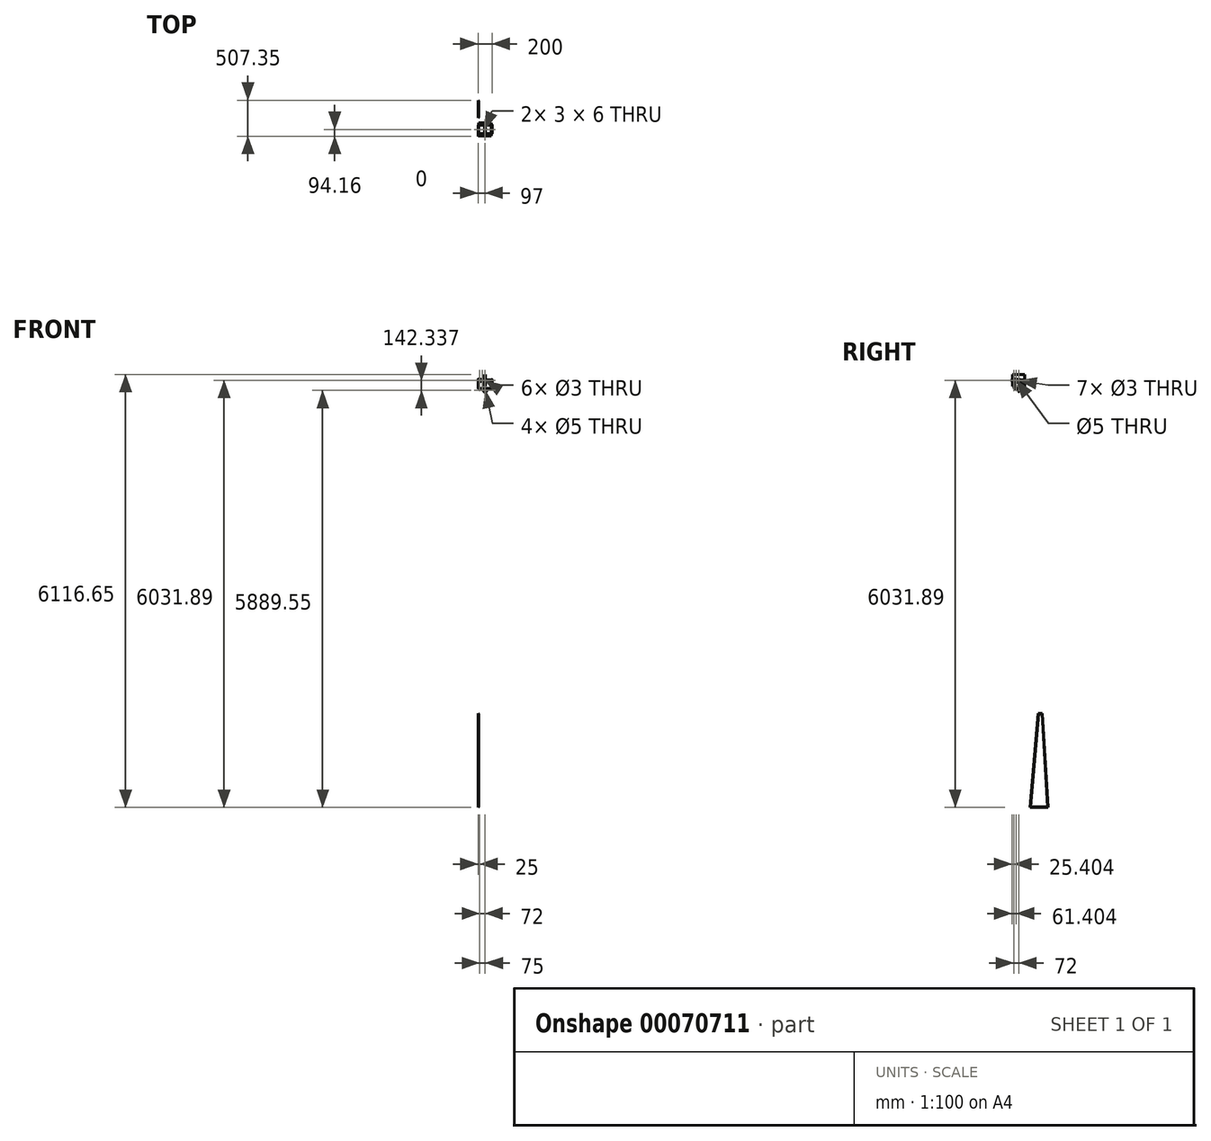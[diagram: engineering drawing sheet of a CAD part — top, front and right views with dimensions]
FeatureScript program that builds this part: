
annotation { "Feature Type Name" : "Feature", "Feature Type Description" : "" }
export const myFeature = defineFeature(function(context is Context, id is Id, definition is map)
    precondition{}
    {
        {
            var Q0;
            Q0=qCreatedBy(makeId("Top.planeOp"),FACE);
            var sketch = newSketch(context, id + "F0", { "sketchPlane" : qUnion([Q0])});
            skLineSegment(sketch, "E0.rect.bottom", {"start": v(100, 60) * mm, "end": v(-95, 60) * mm});
            skLineSegment(sketch, "E0.rect.top", {"start": v(95, -60) * mm, "end": v(-100, -60) * mm});
            skLineSegment(sketch, "E0.rect.left", {"start": v(100, 60) * mm, "end": v(100, 55) * mm});
            skLineSegment(sketch, "E0.rect.right", {"start": v(-100, 55) * mm, "end": v(-100, 50) * mm});
            skPoint(sketch, "E0.rect.middle", {"position": v(0, 0) * mm});
            skLineSegment(sketch, "E1.bottom", {"start": v(100, 55) * mm, "end": v(95, 55) * mm});
            skLineSegment(sketch, "E1.top", {"start": v(100, 50) * mm, "end": v(95, 50) * mm});
            skLineSegment(sketch, "E1.right", {"start": v(95, 55) * mm, "end": v(95, 50) * mm});
            skLineSegment(sketch, "E2.0.1.0", {"start": v(100, 45) * mm, "end": v(95, 45) * mm});
            skLineSegment(sketch, "E2.0.1.1", {"start": v(95, 45) * mm, "end": v(95, 40) * mm});
            skLineSegment(sketch, "E2.0.1.2", {"start": v(100, 40) * mm, "end": v(95, 40) * mm});
            skLineSegment(sketch, "E2.0.2.0", {"start": v(100, 35) * mm, "end": v(95, 35) * mm});
            skLineSegment(sketch, "E2.0.2.1", {"start": v(95, 35) * mm, "end": v(95, 30) * mm});
            skLineSegment(sketch, "E2.0.2.2", {"start": v(100, 30) * mm, "end": v(95, 30) * mm});
            skLineSegment(sketch, "E2.0.3.0", {"start": v(100, 25) * mm, "end": v(95, 25) * mm});
            skLineSegment(sketch, "E2.0.3.1", {"start": v(95, 25) * mm, "end": v(95, 20) * mm});
            skLineSegment(sketch, "E2.0.3.2", {"start": v(100, 20) * mm, "end": v(95, 20) * mm});
            skLineSegment(sketch, "E2.0.4.0", {"start": v(100, 15) * mm, "end": v(95, 15) * mm});
            skLineSegment(sketch, "E2.0.4.1", {"start": v(95, 15) * mm, "end": v(95, 10) * mm});
            skLineSegment(sketch, "E2.0.4.2", {"start": v(100, 10) * mm, "end": v(95, 10) * mm});
            skLineSegment(sketch, "E2.0.5.0", {"start": v(100, 5) * mm, "end": v(95, 5) * mm});
            skLineSegment(sketch, "E2.0.5.1", {"start": v(95, 5) * mm, "end": v(95, 0) * mm});
            skLineSegment(sketch, "E2.0.5.2", {"start": v(100, 0) * mm, "end": v(95, 0) * mm});
            skLineSegment(sketch, "E2.0.6.0", {"start": v(100, -5) * mm, "end": v(95, -5) * mm});
            skLineSegment(sketch, "E2.0.6.1", {"start": v(95, -5) * mm, "end": v(95, -10) * mm});
            skLineSegment(sketch, "E2.0.6.2", {"start": v(100, -10) * mm, "end": v(95, -10) * mm});
            skLineSegment(sketch, "E2.0.7.0", {"start": v(100, -15) * mm, "end": v(95, -15) * mm});
            skLineSegment(sketch, "E2.0.7.1", {"start": v(95, -15) * mm, "end": v(95, -20) * mm});
            skLineSegment(sketch, "E2.0.7.2", {"start": v(100, -20) * mm, "end": v(95, -20) * mm});
            skLineSegment(sketch, "E2.0.8.0", {"start": v(100, -25) * mm, "end": v(95, -25) * mm});
            skLineSegment(sketch, "E2.0.8.1", {"start": v(95, -25) * mm, "end": v(95, -30) * mm});
            skLineSegment(sketch, "E2.0.8.2", {"start": v(100, -30) * mm, "end": v(95, -30) * mm});
            skLineSegment(sketch, "E2.0.9.0", {"start": v(100, -35) * mm, "end": v(95, -35) * mm});
            skLineSegment(sketch, "E2.0.9.1", {"start": v(95, -35) * mm, "end": v(95, -40) * mm});
            skLineSegment(sketch, "E2.0.9.2", {"start": v(100, -40) * mm, "end": v(95, -40) * mm});
            skLineSegment(sketch, "E2.0.10.0", {"start": v(100, -45) * mm, "end": v(95, -45) * mm});
            skLineSegment(sketch, "E2.0.10.1", {"start": v(95, -45) * mm, "end": v(95, -50) * mm});
            skLineSegment(sketch, "E2.0.10.2", {"start": v(100, -50) * mm, "end": v(95, -50) * mm});
            skLineSegment(sketch, "E2.0.11.0", {"start": v(100, -55) * mm, "end": v(95, -55) * mm});
            skLineSegment(sketch, "E2.0.11.1", {"start": v(95, -55) * mm, "end": v(95, -60) * mm});
            skLineSegment(sketch, "E2.direction1", {"start": v(95, 55) * mm, "end": v(119, 55) * mm, "construction": true});
            skLineSegment(sketch, "E2.direction2", {"start": v(95, 55) * mm, "end": v(95, 45) * mm, "construction": true});
            skLineSegment(sketch, "E3", {"start": v(0, -60) * mm, "end": v(0, 60) * mm, "construction": true});
            skLineSegment(sketch, "E4.1.0", {"start": v(-100, -30) * mm, "end": v(-95, -30) * mm});
            skLineSegment(sketch, "E4.1.1", {"start": v(-100, 15) * mm, "end": v(-95, 15) * mm});
            skLineSegment(sketch, "E4.1.2", {"start": v(-95, -35) * mm, "end": v(-95, -30) * mm});
            skLineSegment(sketch, "E4.1.3", {"start": v(-100, 30) * mm, "end": v(-95, 30) * mm});
            skLineSegment(sketch, "E4.1.4", {"start": v(-100, 0) * mm, "end": v(-95, 0) * mm});
            skLineSegment(sketch, "E4.1.5", {"start": v(-100, 55) * mm, "end": v(-95, 55) * mm});
            skLineSegment(sketch, "E4.1.6", {"start": v(-95, 55) * mm, "end": v(-95, 60) * mm});
            skLineSegment(sketch, "E4.1.7", {"start": v(-100, -25) * mm, "end": v(-95, -25) * mm});
            skLineSegment(sketch, "E4.1.8", {"start": v(-100, 5) * mm, "end": v(-95, 5) * mm});
            skLineSegment(sketch, "E4.1.9", {"start": v(-95, -25) * mm, "end": v(-95, -20) * mm});
            skLineSegment(sketch, "E4.1.10", {"start": v(-100, 35) * mm, "end": v(-95, 35) * mm});
            skLineSegment(sketch, "E4.1.11", {"start": v(-100, -20) * mm, "end": v(-95, -20) * mm});
            skLineSegment(sketch, "E4.1.12", {"start": v(-100, -35) * mm, "end": v(-95, -35) * mm});
            skLineSegment(sketch, "E4.1.13", {"start": v(-100, -40) * mm, "end": v(-95, -40) * mm});
            skLineSegment(sketch, "E4.1.14", {"start": v(-95, -45) * mm, "end": v(-95, -40) * mm});
            skLineSegment(sketch, "E4.1.15", {"start": v(-95, -55) * mm, "end": v(-95, -50) * mm});
            skLineSegment(sketch, "E4.1.16", {"start": v(-95, 25) * mm, "end": v(-95, 30) * mm});
            skLineSegment(sketch, "E4.1.17", {"start": v(-100, 50) * mm, "end": v(-95, 50) * mm});
            skLineSegment(sketch, "E4.1.18", {"start": v(-95, -5) * mm, "end": v(-95, 0) * mm});
            skLineSegment(sketch, "E4.1.19", {"start": v(-100, 20) * mm, "end": v(-95, 20) * mm});
            skLineSegment(sketch, "E4.1.20", {"start": v(-95, 45) * mm, "end": v(-95, 50) * mm});
            skLineSegment(sketch, "E4.1.21", {"start": v(-100, 25) * mm, "end": v(-95, 25) * mm});
            skLineSegment(sketch, "E4.1.22", {"start": v(-100, 40) * mm, "end": v(-95, 40) * mm});
            skLineSegment(sketch, "E4.1.23", {"start": v(-100, -5) * mm, "end": v(-95, -5) * mm});
            skLineSegment(sketch, "E4.1.24", {"start": v(-95, 15) * mm, "end": v(-95, 20) * mm});
            skLineSegment(sketch, "E4.1.25", {"start": v(-95, -15) * mm, "end": v(-95, -10) * mm});
            skLineSegment(sketch, "E4.1.26", {"start": v(-100, 10) * mm, "end": v(-95, 10) * mm});
            skLineSegment(sketch, "E4.1.27", {"start": v(-95, 35) * mm, "end": v(-95, 40) * mm});
            skLineSegment(sketch, "E4.1.28", {"start": v(-100, 45) * mm, "end": v(-95, 45) * mm});
            skLineSegment(sketch, "E4.1.29", {"start": v(-100, -10) * mm, "end": v(-95, -10) * mm});
            skLineSegment(sketch, "E4.1.30", {"start": v(-100, -15) * mm, "end": v(-95, -15) * mm});
            skLineSegment(sketch, "E4.1.31", {"start": v(-95, 5) * mm, "end": v(-95, 10) * mm});
            skLineSegment(sketch, "E4.1.32", {"start": v(-100, -45) * mm, "end": v(-95, -45) * mm});
            skLineSegment(sketch, "E4.1.33", {"start": v(-100, -50) * mm, "end": v(-95, -50) * mm});
            skLineSegment(sketch, "E4.1.35", {"start": v(-100, -55) * mm, "end": v(-95, -55) * mm});
            skLineSegment(sketch, "E4.anchor1", {"start": v(0, 0) * mm, "end": v(95, 30) * mm, "construction": true});
            skLineSegment(sketch, "E4.anchor2", {"start": v(0, 0) * mm, "end": v(-95, -30) * mm, "construction": true});
            skLineSegment(sketch, "E5.trimOffspring", {"start": v(100, 50) * mm, "end": v(100, 45) * mm});
            skLineSegment(sketch, "E6.trimOffspring", {"start": v(100, 40) * mm, "end": v(100, 35) * mm});
            skLineSegment(sketch, "E7.trimOffspring", {"start": v(100, 30) * mm, "end": v(100, 25) * mm});
            skLineSegment(sketch, "E8.trimOffspring", {"start": v(100, 20) * mm, "end": v(100, 15) * mm});
            skLineSegment(sketch, "E9.trimOffspring", {"start": v(100, 10) * mm, "end": v(100, 5) * mm});
            skLineSegment(sketch, "E10.trimOffspring", {"start": v(100, 0) * mm, "end": v(100, -5) * mm});
            skLineSegment(sketch, "E11.trimOffspring", {"start": v(100, -10) * mm, "end": v(100, -15) * mm});
            skLineSegment(sketch, "E12.trimOffspring", {"start": v(100, -20) * mm, "end": v(100, -25) * mm});
            skLineSegment(sketch, "E13.trimOffspring", {"start": v(100, -30) * mm, "end": v(100, -35) * mm});
            skLineSegment(sketch, "E14.trimOffspring", {"start": v(100, -40) * mm, "end": v(100, -45) * mm});
            skLineSegment(sketch, "E15.trimOffspring", {"start": v(100, -50) * mm, "end": v(100, -55) * mm});
            skPoint(sketch, "E16.orphan", {"position": v(100, -60) * mm});
            skPoint(sketch, "E17.orphan", {"position": v(-100, 60) * mm});
            skLineSegment(sketch, "E18.trimOffspring", {"start": v(-100, 45) * mm, "end": v(-100, 40) * mm});
            skLineSegment(sketch, "E19.trimOffspring", {"start": v(-100, 35) * mm, "end": v(-100, 30) * mm});
            skLineSegment(sketch, "E20.trimOffspring", {"start": v(-100, 25) * mm, "end": v(-100, 20) * mm});
            skLineSegment(sketch, "E21.trimOffspring", {"start": v(-100, 15) * mm, "end": v(-100, 10) * mm});
            skLineSegment(sketch, "E22.trimOffspring", {"start": v(-100, 5) * mm, "end": v(-100, 0) * mm});
            skLineSegment(sketch, "E23.trimOffspring", {"start": v(-100, -5) * mm, "end": v(-100, -10) * mm});
            skLineSegment(sketch, "E24.trimOffspring", {"start": v(-100, -15) * mm, "end": v(-100, -20) * mm});
            skLineSegment(sketch, "E25.trimOffspring", {"start": v(-100, -55) * mm, "end": v(-100, -60) * mm});
            skLineSegment(sketch, "E26.trimOffspring", {"start": v(-100, -45) * mm, "end": v(-100, -50) * mm});
            skLineSegment(sketch, "E27.trimOffspring", {"start": v(-100, -35) * mm, "end": v(-100, -40) * mm});
            skLineSegment(sketch, "E28.trimOffspring", {"start": v(-100, -25) * mm, "end": v(-100, -30) * mm});
            skSolve(sketch);
        }
        {
            var Q0;
            Q0=makeQuery(id+"F0.imprint","IMPRINT",FACE,{"disambiguationData":[TD([[makeQuery(id+"F0.imprint","IMPRINT",EDGE,{"derivedFrom":sQuery(id+"F0.wireOp",EDGE,"E0.rect.bottom")}),1.0]])]});
            extrude(context, id + "F1", {"entities" : qUnion([Q0]), "depth" : 5 * mm});
        }
        {
            var Q0;
            Q0=makeQuery(id+"F1.opExtrude","SWEPT_FACE",FACE,{"disambiguationData":[OSD([sQuery(id+"F0.wireOp",EDGE,"E5.trimOffspring")])]});
            var sketch = newSketch(context, id + "F2", { "sketchPlane" : qUnion([Q0])});
            skLineSegment(sketch, "E29.bottom", {"start": v(55, 0) * mm, "end": v(50, 0) * mm});
            skLineSegment(sketch, "E29.top", {"start": v(60, 130) * mm, "end": v(-60, 130) * mm, "construction": true});
            skLineSegment(sketch, "E29.left", {"start": v(60, 5) * mm, "end": v(60, 130) * mm, "construction": true});
            skLineSegment(sketch, "E29.right", {"start": v(-60, 0) * mm, "end": v(-60, 130) * mm, "construction": true});
            skLineSegment(sketch, "E30", {"start": v(-57.9, 54.8) * mm, "end": v(-31.55, 115.02) * mm});
            skLineSegment(sketch, "E31", {"start": v(-8.65, 130) * mm, "end": v(8.65, 130) * mm});
            skLineSegment(sketch, "E32", {"start": v(31.55, 115.02) * mm, "end": v(57.9, 54.8) * mm});
            skLineSegment(sketch, "E33", {"start": v(60, 44.77) * mm, "end": v(60, 5) * mm});
            skLineSegment(sketch, "E34", {"start": v(-60, 44.77) * mm, "end": v(-60, 0) * mm});
            skPoint(sketch, "E35", {"position": v(0, 130) * mm});
            skPoint(sketch, "E36.visualSharp", {"position": v(-25, 130) * mm});
            skArc(sketch, "E36.filletArc", {"start": v(-8.65, 130) * mm, "mid": v(-22.33, 125.92) * mm, "end": v(-31.55, 115.02) * mm});
            skPoint(sketch, "E37.visualSharp", {"position": v(-60, 50) * mm});
            skArc(sketch, "E37.filletArc", {"start": v(-57.9, 54.8) * mm, "mid": v(-59.47, 49.89) * mm, "end": v(-60, 44.77) * mm});
            skPoint(sketch, "E38.visualSharp", {"position": v(25, 130) * mm});
            skArc(sketch, "E38.filletArc", {"start": v(31.55, 115.02) * mm, "mid": v(22.33, 125.92) * mm, "end": v(8.65, 130) * mm});
            skPoint(sketch, "E39.visualSharp", {"position": v(60, 50) * mm});
            skArc(sketch, "E39.filletArc", {"start": v(60, 44.77) * mm, "mid": v(59.47, 49.89) * mm, "end": v(57.9, 54.8) * mm});
            skLineSegment(sketch, "E40", {"start": v(0, 130) * mm, "end": v(0, 120) * mm, "construction": true});
            skCircle(sketch, "E41", {"center": v(0, 120) * mm, "radius": 1.5 * mm});
            skLineSegment(sketch, "E42.top", {"start": v(60, 5) * mm, "end": v(55, 5) * mm});
            skLineSegment(sketch, "E42.right", {"start": v(55, 0) * mm, "end": v(55, 5) * mm});
            skLineSegment(sketch, "E43.1.0.0", {"start": v(45, 0) * mm, "end": v(45, 5) * mm});
            skLineSegment(sketch, "E43.1.0.1", {"start": v(50, 5) * mm, "end": v(45, 5) * mm});
            skLineSegment(sketch, "E43.1.0.2", {"start": v(50, 0) * mm, "end": v(50, 5) * mm});
            skLineSegment(sketch, "E43.2.0.0", {"start": v(35, 0) * mm, "end": v(35, 5) * mm});
            skLineSegment(sketch, "E43.2.0.1", {"start": v(40, 5) * mm, "end": v(35, 5) * mm});
            skLineSegment(sketch, "E43.2.0.2", {"start": v(40, 0) * mm, "end": v(40, 5) * mm});
            skLineSegment(sketch, "E43.3.0.0", {"start": v(25, 0) * mm, "end": v(25, 5) * mm});
            skLineSegment(sketch, "E43.3.0.1", {"start": v(30, 5) * mm, "end": v(25, 5) * mm});
            skLineSegment(sketch, "E43.3.0.2", {"start": v(30, 0) * mm, "end": v(30, 5) * mm});
            skLineSegment(sketch, "E43.4.0.0", {"start": v(15, 0) * mm, "end": v(15, 5) * mm});
            skLineSegment(sketch, "E43.4.0.1", {"start": v(20, 5) * mm, "end": v(15, 5) * mm});
            skLineSegment(sketch, "E43.4.0.2", {"start": v(20, 0) * mm, "end": v(20, 5) * mm});
            skLineSegment(sketch, "E43.5.0.0", {"start": v(5, 0) * mm, "end": v(5, 5) * mm});
            skLineSegment(sketch, "E43.5.0.1", {"start": v(10, 5) * mm, "end": v(5, 5) * mm});
            skLineSegment(sketch, "E43.5.0.2", {"start": v(10, 0) * mm, "end": v(10, 5) * mm});
            skLineSegment(sketch, "E43.6.0.0", {"start": v(-5, 0) * mm, "end": v(-5, 5) * mm});
            skLineSegment(sketch, "E43.6.0.1", {"start": v(0, 5) * mm, "end": v(-5, 5) * mm});
            skLineSegment(sketch, "E43.6.0.2", {"start": v(0, 0) * mm, "end": v(0, 5) * mm});
            skLineSegment(sketch, "E43.7.0.0", {"start": v(-15, 0) * mm, "end": v(-15, 5) * mm});
            skLineSegment(sketch, "E43.7.0.1", {"start": v(-10, 5) * mm, "end": v(-15, 5) * mm});
            skLineSegment(sketch, "E43.7.0.2", {"start": v(-10, 0) * mm, "end": v(-10, 5) * mm});
            skLineSegment(sketch, "E43.8.0.0", {"start": v(-25, 0) * mm, "end": v(-25, 5) * mm});
            skLineSegment(sketch, "E43.8.0.1", {"start": v(-20, 5) * mm, "end": v(-25, 5) * mm});
            skLineSegment(sketch, "E43.8.0.2", {"start": v(-20, 0) * mm, "end": v(-20, 5) * mm});
            skLineSegment(sketch, "E43.9.0.0", {"start": v(-35, 0) * mm, "end": v(-35, 5) * mm});
            skLineSegment(sketch, "E43.9.0.1", {"start": v(-30, 5) * mm, "end": v(-35, 5) * mm});
            skLineSegment(sketch, "E43.9.0.2", {"start": v(-30, 0) * mm, "end": v(-30, 5) * mm});
            skLineSegment(sketch, "E43.10.0.0", {"start": v(-45, 0) * mm, "end": v(-45, 5) * mm});
            skLineSegment(sketch, "E43.10.0.1", {"start": v(-40, 5) * mm, "end": v(-45, 5) * mm});
            skLineSegment(sketch, "E43.10.0.2", {"start": v(-40, 0) * mm, "end": v(-40, 5) * mm});
            skLineSegment(sketch, "E43.11.0.0", {"start": v(-55, 0) * mm, "end": v(-55, 5) * mm});
            skLineSegment(sketch, "E43.11.0.1", {"start": v(-50, 5) * mm, "end": v(-55, 5) * mm});
            skLineSegment(sketch, "E43.11.0.2", {"start": v(-50, 0) * mm, "end": v(-50, 5) * mm});
            skLineSegment(sketch, "E43.direction1", {"start": v(55, 0) * mm, "end": v(45, 0) * mm, "construction": true});
            skLineSegment(sketch, "E44.trimOffspring", {"start": v(45, 0) * mm, "end": v(40, 0) * mm});
            skLineSegment(sketch, "E45.trimOffspring", {"start": v(35, 0) * mm, "end": v(30, 0) * mm});
            skLineSegment(sketch, "E46.trimOffspring", {"start": v(25, 0) * mm, "end": v(20, 0) * mm});
            skLineSegment(sketch, "E47.trimOffspring", {"start": v(15, 0) * mm, "end": v(10, 0) * mm});
            skLineSegment(sketch, "E48.trimOffspring", {"start": v(5, 0) * mm, "end": v(0, 0) * mm});
            skLineSegment(sketch, "E49.trimOffspring", {"start": v(-5, 0) * mm, "end": v(-10, 0) * mm});
            skLineSegment(sketch, "E50.trimOffspring", {"start": v(-15, 0) * mm, "end": v(-20, 0) * mm});
            skLineSegment(sketch, "E51.trimOffspring", {"start": v(-25, 0) * mm, "end": v(-30, 0) * mm});
            skLineSegment(sketch, "E52.trimOffspring", {"start": v(-35, 0) * mm, "end": v(-40, 0) * mm});
            skLineSegment(sketch, "E53.trimOffspring", {"start": v(-45, 0) * mm, "end": v(-50, 0) * mm});
            skLineSegment(sketch, "E54.trimOffspring", {"start": v(-55, 0) * mm, "end": v(-60, 0) * mm});
            skSolve(sketch);
        }
        {
            var Q0;
            Q0=qSketchRegion(id+"F2",true);
            extrude(context, id + "F3", {"entities" : qUnion([Q0]), "oppositeDirection" : true, "depth" : 5 * mm});
        }
        {
            var Q0;
            Q0=makeQuery(id+"F1.opExtrude","SWEPT_FACE",FACE,{"disambiguationData":[OSD([sQuery(id+"F0.wireOp",EDGE,"E0.rect.right")])]});
            var sketch = newSketch(context, id + "F4", { "sketchPlane" : qUnion([Q0])});
            skLineSegment(sketch, "E55.bottom", {"start": v(55, 0) * mm, "end": v(50, 0) * mm});
            skLineSegment(sketch, "E55.top", {"start": v(60, 130) * mm, "end": v(-60, 130) * mm, "construction": true});
            skLineSegment(sketch, "E55.left", {"start": v(60, 5) * mm, "end": v(60, 130) * mm, "construction": true});
            skLineSegment(sketch, "E55.right", {"start": v(-60, 0) * mm, "end": v(-60, 130) * mm, "construction": true});
            skLineSegment(sketch, "E56", {"start": v(-60, 0) * mm, "end": v(-60, 44.81) * mm});
            skLineSegment(sketch, "E57", {"start": v(-57.94, 54.76) * mm, "end": v(-31.84, 114.94) * mm});
            skLineSegment(sketch, "E58", {"start": v(-8.9, 130) * mm, "end": v(8.42, 130) * mm});
            skLineSegment(sketch, "E59", {"start": v(31.27, 115.13) * mm, "end": v(57.86, 55.16) * mm});
            skLineSegment(sketch, "E60", {"start": v(60, 45.03) * mm, "end": v(60, 5) * mm});
            skPoint(sketch, "E61.visualSharp", {"position": v(-60, 50) * mm});
            skArc(sketch, "E61.filletArc", {"start": v(-57.94, 54.76) * mm, "mid": v(-59.48, 49.9) * mm, "end": v(-60, 44.81) * mm});
            skPoint(sketch, "E62.visualSharp", {"position": v(-25.32, 130) * mm});
            skArc(sketch, "E62.filletArc", {"start": v(-8.9, 130) * mm, "mid": v(-22.63, 125.9) * mm, "end": v(-31.84, 114.94) * mm});
            skPoint(sketch, "E63.visualSharp", {"position": v(24.68, 130) * mm});
            skArc(sketch, "E63.filletArc", {"start": v(31.27, 115.13) * mm, "mid": v(22.05, 125.96) * mm, "end": v(8.42, 130) * mm});
            skPoint(sketch, "E64.visualSharp", {"position": v(60, 50.32) * mm});
            skArc(sketch, "E64.filletArc", {"start": v(60, 45.03) * mm, "mid": v(59.46, 50.2) * mm, "end": v(57.86, 55.16) * mm});
            skLineSegment(sketch, "E65", {"start": v(-0.24, 130) * mm, "end": v(-0.24, 120) * mm, "construction": true});
            skPoint(sketch, "E65.endSnap0", {"position": v(-0.24, 130) * mm});
            skCircle(sketch, "E66", {"center": v(-0.24, 120) * mm, "radius": 1.5 * mm});
            skLineSegment(sketch, "E67.top", {"start": v(60, 5) * mm, "end": v(55, 5) * mm});
            skLineSegment(sketch, "E67.right", {"start": v(55, 0) * mm, "end": v(55, 5) * mm});
            skLineSegment(sketch, "E68.1.0.0", {"start": v(45, 0) * mm, "end": v(45, 5) * mm});
            skLineSegment(sketch, "E68.1.0.1", {"start": v(50, 5) * mm, "end": v(45, 5) * mm});
            skLineSegment(sketch, "E68.1.0.2", {"start": v(50, 0) * mm, "end": v(50, 5) * mm});
            skLineSegment(sketch, "E68.2.0.0", {"start": v(35, 0) * mm, "end": v(35, 5) * mm});
            skLineSegment(sketch, "E68.2.0.1", {"start": v(40, 5) * mm, "end": v(35, 5) * mm});
            skLineSegment(sketch, "E68.2.0.2", {"start": v(40, 0) * mm, "end": v(40, 5) * mm});
            skLineSegment(sketch, "E68.3.0.0", {"start": v(25, 0) * mm, "end": v(25, 5) * mm});
            skLineSegment(sketch, "E68.3.0.1", {"start": v(30, 5) * mm, "end": v(25, 5) * mm});
            skLineSegment(sketch, "E68.3.0.2", {"start": v(30, 0) * mm, "end": v(30, 5) * mm});
            skLineSegment(sketch, "E68.4.0.0", {"start": v(15, 0) * mm, "end": v(15, 5) * mm});
            skLineSegment(sketch, "E68.4.0.1", {"start": v(20, 5) * mm, "end": v(15, 5) * mm});
            skLineSegment(sketch, "E68.4.0.2", {"start": v(20, 0) * mm, "end": v(20, 5) * mm});
            skLineSegment(sketch, "E68.5.0.0", {"start": v(5, 0) * mm, "end": v(5, 5) * mm});
            skLineSegment(sketch, "E68.5.0.1", {"start": v(10, 5) * mm, "end": v(5, 5) * mm});
            skLineSegment(sketch, "E68.5.0.2", {"start": v(10, 0) * mm, "end": v(10, 5) * mm});
            skLineSegment(sketch, "E68.6.0.0", {"start": v(-5, 0) * mm, "end": v(-5, 5) * mm});
            skLineSegment(sketch, "E68.6.0.1", {"start": v(0, 5) * mm, "end": v(-5, 5) * mm});
            skLineSegment(sketch, "E68.6.0.2", {"start": v(0, 0) * mm, "end": v(0, 5) * mm});
            skLineSegment(sketch, "E68.7.0.0", {"start": v(-15, 0) * mm, "end": v(-15, 5) * mm});
            skLineSegment(sketch, "E68.7.0.1", {"start": v(-10, 5) * mm, "end": v(-15, 5) * mm});
            skLineSegment(sketch, "E68.7.0.2", {"start": v(-10, 0) * mm, "end": v(-10, 5) * mm});
            skLineSegment(sketch, "E68.8.0.0", {"start": v(-25, 0) * mm, "end": v(-25, 5) * mm});
            skLineSegment(sketch, "E68.8.0.1", {"start": v(-20, 5) * mm, "end": v(-25, 5) * mm});
            skLineSegment(sketch, "E68.8.0.2", {"start": v(-20, 0) * mm, "end": v(-20, 5) * mm});
            skLineSegment(sketch, "E68.9.0.0", {"start": v(-35, 0) * mm, "end": v(-35, 5) * mm});
            skLineSegment(sketch, "E68.9.0.1", {"start": v(-30, 5) * mm, "end": v(-35, 5) * mm});
            skLineSegment(sketch, "E68.9.0.2", {"start": v(-30, 0) * mm, "end": v(-30, 5) * mm});
            skLineSegment(sketch, "E68.10.0.0", {"start": v(-45, 0) * mm, "end": v(-45, 5) * mm});
            skLineSegment(sketch, "E68.10.0.1", {"start": v(-40, 5) * mm, "end": v(-45, 5) * mm});
            skLineSegment(sketch, "E68.10.0.2", {"start": v(-40, 0) * mm, "end": v(-40, 5) * mm});
            skLineSegment(sketch, "E68.11.0.0", {"start": v(-55, 0) * mm, "end": v(-55, 5) * mm});
            skLineSegment(sketch, "E68.11.0.1", {"start": v(-50, 5) * mm, "end": v(-55, 5) * mm});
            skLineSegment(sketch, "E68.11.0.2", {"start": v(-50, 0) * mm, "end": v(-50, 5) * mm});
            skLineSegment(sketch, "E68.direction1", {"start": v(55, 0) * mm, "end": v(45, 0) * mm, "construction": true});
            skLineSegment(sketch, "E69.trimOffspring", {"start": v(45, 0) * mm, "end": v(40, 0) * mm});
            skLineSegment(sketch, "E70.trimOffspring", {"start": v(35, 0) * mm, "end": v(30, 0) * mm});
            skLineSegment(sketch, "E71.trimOffspring", {"start": v(25, 0) * mm, "end": v(20, 0) * mm});
            skLineSegment(sketch, "E72.trimOffspring", {"start": v(15, 0) * mm, "end": v(10, 0) * mm});
            skLineSegment(sketch, "E73.trimOffspring", {"start": v(5, 0) * mm, "end": v(0, 0) * mm});
            skLineSegment(sketch, "E74.trimOffspring", {"start": v(-5, 0) * mm, "end": v(-10, 0) * mm});
            skLineSegment(sketch, "E75.trimOffspring", {"start": v(-15, 0) * mm, "end": v(-20, 0) * mm});
            skLineSegment(sketch, "E76.trimOffspring", {"start": v(-25, 0) * mm, "end": v(-30, 0) * mm});
            skLineSegment(sketch, "E77.trimOffspring", {"start": v(-35, 0) * mm, "end": v(-40, 0) * mm});
            skLineSegment(sketch, "E78.trimOffspring", {"start": v(-45, 0) * mm, "end": v(-50, 0) * mm});
            skLineSegment(sketch, "E79.trimOffspring", {"start": v(-55, 0) * mm, "end": v(-60, 0) * mm});
            skSolve(sketch);
        }
        {
            var Q0;
            Q0=qSketchRegion(id+"F4",true);
            extrude(context, id + "F5", {"entities" : qUnion([Q0]), "oppositeDirection" : true, "depth" : 5 * mm});
        }
        {
            var Q0;
            Q0=makeQuery(id+"F5.opExtrude","CAP_FACE",FACE,{"disambiguationData":[OSD([sQuery(id+"F4.wireOp",EDGE,"E55.bottom"),sQuery(id+"F4.wireOp",EDGE,"E56"),sQuery(id+"F4.wireOp",EDGE,"E57"),sQuery(id+"F4.wireOp",EDGE,"E58"),sQuery(id+"F4.wireOp",EDGE,"E59"),sQuery(id+"F4.wireOp",EDGE,"E60"),sQuery(id+"F4.wireOp",EDGE,"E61.filletArc"),sQuery(id+"F4.wireOp",EDGE,"E62.filletArc"),sQuery(id+"F4.wireOp",EDGE,"E63.filletArc"),sQuery(id+"F4.wireOp",EDGE,"E64.filletArc"),sQuery(id+"F4.wireOp",EDGE,"E66"),sQuery(id+"F4.wireOp",EDGE,"E67.top"),sQuery(id+"F4.wireOp",EDGE,"E67.right"),sQuery(id+"F4.wireOp",EDGE,"E68.1.0.0"),sQuery(id+"F4.wireOp",EDGE,"E68.1.0.1"),sQuery(id+"F4.wireOp",EDGE,"E68.1.0.2"),sQuery(id+"F4.wireOp",EDGE,"E68.2.0.0"),sQuery(id+"F4.wireOp",EDGE,"E68.2.0.1"),sQuery(id+"F4.wireOp",EDGE,"E68.2.0.2"),sQuery(id+"F4.wireOp",EDGE,"E68.3.0.0"),sQuery(id+"F4.wireOp",EDGE,"E68.3.0.1"),sQuery(id+"F4.wireOp",EDGE,"E68.3.0.2"),sQuery(id+"F4.wireOp",EDGE,"E68.4.0.0"),sQuery(id+"F4.wireOp",EDGE,"E68.4.0.1"),sQuery(id+"F4.wireOp",EDGE,"E68.4.0.2"),sQuery(id+"F4.wireOp",EDGE,"E68.5.0.0"),sQuery(id+"F4.wireOp",EDGE,"E68.5.0.1"),sQuery(id+"F4.wireOp",EDGE,"E68.5.0.2"),sQuery(id+"F4.wireOp",EDGE,"E68.6.0.0"),sQuery(id+"F4.wireOp",EDGE,"E68.6.0.1"),sQuery(id+"F4.wireOp",EDGE,"E68.6.0.2"),sQuery(id+"F4.wireOp",EDGE,"E68.7.0.0"),sQuery(id+"F4.wireOp",EDGE,"E68.7.0.1"),sQuery(id+"F4.wireOp",EDGE,"E68.7.0.2"),sQuery(id+"F4.wireOp",EDGE,"E68.8.0.0"),sQuery(id+"F4.wireOp",EDGE,"E68.8.0.1"),sQuery(id+"F4.wireOp",EDGE,"E68.8.0.2"),sQuery(id+"F4.wireOp",EDGE,"E68.9.0.0"),sQuery(id+"F4.wireOp",EDGE,"E68.9.0.1"),sQuery(id+"F4.wireOp",EDGE,"E68.9.0.2"),sQuery(id+"F4.wireOp",EDGE,"E68.10.0.0"),sQuery(id+"F4.wireOp",EDGE,"E68.10.0.1"),sQuery(id+"F4.wireOp",EDGE,"E68.10.0.2"),sQuery(id+"F4.wireOp",EDGE,"E68.11.0.0"),sQuery(id+"F4.wireOp",EDGE,"E68.11.0.1"),sQuery(id+"F4.wireOp",EDGE,"E68.11.0.2"),sQuery(id+"F4.wireOp",EDGE,"E69.trimOffspring"),sQuery(id+"F4.wireOp",EDGE,"E70.trimOffspring"),sQuery(id+"F4.wireOp",EDGE,"E71.trimOffspring"),sQuery(id+"F4.wireOp",EDGE,"E72.trimOffspring"),sQuery(id+"F4.wireOp",EDGE,"E73.trimOffspring"),sQuery(id+"F4.wireOp",EDGE,"E74.trimOffspring"),sQuery(id+"F4.wireOp",EDGE,"E75.trimOffspring"),sQuery(id+"F4.wireOp",EDGE,"E76.trimOffspring"),sQuery(id+"F4.wireOp",EDGE,"E77.trimOffspring"),sQuery(id+"F4.wireOp",EDGE,"E78.trimOffspring"),sQuery(id+"F4.wireOp",EDGE,"E79.trimOffspring")])],"isStart":false});
            var sketch = newSketch(context, id + "F6", { "sketchPlane" : qUnion([Q0])});
            skCircle(sketch, "E80", {"center": v(0.24, 120) * mm, "radius": 16.4 * mm, "construction": true});
            skCircle(sketch, "E81", {"center": v(0.24, 120) * mm, "radius": 19.4 * mm, "construction": true});
            skCircle(sketch, "E82", {"center": v(0.24, 120) * mm, "radius": 1.5 * mm});
            skLineSegment(sketch, "E83", {"start": v(0.24, 120) * mm, "end": v(0.24, 139.4) * mm, "construction": true});
            skLineSegment(sketch, "E84", {"start": v(0.24, 120) * mm, "end": v(-3.12, 139.1) * mm, "construction": true});
            skLineSegment(sketch, "E85", {"start": v(0.24, 120) * mm, "end": v(-1.45, 139.33) * mm, "construction": true});
            skLineSegment(sketch, "E86", {"start": v(0.24, 120) * mm, "end": v(-0.6, 139.38) * mm, "construction": true});
            skLineSegment(sketch, "E87", {"start": v(0.24, 120) * mm, "end": v(-2.29, 139.23) * mm, "construction": true});
            skLineSegment(sketch, "E88", {"start": v(-0.18, 139.4) * mm, "end": v(0.24, 120) * mm, "construction": true});
            skLineSegment(sketch, "E89", {"start": v(-2.7, 139.17) * mm, "end": v(0.24, 120) * mm, "construction": true});
            skLineSegment(sketch, "E90", {"start": v(-1.02, 139.36) * mm, "end": v(0.24, 120) * mm, "construction": true});
            skLineSegment(sketch, "E91", {"start": v(-1.87, 139.28) * mm, "end": v(0.24, 120) * mm, "construction": true});
            skArc(sketch, "E92", {"start": v(-1.43, 139.33) * mm, "mid": v(-1.45, 139.33) * mm, "end": v(-1.47, 139.32) * mm});
            skLineSegment(sketch, "E93", {"start": v(-0.9, 138.98) * mm, "end": v(-0.22, 136.76) * mm});
            skLineSegment(sketch, "E94", {"start": v(-1.92, 138.89) * mm, "end": v(-2.2, 136.58) * mm});
            skLineSegment(sketch, "E95", {"start": v(0.24, 136.4) * mm, "end": v(0.26, 136.4) * mm});
            skLineSegment(sketch, "E96", {"start": v(-2.6, 136.15) * mm, "end": v(-2.62, 136.15) * mm});
            skPoint(sketch, "E97.visualSharp", {"position": v(-0.11, 136.4) * mm});
            skArc(sketch, "E97.filletArc", {"start": v(-0.22, 136.76) * mm, "mid": v(-0.04, 136.5) * mm, "end": v(0.26, 136.4) * mm});
            skPoint(sketch, "E98.visualSharp", {"position": v(-2.25, 136.2) * mm});
            skArc(sketch, "E98.filletArc", {"start": v(-2.62, 136.15) * mm, "mid": v(-2.34, 136.3) * mm, "end": v(-2.2, 136.58) * mm});
            skPoint(sketch, "E99.visualSharp", {"position": v(-1.02, 139.36) * mm});
            skArc(sketch, "E99.filletArc", {"start": v(-0.9, 138.98) * mm, "mid": v(-1.1, 139.24) * mm, "end": v(-1.43, 139.33) * mm});
            skPoint(sketch, "E100.visualSharp", {"position": v(-1.87, 139.28) * mm});
            skArc(sketch, "E100.filletArc", {"start": v(-1.47, 139.32) * mm, "mid": v(-1.77, 139.19) * mm, "end": v(-1.92, 138.89) * mm});
            skLineSegment(sketch, "E101.1.0", {"start": v(-2.6, 136.15) * mm, "end": v(-2.58, 136.16) * mm});
            skArc(sketch, "E101.1.1", {"start": v(-3.13, 136.42) * mm, "mid": v(-2.9, 136.2) * mm, "end": v(-2.58, 136.16) * mm});
            skLineSegment(sketch, "E101.1.2", {"start": v(-4.19, 138.49) * mm, "end": v(-3.13, 136.42) * mm});
            skArc(sketch, "E101.1.3", {"start": v(-4.19, 138.49) * mm, "mid": v(-4.43, 138.72) * mm, "end": v(-4.76, 138.74) * mm});
            skArc(sketch, "E101.1.4", {"start": v(-4.76, 138.74) * mm, "mid": v(-4.78, 138.74) * mm, "end": v(-4.8, 138.73) * mm});
            skArc(sketch, "E101.1.5", {"start": v(-4.8, 138.73) * mm, "mid": v(-5.07, 138.55) * mm, "end": v(-5.16, 138.23) * mm});
            skLineSegment(sketch, "E101.1.6", {"start": v(-5.16, 138.23) * mm, "end": v(-5.05, 135.9) * mm});
            skArc(sketch, "E101.1.7", {"start": v(-5.39, 135.4) * mm, "mid": v(-5.13, 135.6) * mm, "end": v(-5.05, 135.9) * mm});
            skLineSegment(sketch, "E101.1.8", {"start": v(-5.37, 135.41) * mm, "end": v(-5.39, 135.4) * mm});
            skLineSegment(sketch, "E101.2.0", {"start": v(-5.37, 135.41) * mm, "end": v(-5.35, 135.42) * mm});
            skArc(sketch, "E101.2.1", {"start": v(-5.93, 135.59) * mm, "mid": v(-5.67, 135.4) * mm, "end": v(-5.35, 135.42) * mm});
            skLineSegment(sketch, "E101.2.2", {"start": v(-7.33, 137.44) * mm, "end": v(-5.93, 135.59) * mm});
            skArc(sketch, "E101.2.3", {"start": v(-7.33, 137.44) * mm, "mid": v(-7.6, 137.62) * mm, "end": v(-7.94, 137.6) * mm});
            skArc(sketch, "E101.2.4", {"start": v(-7.94, 137.6) * mm, "mid": v(-7.95, 137.58) * mm, "end": v(-7.97, 137.57) * mm});
            skArc(sketch, "E101.2.5", {"start": v(-7.97, 137.57) * mm, "mid": v(-8.2, 137.34) * mm, "end": v(-8.25, 137) * mm});
            skLineSegment(sketch, "E101.2.6", {"start": v(-8.25, 137) * mm, "end": v(-7.73, 134.75) * mm});
            skArc(sketch, "E101.2.7", {"start": v(-7.98, 134.2) * mm, "mid": v(-7.76, 134.43) * mm, "end": v(-7.73, 134.75) * mm});
            skLineSegment(sketch, "E101.2.8", {"start": v(-7.96, 134.2) * mm, "end": v(-7.98, 134.2) * mm});
            skLineSegment(sketch, "E101.3.0", {"start": v(-7.96, 134.2) * mm, "end": v(-7.94, 134.22) * mm});
            skArc(sketch, "E101.3.1", {"start": v(-8.54, 134.28) * mm, "mid": v(-8.25, 134.15) * mm, "end": v(-7.94, 134.22) * mm});
            skLineSegment(sketch, "E101.3.2", {"start": v(-10.24, 135.86) * mm, "end": v(-8.54, 134.28) * mm});
            skArc(sketch, "E101.3.3", {"start": v(-10.24, 135.86) * mm, "mid": v(-10.55, 136) * mm, "end": v(-10.87, 135.9) * mm});
            skArc(sketch, "E101.3.4", {"start": v(-10.87, 135.9) * mm, "mid": v(-10.88, 135.9) * mm, "end": v(-10.9, 135.88) * mm});
            skArc(sketch, "E101.3.5", {"start": v(-10.9, 135.88) * mm, "mid": v(-11.1, 135.6) * mm, "end": v(-11.07, 135.28) * mm});
            skLineSegment(sketch, "E101.3.6", {"start": v(-11.07, 135.28) * mm, "end": v(-10.17, 133.14) * mm});
            skArc(sketch, "E101.3.7", {"start": v(-10.32, 132.55) * mm, "mid": v(-10.14, 132.82) * mm, "end": v(-10.17, 133.14) * mm});
            skLineSegment(sketch, "E101.3.8", {"start": v(-10.3, 132.57) * mm, "end": v(-10.32, 132.55) * mm});
            skLineSegment(sketch, "E101.4.0", {"start": v(-10.3, 132.57) * mm, "end": v(-10.29, 132.58) * mm});
            skArc(sketch, "E101.4.1", {"start": v(-10.89, 132.54) * mm, "mid": v(-10.58, 132.46) * mm, "end": v(-10.29, 132.58) * mm});
            skLineSegment(sketch, "E101.4.2", {"start": v(-12.84, 133.8) * mm, "end": v(-10.89, 132.54) * mm});
            skArc(sketch, "E101.4.3", {"start": v(-12.84, 133.8) * mm, "mid": v(-13.16, 133.87) * mm, "end": v(-13.46, 133.73) * mm});
            skArc(sketch, "E101.4.4", {"start": v(-13.46, 133.73) * mm, "mid": v(-13.47, 133.72) * mm, "end": v(-13.49, 133.7) * mm});
            skArc(sketch, "E101.4.5", {"start": v(-13.49, 133.7) * mm, "mid": v(-13.63, 133.4) * mm, "end": v(-13.55, 133.08) * mm});
            skLineSegment(sketch, "E101.4.6", {"start": v(-13.55, 133.08) * mm, "end": v(-12.3, 131.13) * mm});
            skArc(sketch, "E101.4.7", {"start": v(-12.34, 130.53) * mm, "mid": v(-12.21, 130.82) * mm, "end": v(-12.3, 131.13) * mm});
            skLineSegment(sketch, "E101.4.8", {"start": v(-12.32, 130.54) * mm, "end": v(-12.34, 130.53) * mm});
            skLineSegment(sketch, "E101.5.0", {"start": v(-12.32, 130.54) * mm, "end": v(-12.3, 130.56) * mm});
            skArc(sketch, "E101.5.1", {"start": v(-12.9, 130.41) * mm, "mid": v(-12.58, 130.39) * mm, "end": v(-12.3, 130.56) * mm});
            skLineSegment(sketch, "E101.5.2", {"start": v(-15.03, 131.32) * mm, "end": v(-12.9, 130.41) * mm});
            skArc(sketch, "E101.5.3", {"start": v(-15.03, 131.32) * mm, "mid": v(-15.37, 131.34) * mm, "end": v(-15.64, 131.14) * mm});
            skArc(sketch, "E101.5.4", {"start": v(-15.64, 131.14) * mm, "mid": v(-15.65, 131.13) * mm, "end": v(-15.66, 131.11) * mm});
            skArc(sketch, "E101.5.5", {"start": v(-15.66, 131.11) * mm, "mid": v(-15.75, 130.8) * mm, "end": v(-15.61, 130.49) * mm});
            skLineSegment(sketch, "E101.5.6", {"start": v(-15.61, 130.49) * mm, "end": v(-14.03, 128.78) * mm});
            skArc(sketch, "E101.5.7", {"start": v(-13.97, 128.18) * mm, "mid": v(-13.9, 128.5) * mm, "end": v(-14.03, 128.78) * mm});
            skLineSegment(sketch, "E101.5.8", {"start": v(-13.96, 128.2) * mm, "end": v(-13.97, 128.18) * mm});
            skLineSegment(sketch, "E101.6.0", {"start": v(-13.96, 128.2) * mm, "end": v(-13.95, 128.22) * mm});
            skArc(sketch, "E101.6.1", {"start": v(-14.5, 127.97) * mm, "mid": v(-14.19, 128) * mm, "end": v(-13.95, 128.22) * mm});
            skLineSegment(sketch, "E101.6.2", {"start": v(-16.77, 128.5) * mm, "end": v(-14.5, 127.97) * mm});
            skArc(sketch, "E101.6.3", {"start": v(-16.77, 128.5) * mm, "mid": v(-17.1, 128.45) * mm, "end": v(-17.33, 128.22) * mm});
            skArc(sketch, "E101.6.4", {"start": v(-17.33, 128.22) * mm, "mid": v(-17.34, 128.2) * mm, "end": v(-17.35, 128.18) * mm});
            skArc(sketch, "E101.6.5", {"start": v(-17.35, 128.18) * mm, "mid": v(-17.38, 127.85) * mm, "end": v(-17.2, 127.57) * mm});
            skLineSegment(sketch, "E101.6.6", {"start": v(-17.2, 127.57) * mm, "end": v(-15.34, 126.17) * mm});
            skArc(sketch, "E101.6.7", {"start": v(-15.18, 125.6) * mm, "mid": v(-15.16, 125.9) * mm, "end": v(-15.34, 126.17) * mm});
            skLineSegment(sketch, "E101.6.8", {"start": v(-15.17, 125.61) * mm, "end": v(-15.18, 125.6) * mm});
            skLineSegment(sketch, "E101.7.0", {"start": v(-15.17, 125.61) * mm, "end": v(-15.16, 125.63) * mm});
            skArc(sketch, "E101.7.1", {"start": v(-15.66, 125.3) * mm, "mid": v(-15.36, 125.38) * mm, "end": v(-15.16, 125.63) * mm});
            skLineSegment(sketch, "E101.7.2", {"start": v(-17.98, 125.4) * mm, "end": v(-15.66, 125.3) * mm});
            skArc(sketch, "E101.7.3", {"start": v(-17.98, 125.4) * mm, "mid": v(-18.3, 125.31) * mm, "end": v(-18.5, 125.04) * mm});
            skArc(sketch, "E101.7.4", {"start": v(-18.5, 125.04) * mm, "mid": v(-18.5, 125.02) * mm, "end": v(-18.5, 125) * mm});
            skArc(sketch, "E101.7.5", {"start": v(-18.5, 125) * mm, "mid": v(-18.47, 124.67) * mm, "end": v(-18.24, 124.43) * mm});
            skLineSegment(sketch, "E101.7.6", {"start": v(-18.24, 124.43) * mm, "end": v(-16.18, 123.37) * mm});
            skArc(sketch, "E101.7.7", {"start": v(-15.91, 122.83) * mm, "mid": v(-15.95, 123.14) * mm, "end": v(-16.18, 123.37) * mm});
            skLineSegment(sketch, "E101.7.8", {"start": v(-15.91, 122.85) * mm, "end": v(-15.91, 122.83) * mm});
            skLineSegment(sketch, "E101.8.0", {"start": v(-15.91, 122.85) * mm, "end": v(-15.9, 122.87) * mm});
            skArc(sketch, "E101.8.1", {"start": v(-16.34, 122.45) * mm, "mid": v(-16.05, 122.59) * mm, "end": v(-15.9, 122.87) * mm});
            skLineSegment(sketch, "E101.8.2", {"start": v(-18.64, 122.16) * mm, "end": v(-16.34, 122.45) * mm});
            skArc(sketch, "E101.8.3", {"start": v(-18.64, 122.16) * mm, "mid": v(-18.94, 122.01) * mm, "end": v(-19.08, 121.7) * mm});
            skArc(sketch, "E101.8.4", {"start": v(-19.08, 121.7) * mm, "mid": v(-19.08, 121.7) * mm, "end": v(-19.08, 121.67) * mm});
            skArc(sketch, "E101.8.5", {"start": v(-19.08, 121.67) * mm, "mid": v(-19, 121.35) * mm, "end": v(-18.73, 121.15) * mm});
            skLineSegment(sketch, "E101.8.6", {"start": v(-18.73, 121.15) * mm, "end": v(-16.51, 120.47) * mm});
            skArc(sketch, "E101.8.7", {"start": v(-16.16, 119.98) * mm, "mid": v(-16.25, 120.28) * mm, "end": v(-16.51, 120.47) * mm});
            skLineSegment(sketch, "E101.8.8", {"start": v(-16.16, 120) * mm, "end": v(-16.16, 119.98) * mm});
            skLineSegment(sketch, "E101.9.0", {"start": v(-16.16, 120) * mm, "end": v(-16.16, 120.02) * mm});
            skArc(sketch, "E101.9.1", {"start": v(-16.51, 119.53) * mm, "mid": v(-16.25, 119.72) * mm, "end": v(-16.16, 120.02) * mm});
            skLineSegment(sketch, "E101.9.2", {"start": v(-18.73, 118.85) * mm, "end": v(-16.51, 119.53) * mm});
            skArc(sketch, "E101.9.3", {"start": v(-18.73, 118.85) * mm, "mid": v(-19, 118.65) * mm, "end": v(-19.08, 118.33) * mm});
            skArc(sketch, "E101.9.4", {"start": v(-19.08, 118.33) * mm, "mid": v(-19.08, 118.3) * mm, "end": v(-19.08, 118.3) * mm});
            skArc(sketch, "E101.9.5", {"start": v(-19.08, 118.3) * mm, "mid": v(-18.94, 117.99) * mm, "end": v(-18.64, 117.84) * mm});
            skLineSegment(sketch, "E101.9.6", {"start": v(-18.64, 117.84) * mm, "end": v(-16.34, 117.55) * mm});
            skArc(sketch, "E101.9.7", {"start": v(-15.9, 117.13) * mm, "mid": v(-16.05, 117.41) * mm, "end": v(-16.34, 117.55) * mm});
            skLineSegment(sketch, "E101.9.8", {"start": v(-15.91, 117.15) * mm, "end": v(-15.9, 117.13) * mm});
            skLineSegment(sketch, "E101.10.0", {"start": v(-15.91, 117.15) * mm, "end": v(-15.91, 117.17) * mm});
            skArc(sketch, "E101.10.1", {"start": v(-16.18, 116.63) * mm, "mid": v(-15.95, 116.86) * mm, "end": v(-15.91, 117.17) * mm});
            skLineSegment(sketch, "E101.10.2", {"start": v(-18.24, 115.57) * mm, "end": v(-16.18, 116.63) * mm});
            skArc(sketch, "E101.10.3", {"start": v(-18.24, 115.57) * mm, "mid": v(-18.47, 115.33) * mm, "end": v(-18.5, 115) * mm});
            skArc(sketch, "E101.10.4", {"start": v(-18.5, 115) * mm, "mid": v(-18.5, 114.98) * mm, "end": v(-18.5, 114.96) * mm});
            skArc(sketch, "E101.10.5", {"start": v(-18.5, 114.96) * mm, "mid": v(-18.3, 114.69) * mm, "end": v(-17.98, 114.6) * mm});
            skLineSegment(sketch, "E101.10.6", {"start": v(-17.98, 114.6) * mm, "end": v(-15.66, 114.7) * mm});
            skArc(sketch, "E101.10.7", {"start": v(-15.16, 114.37) * mm, "mid": v(-15.36, 114.62) * mm, "end": v(-15.66, 114.7) * mm});
            skLineSegment(sketch, "E101.10.8", {"start": v(-15.17, 114.39) * mm, "end": v(-15.16, 114.37) * mm});
            skLineSegment(sketch, "E101.11.0", {"start": v(-15.17, 114.39) * mm, "end": v(-15.18, 114.4) * mm});
            skArc(sketch, "E101.11.1", {"start": v(-15.34, 113.83) * mm, "mid": v(-15.16, 114.1) * mm, "end": v(-15.18, 114.4) * mm});
            skLineSegment(sketch, "E101.11.2", {"start": v(-17.2, 112.43) * mm, "end": v(-15.34, 113.83) * mm});
            skArc(sketch, "E101.11.3", {"start": v(-17.2, 112.43) * mm, "mid": v(-17.38, 112.15) * mm, "end": v(-17.35, 111.82) * mm});
            skArc(sketch, "E101.11.4", {"start": v(-17.35, 111.82) * mm, "mid": v(-17.34, 111.8) * mm, "end": v(-17.33, 111.78) * mm});
            skArc(sketch, "E101.11.5", {"start": v(-17.33, 111.78) * mm, "mid": v(-17.1, 111.55) * mm, "end": v(-16.77, 111.5) * mm});
            skLineSegment(sketch, "E101.11.6", {"start": v(-16.77, 111.5) * mm, "end": v(-14.5, 112.03) * mm});
            skArc(sketch, "E101.11.7", {"start": v(-13.95, 111.78) * mm, "mid": v(-14.19, 112) * mm, "end": v(-14.5, 112.03) * mm});
            skLineSegment(sketch, "E101.11.8", {"start": v(-13.96, 111.8) * mm, "end": v(-13.95, 111.78) * mm});
            skLineSegment(sketch, "E101.12.0", {"start": v(-13.96, 111.8) * mm, "end": v(-13.97, 111.82) * mm});
            skArc(sketch, "E101.12.1", {"start": v(-14.03, 111.22) * mm, "mid": v(-13.9, 111.5) * mm, "end": v(-13.97, 111.82) * mm});
            skLineSegment(sketch, "E101.12.2", {"start": v(-15.61, 109.51) * mm, "end": v(-14.03, 111.22) * mm});
            skArc(sketch, "E101.12.3", {"start": v(-15.61, 109.51) * mm, "mid": v(-15.75, 109.2) * mm, "end": v(-15.66, 108.89) * mm});
            skArc(sketch, "E101.12.4", {"start": v(-15.66, 108.89) * mm, "mid": v(-15.65, 108.87) * mm, "end": v(-15.64, 108.86) * mm});
            skArc(sketch, "E101.12.5", {"start": v(-15.64, 108.86) * mm, "mid": v(-15.37, 108.66) * mm, "end": v(-15.03, 108.68) * mm});
            skLineSegment(sketch, "E101.12.6", {"start": v(-15.03, 108.68) * mm, "end": v(-12.9, 109.59) * mm});
            skArc(sketch, "E101.12.7", {"start": v(-12.3, 109.44) * mm, "mid": v(-12.58, 109.61) * mm, "end": v(-12.9, 109.59) * mm});
            skLineSegment(sketch, "E101.12.8", {"start": v(-12.32, 109.46) * mm, "end": v(-12.3, 109.44) * mm});
            skLineSegment(sketch, "E101.13.0", {"start": v(-12.32, 109.46) * mm, "end": v(-12.34, 109.47) * mm});
            skArc(sketch, "E101.13.1", {"start": v(-12.3, 108.87) * mm, "mid": v(-12.21, 109.18) * mm, "end": v(-12.34, 109.47) * mm});
            skLineSegment(sketch, "E101.13.2", {"start": v(-13.55, 106.92) * mm, "end": v(-12.3, 108.87) * mm});
            skArc(sketch, "E101.13.3", {"start": v(-13.55, 106.92) * mm, "mid": v(-13.63, 106.6) * mm, "end": v(-13.49, 106.3) * mm});
            skArc(sketch, "E101.13.4", {"start": v(-13.49, 106.3) * mm, "mid": v(-13.47, 106.28) * mm, "end": v(-13.46, 106.27) * mm});
            skArc(sketch, "E101.13.5", {"start": v(-13.46, 106.27) * mm, "mid": v(-13.16, 106.13) * mm, "end": v(-12.84, 106.2) * mm});
            skLineSegment(sketch, "E101.13.6", {"start": v(-12.84, 106.2) * mm, "end": v(-10.89, 107.46) * mm});
            skArc(sketch, "E101.13.7", {"start": v(-10.29, 107.42) * mm, "mid": v(-10.58, 107.54) * mm, "end": v(-10.89, 107.46) * mm});
            skLineSegment(sketch, "E101.13.8", {"start": v(-10.3, 107.43) * mm, "end": v(-10.29, 107.42) * mm});
            skLineSegment(sketch, "E101.14.0", {"start": v(-10.3, 107.43) * mm, "end": v(-10.32, 107.45) * mm});
            skArc(sketch, "E101.14.1", {"start": v(-10.17, 106.86) * mm, "mid": v(-10.14, 107.18) * mm, "end": v(-10.32, 107.45) * mm});
            skLineSegment(sketch, "E101.14.2", {"start": v(-11.07, 104.72) * mm, "end": v(-10.17, 106.86) * mm});
            skArc(sketch, "E101.14.3", {"start": v(-11.07, 104.72) * mm, "mid": v(-11.1, 104.4) * mm, "end": v(-10.9, 104.12) * mm});
            skArc(sketch, "E101.14.4", {"start": v(-10.9, 104.12) * mm, "mid": v(-10.88, 104.1) * mm, "end": v(-10.87, 104.1) * mm});
            skArc(sketch, "E101.14.5", {"start": v(-10.87, 104.1) * mm, "mid": v(-10.55, 104) * mm, "end": v(-10.24, 104.14) * mm});
            skLineSegment(sketch, "E101.14.6", {"start": v(-10.24, 104.14) * mm, "end": v(-8.54, 105.72) * mm});
            skArc(sketch, "E101.14.7", {"start": v(-7.94, 105.78) * mm, "mid": v(-8.25, 105.85) * mm, "end": v(-8.54, 105.72) * mm});
            skLineSegment(sketch, "E101.14.8", {"start": v(-7.96, 105.8) * mm, "end": v(-7.94, 105.78) * mm});
            skLineSegment(sketch, "E101.15.0", {"start": v(-7.96, 105.8) * mm, "end": v(-7.98, 105.8) * mm});
            skArc(sketch, "E101.15.1", {"start": v(-7.73, 105.25) * mm, "mid": v(-7.76, 105.57) * mm, "end": v(-7.98, 105.8) * mm});
            skLineSegment(sketch, "E101.15.2", {"start": v(-8.25, 103) * mm, "end": v(-7.73, 105.25) * mm});
            skArc(sketch, "E101.15.3", {"start": v(-8.25, 103) * mm, "mid": v(-8.2, 102.66) * mm, "end": v(-7.97, 102.43) * mm});
            skArc(sketch, "E101.15.4", {"start": v(-7.97, 102.43) * mm, "mid": v(-7.95, 102.42) * mm, "end": v(-7.94, 102.4) * mm});
            skArc(sketch, "E101.15.5", {"start": v(-7.94, 102.4) * mm, "mid": v(-7.6, 102.38) * mm, "end": v(-7.33, 102.56) * mm});
            skLineSegment(sketch, "E101.15.6", {"start": v(-7.33, 102.56) * mm, "end": v(-5.93, 104.41) * mm});
            skArc(sketch, "E101.15.7", {"start": v(-5.35, 104.58) * mm, "mid": v(-5.67, 104.6) * mm, "end": v(-5.93, 104.41) * mm});
            skLineSegment(sketch, "E101.15.8", {"start": v(-5.37, 104.59) * mm, "end": v(-5.35, 104.58) * mm});
            skLineSegment(sketch, "E101.16.0", {"start": v(-5.37, 104.59) * mm, "end": v(-5.39, 104.6) * mm});
            skArc(sketch, "E101.16.1", {"start": v(-5.05, 104.1) * mm, "mid": v(-5.13, 104.4) * mm, "end": v(-5.39, 104.6) * mm});
            skLineSegment(sketch, "E101.16.2", {"start": v(-5.16, 101.77) * mm, "end": v(-5.05, 104.1) * mm});
            skArc(sketch, "E101.16.3", {"start": v(-5.16, 101.77) * mm, "mid": v(-5.07, 101.45) * mm, "end": v(-4.8, 101.27) * mm});
            skArc(sketch, "E101.16.4", {"start": v(-4.8, 101.27) * mm, "mid": v(-4.78, 101.26) * mm, "end": v(-4.76, 101.26) * mm});
            skArc(sketch, "E101.16.5", {"start": v(-4.76, 101.26) * mm, "mid": v(-4.43, 101.28) * mm, "end": v(-4.19, 101.51) * mm});
            skLineSegment(sketch, "E101.16.6", {"start": v(-4.19, 101.51) * mm, "end": v(-3.13, 103.58) * mm});
            skArc(sketch, "E101.16.7", {"start": v(-2.58, 103.84) * mm, "mid": v(-2.9, 103.8) * mm, "end": v(-3.13, 103.58) * mm});
            skLineSegment(sketch, "E101.16.8", {"start": v(-2.6, 103.85) * mm, "end": v(-2.58, 103.84) * mm});
            skLineSegment(sketch, "E101.17.0", {"start": v(-2.6, 103.85) * mm, "end": v(-2.62, 103.85) * mm});
            skArc(sketch, "E101.17.1", {"start": v(-2.2, 103.42) * mm, "mid": v(-2.34, 103.7) * mm, "end": v(-2.62, 103.85) * mm});
            skLineSegment(sketch, "E101.17.2", {"start": v(-1.92, 101.11) * mm, "end": v(-2.2, 103.42) * mm});
            skArc(sketch, "E101.17.3", {"start": v(-1.92, 101.11) * mm, "mid": v(-1.77, 100.81) * mm, "end": v(-1.47, 100.68) * mm});
            skArc(sketch, "E101.17.4", {"start": v(-1.47, 100.68) * mm, "mid": v(-1.45, 100.67) * mm, "end": v(-1.43, 100.67) * mm});
            skArc(sketch, "E101.17.5", {"start": v(-1.43, 100.67) * mm, "mid": v(-1.1, 100.76) * mm, "end": v(-0.9, 101.02) * mm});
            skLineSegment(sketch, "E101.17.6", {"start": v(-0.9, 101.02) * mm, "end": v(-0.22, 103.24) * mm});
            skArc(sketch, "E101.17.7", {"start": v(0.26, 103.6) * mm, "mid": v(-0.04, 103.5) * mm, "end": v(-0.22, 103.24) * mm});
            skLineSegment(sketch, "E101.17.8", {"start": v(0.24, 103.6) * mm, "end": v(0.26, 103.6) * mm});
            skLineSegment(sketch, "E101.18.0", {"start": v(0.24, 103.6) * mm, "end": v(0.22, 103.6) * mm});
            skArc(sketch, "E101.18.1", {"start": v(0.71, 103.24) * mm, "mid": v(0.53, 103.5) * mm, "end": v(0.22, 103.6) * mm});
            skLineSegment(sketch, "E101.18.2", {"start": v(1.4, 101.02) * mm, "end": v(0.71, 103.24) * mm});
            skArc(sketch, "E101.18.3", {"start": v(1.4, 101.02) * mm, "mid": v(1.6, 100.76) * mm, "end": v(1.92, 100.67) * mm});
            skArc(sketch, "E101.18.4", {"start": v(1.92, 100.67) * mm, "mid": v(1.93, 100.67) * mm, "end": v(1.95, 100.68) * mm});
            skArc(sketch, "E101.18.5", {"start": v(1.95, 100.68) * mm, "mid": v(2.26, 100.81) * mm, "end": v(2.4, 101.11) * mm});
            skLineSegment(sketch, "E101.18.6", {"start": v(2.4, 101.11) * mm, "end": v(2.7, 103.42) * mm});
            skArc(sketch, "E101.18.7", {"start": v(3.11, 103.85) * mm, "mid": v(2.83, 103.7) * mm, "end": v(2.7, 103.42) * mm});
            skLineSegment(sketch, "E101.18.8", {"start": v(3.1, 103.85) * mm, "end": v(3.11, 103.85) * mm});
            skLineSegment(sketch, "E101.19.0", {"start": v(3.1, 103.85) * mm, "end": v(3.07, 103.84) * mm});
            skArc(sketch, "E101.19.1", {"start": v(3.62, 103.58) * mm, "mid": v(3.39, 103.8) * mm, "end": v(3.07, 103.84) * mm});
            skLineSegment(sketch, "E101.19.2", {"start": v(4.67, 101.51) * mm, "end": v(3.62, 103.58) * mm});
            skArc(sketch, "E101.19.3", {"start": v(4.67, 101.51) * mm, "mid": v(4.92, 101.28) * mm, "end": v(5.25, 101.26) * mm});
            skArc(sketch, "E101.19.4", {"start": v(5.25, 101.26) * mm, "mid": v(5.27, 101.26) * mm, "end": v(5.28, 101.27) * mm});
            skArc(sketch, "E101.19.5", {"start": v(5.28, 101.27) * mm, "mid": v(5.56, 101.45) * mm, "end": v(5.65, 101.77) * mm});
            skLineSegment(sketch, "E101.19.6", {"start": v(5.65, 101.77) * mm, "end": v(5.53, 104.1) * mm});
            skArc(sketch, "E101.19.7", {"start": v(5.87, 104.6) * mm, "mid": v(5.62, 104.4) * mm, "end": v(5.53, 104.1) * mm});
            skLineSegment(sketch, "E101.19.8", {"start": v(5.85, 104.59) * mm, "end": v(5.87, 104.6) * mm});
            skLineSegment(sketch, "E101.20.0", {"start": v(5.85, 104.59) * mm, "end": v(5.84, 104.58) * mm});
            skArc(sketch, "E101.20.1", {"start": v(6.42, 104.41) * mm, "mid": v(6.15, 104.6) * mm, "end": v(5.84, 104.58) * mm});
            skLineSegment(sketch, "E101.20.2", {"start": v(7.82, 102.56) * mm, "end": v(6.42, 104.41) * mm});
            skArc(sketch, "E101.20.3", {"start": v(7.82, 102.56) * mm, "mid": v(8.1, 102.38) * mm, "end": v(8.43, 102.4) * mm});
            skArc(sketch, "E101.20.4", {"start": v(8.43, 102.4) * mm, "mid": v(8.44, 102.42) * mm, "end": v(8.46, 102.43) * mm});
            skArc(sketch, "E101.20.5", {"start": v(8.46, 102.43) * mm, "mid": v(8.7, 102.66) * mm, "end": v(8.74, 103) * mm});
            skLineSegment(sketch, "E101.20.6", {"start": v(8.74, 103) * mm, "end": v(8.22, 105.25) * mm});
            skArc(sketch, "E101.20.7", {"start": v(8.46, 105.8) * mm, "mid": v(8.25, 105.57) * mm, "end": v(8.22, 105.25) * mm});
            skLineSegment(sketch, "E101.20.8", {"start": v(8.45, 105.8) * mm, "end": v(8.46, 105.8) * mm});
            skLineSegment(sketch, "E101.21.0", {"start": v(8.45, 105.8) * mm, "end": v(8.43, 105.78) * mm});
            skArc(sketch, "E101.21.1", {"start": v(9.03, 105.72) * mm, "mid": v(8.74, 105.85) * mm, "end": v(8.43, 105.78) * mm});
            skLineSegment(sketch, "E101.21.2", {"start": v(10.73, 104.14) * mm, "end": v(9.03, 105.72) * mm});
            skArc(sketch, "E101.21.3", {"start": v(10.73, 104.14) * mm, "mid": v(11.04, 104) * mm, "end": v(11.36, 104.1) * mm});
            skArc(sketch, "E101.21.4", {"start": v(11.36, 104.1) * mm, "mid": v(11.37, 104.1) * mm, "end": v(11.39, 104.12) * mm});
            skArc(sketch, "E101.21.5", {"start": v(11.39, 104.12) * mm, "mid": v(11.58, 104.4) * mm, "end": v(11.56, 104.72) * mm});
            skLineSegment(sketch, "E101.21.6", {"start": v(11.56, 104.72) * mm, "end": v(10.66, 106.86) * mm});
            skArc(sketch, "E101.21.7", {"start": v(10.8, 107.45) * mm, "mid": v(10.63, 107.18) * mm, "end": v(10.66, 106.86) * mm});
            skLineSegment(sketch, "E101.21.8", {"start": v(10.79, 107.43) * mm, "end": v(10.8, 107.45) * mm});
            skLineSegment(sketch, "E101.22.0", {"start": v(10.79, 107.43) * mm, "end": v(10.77, 107.42) * mm});
            skArc(sketch, "E101.22.1", {"start": v(11.37, 107.46) * mm, "mid": v(11.07, 107.54) * mm, "end": v(10.77, 107.42) * mm});
            skLineSegment(sketch, "E101.22.2", {"start": v(13.32, 106.2) * mm, "end": v(11.37, 107.46) * mm});
            skArc(sketch, "E101.22.3", {"start": v(13.32, 106.2) * mm, "mid": v(13.65, 106.13) * mm, "end": v(13.95, 106.27) * mm});
            skArc(sketch, "E101.22.4", {"start": v(13.95, 106.27) * mm, "mid": v(13.96, 106.28) * mm, "end": v(13.97, 106.3) * mm});
            skArc(sketch, "E101.22.5", {"start": v(13.97, 106.3) * mm, "mid": v(14.12, 106.6) * mm, "end": v(14.04, 106.92) * mm});
            skLineSegment(sketch, "E101.22.6", {"start": v(14.04, 106.92) * mm, "end": v(12.78, 108.87) * mm});
            skArc(sketch, "E101.22.7", {"start": v(12.82, 109.47) * mm, "mid": v(12.7, 109.18) * mm, "end": v(12.78, 108.87) * mm});
            skLineSegment(sketch, "E101.22.8", {"start": v(12.81, 109.46) * mm, "end": v(12.82, 109.47) * mm});
            skLineSegment(sketch, "E101.23.0", {"start": v(12.81, 109.46) * mm, "end": v(12.8, 109.44) * mm});
            skArc(sketch, "E101.23.1", {"start": v(13.38, 109.59) * mm, "mid": v(13.07, 109.61) * mm, "end": v(12.8, 109.44) * mm});
            skLineSegment(sketch, "E101.23.2", {"start": v(15.52, 108.68) * mm, "end": v(13.38, 109.59) * mm});
            skArc(sketch, "E101.23.3", {"start": v(15.52, 108.68) * mm, "mid": v(15.85, 108.66) * mm, "end": v(16.12, 108.86) * mm});
            skArc(sketch, "E101.23.4", {"start": v(16.12, 108.86) * mm, "mid": v(16.14, 108.87) * mm, "end": v(16.15, 108.89) * mm});
            skArc(sketch, "E101.23.5", {"start": v(16.15, 108.89) * mm, "mid": v(16.24, 109.2) * mm, "end": v(16.1, 109.51) * mm});
            skLineSegment(sketch, "E101.23.6", {"start": v(16.1, 109.51) * mm, "end": v(14.52, 111.22) * mm});
            skArc(sketch, "E101.23.7", {"start": v(14.46, 111.82) * mm, "mid": v(14.4, 111.5) * mm, "end": v(14.52, 111.22) * mm});
            skLineSegment(sketch, "E101.23.8", {"start": v(14.45, 111.8) * mm, "end": v(14.46, 111.82) * mm});
            skLineSegment(sketch, "E101.24.0", {"start": v(14.45, 111.8) * mm, "end": v(14.44, 111.78) * mm});
            skArc(sketch, "E101.24.1", {"start": v(15, 112.03) * mm, "mid": v(14.67, 112) * mm, "end": v(14.44, 111.78) * mm});
            skLineSegment(sketch, "E101.24.2", {"start": v(17.25, 111.5) * mm, "end": v(15, 112.03) * mm});
            skArc(sketch, "E101.24.3", {"start": v(17.25, 111.5) * mm, "mid": v(17.58, 111.55) * mm, "end": v(17.82, 111.78) * mm});
            skArc(sketch, "E101.24.4", {"start": v(17.82, 111.78) * mm, "mid": v(17.83, 111.8) * mm, "end": v(17.83, 111.82) * mm});
            skArc(sketch, "E101.24.5", {"start": v(17.83, 111.82) * mm, "mid": v(17.87, 112.15) * mm, "end": v(17.68, 112.43) * mm});
            skLineSegment(sketch, "E101.24.6", {"start": v(17.68, 112.43) * mm, "end": v(15.83, 113.83) * mm});
            skArc(sketch, "E101.24.7", {"start": v(15.67, 114.4) * mm, "mid": v(15.65, 114.1) * mm, "end": v(15.83, 113.83) * mm});
            skLineSegment(sketch, "E101.24.8", {"start": v(15.66, 114.39) * mm, "end": v(15.67, 114.4) * mm});
            skLineSegment(sketch, "E101.25.0", {"start": v(15.66, 114.39) * mm, "end": v(15.65, 114.37) * mm});
            skArc(sketch, "E101.25.1", {"start": v(16.15, 114.7) * mm, "mid": v(15.84, 114.62) * mm, "end": v(15.65, 114.37) * mm});
            skLineSegment(sketch, "E101.25.2", {"start": v(18.47, 114.6) * mm, "end": v(16.15, 114.7) * mm});
            skArc(sketch, "E101.25.3", {"start": v(18.47, 114.6) * mm, "mid": v(18.79, 114.69) * mm, "end": v(18.98, 114.96) * mm});
            skArc(sketch, "E101.25.4", {"start": v(18.98, 114.96) * mm, "mid": v(18.98, 114.98) * mm, "end": v(18.99, 115) * mm});
            skArc(sketch, "E101.25.5", {"start": v(18.99, 115) * mm, "mid": v(18.96, 115.33) * mm, "end": v(18.73, 115.57) * mm});
            skLineSegment(sketch, "E101.25.6", {"start": v(18.73, 115.57) * mm, "end": v(16.67, 116.63) * mm});
            skArc(sketch, "E101.25.7", {"start": v(16.4, 117.17) * mm, "mid": v(16.44, 116.86) * mm, "end": v(16.67, 116.63) * mm});
            skLineSegment(sketch, "E101.25.8", {"start": v(16.4, 117.15) * mm, "end": v(16.4, 117.17) * mm});
            skLineSegment(sketch, "E101.26.0", {"start": v(16.4, 117.15) * mm, "end": v(16.4, 117.13) * mm});
            skArc(sketch, "E101.26.1", {"start": v(16.83, 117.55) * mm, "mid": v(16.54, 117.41) * mm, "end": v(16.4, 117.13) * mm});
            skLineSegment(sketch, "E101.26.2", {"start": v(19.13, 117.84) * mm, "end": v(16.83, 117.55) * mm});
            skArc(sketch, "E101.26.3", {"start": v(19.13, 117.84) * mm, "mid": v(19.43, 117.99) * mm, "end": v(19.57, 118.3) * mm});
            skArc(sketch, "E101.26.4", {"start": v(19.57, 118.3) * mm, "mid": v(19.57, 118.3) * mm, "end": v(19.57, 118.33) * mm});
            skArc(sketch, "E101.26.5", {"start": v(19.57, 118.33) * mm, "mid": v(19.49, 118.65) * mm, "end": v(19.22, 118.85) * mm});
            skLineSegment(sketch, "E101.26.6", {"start": v(19.22, 118.85) * mm, "end": v(17, 119.53) * mm});
            skArc(sketch, "E101.26.7", {"start": v(16.65, 120.02) * mm, "mid": v(16.74, 119.72) * mm, "end": v(17, 119.53) * mm});
            skLineSegment(sketch, "E101.26.8", {"start": v(16.65, 120) * mm, "end": v(16.65, 120.02) * mm});
            skLineSegment(sketch, "E101.27.0", {"start": v(16.65, 120) * mm, "end": v(16.65, 119.98) * mm});
            skArc(sketch, "E101.27.1", {"start": v(17, 120.47) * mm, "mid": v(16.74, 120.28) * mm, "end": v(16.65, 119.98) * mm});
            skLineSegment(sketch, "E101.27.2", {"start": v(19.22, 121.15) * mm, "end": v(17, 120.47) * mm});
            skArc(sketch, "E101.27.3", {"start": v(19.22, 121.15) * mm, "mid": v(19.49, 121.35) * mm, "end": v(19.57, 121.67) * mm});
            skArc(sketch, "E101.27.4", {"start": v(19.57, 121.67) * mm, "mid": v(19.57, 121.7) * mm, "end": v(19.57, 121.7) * mm});
            skArc(sketch, "E101.27.5", {"start": v(19.57, 121.7) * mm, "mid": v(19.43, 122.01) * mm, "end": v(19.13, 122.16) * mm});
            skLineSegment(sketch, "E101.27.6", {"start": v(19.13, 122.16) * mm, "end": v(16.83, 122.45) * mm});
            skArc(sketch, "E101.27.7", {"start": v(16.4, 122.87) * mm, "mid": v(16.54, 122.59) * mm, "end": v(16.83, 122.45) * mm});
            skLineSegment(sketch, "E101.27.8", {"start": v(16.4, 122.85) * mm, "end": v(16.4, 122.87) * mm});
            skLineSegment(sketch, "E101.28.0", {"start": v(16.4, 122.85) * mm, "end": v(16.4, 122.83) * mm});
            skArc(sketch, "E101.28.1", {"start": v(16.67, 123.37) * mm, "mid": v(16.44, 123.14) * mm, "end": v(16.4, 122.83) * mm});
            skLineSegment(sketch, "E101.28.2", {"start": v(18.73, 124.43) * mm, "end": v(16.67, 123.37) * mm});
            skArc(sketch, "E101.28.3", {"start": v(18.73, 124.43) * mm, "mid": v(18.96, 124.67) * mm, "end": v(18.99, 125) * mm});
            skArc(sketch, "E101.28.4", {"start": v(18.99, 125) * mm, "mid": v(18.98, 125.02) * mm, "end": v(18.98, 125.04) * mm});
            skArc(sketch, "E101.28.5", {"start": v(18.98, 125.04) * mm, "mid": v(18.79, 125.31) * mm, "end": v(18.47, 125.4) * mm});
            skLineSegment(sketch, "E101.28.6", {"start": v(18.47, 125.4) * mm, "end": v(16.15, 125.3) * mm});
            skArc(sketch, "E101.28.7", {"start": v(15.65, 125.63) * mm, "mid": v(15.84, 125.38) * mm, "end": v(16.15, 125.3) * mm});
            skLineSegment(sketch, "E101.28.8", {"start": v(15.66, 125.61) * mm, "end": v(15.65, 125.63) * mm});
            skLineSegment(sketch, "E101.29.0", {"start": v(15.66, 125.61) * mm, "end": v(15.67, 125.6) * mm});
            skArc(sketch, "E101.29.1", {"start": v(15.83, 126.17) * mm, "mid": v(15.65, 125.9) * mm, "end": v(15.67, 125.6) * mm});
            skLineSegment(sketch, "E101.29.2", {"start": v(17.68, 127.57) * mm, "end": v(15.83, 126.17) * mm});
            skArc(sketch, "E101.29.3", {"start": v(17.68, 127.57) * mm, "mid": v(17.87, 127.85) * mm, "end": v(17.83, 128.18) * mm});
            skArc(sketch, "E101.29.4", {"start": v(17.83, 128.18) * mm, "mid": v(17.83, 128.2) * mm, "end": v(17.82, 128.22) * mm});
            skArc(sketch, "E101.29.5", {"start": v(17.82, 128.22) * mm, "mid": v(17.58, 128.45) * mm, "end": v(17.25, 128.5) * mm});
            skLineSegment(sketch, "E101.29.6", {"start": v(17.25, 128.5) * mm, "end": v(15, 127.97) * mm});
            skArc(sketch, "E101.29.7", {"start": v(14.44, 128.22) * mm, "mid": v(14.67, 128) * mm, "end": v(15, 127.97) * mm});
            skLineSegment(sketch, "E101.29.8", {"start": v(14.45, 128.2) * mm, "end": v(14.44, 128.22) * mm});
            skLineSegment(sketch, "E101.30.0", {"start": v(14.45, 128.2) * mm, "end": v(14.46, 128.18) * mm});
            skArc(sketch, "E101.30.1", {"start": v(14.52, 128.78) * mm, "mid": v(14.4, 128.5) * mm, "end": v(14.46, 128.18) * mm});
            skLineSegment(sketch, "E101.30.2", {"start": v(16.1, 130.49) * mm, "end": v(14.52, 128.78) * mm});
            skArc(sketch, "E101.30.3", {"start": v(16.1, 130.49) * mm, "mid": v(16.24, 130.8) * mm, "end": v(16.15, 131.11) * mm});
            skArc(sketch, "E101.30.4", {"start": v(16.15, 131.11) * mm, "mid": v(16.14, 131.13) * mm, "end": v(16.12, 131.14) * mm});
            skArc(sketch, "E101.30.5", {"start": v(16.12, 131.14) * mm, "mid": v(15.85, 131.34) * mm, "end": v(15.52, 131.32) * mm});
            skLineSegment(sketch, "E101.30.6", {"start": v(15.52, 131.32) * mm, "end": v(13.38, 130.41) * mm});
            skArc(sketch, "E101.30.7", {"start": v(12.8, 130.56) * mm, "mid": v(13.07, 130.39) * mm, "end": v(13.38, 130.41) * mm});
            skLineSegment(sketch, "E101.30.8", {"start": v(12.81, 130.54) * mm, "end": v(12.8, 130.56) * mm});
            skLineSegment(sketch, "E101.31.0", {"start": v(12.81, 130.54) * mm, "end": v(12.82, 130.53) * mm});
            skArc(sketch, "E101.31.1", {"start": v(12.78, 131.13) * mm, "mid": v(12.7, 130.82) * mm, "end": v(12.82, 130.53) * mm});
            skLineSegment(sketch, "E101.31.2", {"start": v(14.04, 133.08) * mm, "end": v(12.78, 131.13) * mm});
            skArc(sketch, "E101.31.3", {"start": v(14.04, 133.08) * mm, "mid": v(14.12, 133.4) * mm, "end": v(13.97, 133.7) * mm});
            skArc(sketch, "E101.31.4", {"start": v(13.97, 133.7) * mm, "mid": v(13.96, 133.72) * mm, "end": v(13.95, 133.73) * mm});
            skArc(sketch, "E101.31.5", {"start": v(13.95, 133.73) * mm, "mid": v(13.65, 133.87) * mm, "end": v(13.32, 133.8) * mm});
            skLineSegment(sketch, "E101.31.6", {"start": v(13.32, 133.8) * mm, "end": v(11.37, 132.54) * mm});
            skArc(sketch, "E101.31.7", {"start": v(10.77, 132.58) * mm, "mid": v(11.07, 132.46) * mm, "end": v(11.37, 132.54) * mm});
            skLineSegment(sketch, "E101.31.8", {"start": v(10.79, 132.57) * mm, "end": v(10.77, 132.58) * mm});
            skLineSegment(sketch, "E101.32.0", {"start": v(10.79, 132.57) * mm, "end": v(10.8, 132.55) * mm});
            skArc(sketch, "E101.32.1", {"start": v(10.66, 133.14) * mm, "mid": v(10.63, 132.82) * mm, "end": v(10.8, 132.55) * mm});
            skLineSegment(sketch, "E101.32.2", {"start": v(11.56, 135.28) * mm, "end": v(10.66, 133.14) * mm});
            skArc(sketch, "E101.32.3", {"start": v(11.56, 135.28) * mm, "mid": v(11.58, 135.6) * mm, "end": v(11.39, 135.88) * mm});
            skArc(sketch, "E101.32.4", {"start": v(11.39, 135.88) * mm, "mid": v(11.37, 135.9) * mm, "end": v(11.36, 135.9) * mm});
            skArc(sketch, "E101.32.5", {"start": v(11.36, 135.9) * mm, "mid": v(11.04, 136) * mm, "end": v(10.73, 135.86) * mm});
            skLineSegment(sketch, "E101.32.6", {"start": v(10.73, 135.86) * mm, "end": v(9.03, 134.28) * mm});
            skArc(sketch, "E101.32.7", {"start": v(8.43, 134.22) * mm, "mid": v(8.74, 134.15) * mm, "end": v(9.03, 134.28) * mm});
            skLineSegment(sketch, "E101.32.8", {"start": v(8.45, 134.2) * mm, "end": v(8.43, 134.22) * mm});
            skLineSegment(sketch, "E101.33.0", {"start": v(8.45, 134.2) * mm, "end": v(8.46, 134.2) * mm});
            skArc(sketch, "E101.33.1", {"start": v(8.22, 134.75) * mm, "mid": v(8.25, 134.43) * mm, "end": v(8.46, 134.2) * mm});
            skLineSegment(sketch, "E101.33.2", {"start": v(8.74, 137) * mm, "end": v(8.22, 134.75) * mm});
            skArc(sketch, "E101.33.3", {"start": v(8.74, 137) * mm, "mid": v(8.7, 137.34) * mm, "end": v(8.46, 137.57) * mm});
            skArc(sketch, "E101.33.4", {"start": v(8.46, 137.57) * mm, "mid": v(8.44, 137.58) * mm, "end": v(8.43, 137.6) * mm});
            skArc(sketch, "E101.33.5", {"start": v(8.43, 137.6) * mm, "mid": v(8.1, 137.62) * mm, "end": v(7.82, 137.44) * mm});
            skLineSegment(sketch, "E101.33.6", {"start": v(7.82, 137.44) * mm, "end": v(6.42, 135.59) * mm});
            skArc(sketch, "E101.33.7", {"start": v(5.84, 135.42) * mm, "mid": v(6.15, 135.4) * mm, "end": v(6.42, 135.59) * mm});
            skLineSegment(sketch, "E101.33.8", {"start": v(5.85, 135.41) * mm, "end": v(5.84, 135.42) * mm});
            skLineSegment(sketch, "E101.34.0", {"start": v(5.85, 135.41) * mm, "end": v(5.87, 135.4) * mm});
            skArc(sketch, "E101.34.1", {"start": v(5.53, 135.9) * mm, "mid": v(5.62, 135.6) * mm, "end": v(5.87, 135.4) * mm});
            skLineSegment(sketch, "E101.34.2", {"start": v(5.65, 138.23) * mm, "end": v(5.53, 135.9) * mm});
            skArc(sketch, "E101.34.3", {"start": v(5.65, 138.23) * mm, "mid": v(5.56, 138.55) * mm, "end": v(5.28, 138.73) * mm});
            skArc(sketch, "E101.34.4", {"start": v(5.28, 138.73) * mm, "mid": v(5.27, 138.74) * mm, "end": v(5.25, 138.74) * mm});
            skArc(sketch, "E101.34.5", {"start": v(5.25, 138.74) * mm, "mid": v(4.92, 138.72) * mm, "end": v(4.67, 138.49) * mm});
            skLineSegment(sketch, "E101.34.6", {"start": v(4.67, 138.49) * mm, "end": v(3.62, 136.42) * mm});
            skArc(sketch, "E101.34.7", {"start": v(3.07, 136.16) * mm, "mid": v(3.39, 136.2) * mm, "end": v(3.62, 136.42) * mm});
            skLineSegment(sketch, "E101.34.8", {"start": v(3.1, 136.15) * mm, "end": v(3.07, 136.16) * mm});
            skLineSegment(sketch, "E101.35.0", {"start": v(3.1, 136.15) * mm, "end": v(3.11, 136.15) * mm});
            skArc(sketch, "E101.35.1", {"start": v(2.7, 136.58) * mm, "mid": v(2.83, 136.3) * mm, "end": v(3.11, 136.15) * mm});
            skLineSegment(sketch, "E101.35.2", {"start": v(2.4, 138.89) * mm, "end": v(2.7, 136.58) * mm});
            skArc(sketch, "E101.35.3", {"start": v(2.4, 138.89) * mm, "mid": v(2.26, 139.19) * mm, "end": v(1.95, 139.32) * mm});
            skArc(sketch, "E101.35.4", {"start": v(1.95, 139.32) * mm, "mid": v(1.93, 139.33) * mm, "end": v(1.92, 139.33) * mm});
            skArc(sketch, "E101.35.5", {"start": v(1.92, 139.33) * mm, "mid": v(1.6, 139.24) * mm, "end": v(1.4, 138.98) * mm});
            skLineSegment(sketch, "E101.35.6", {"start": v(1.4, 138.98) * mm, "end": v(0.71, 136.76) * mm});
            skArc(sketch, "E101.35.7", {"start": v(0.22, 136.4) * mm, "mid": v(0.53, 136.5) * mm, "end": v(0.71, 136.76) * mm});
            skLineSegment(sketch, "E101.35.8", {"start": v(0.24, 136.4) * mm, "end": v(0.22, 136.4) * mm});
            skSolve(sketch);
        }
        {
            var Q0;
            Q0=qSketchRegion(id+"F6",true);
            extrude(context, id + "F7", {"entities" : qUnion([Q0]), "depth" : 2 * mm});
        }
        {
            var Q0;
            Q0=makeQuery(id+"F7.opExtrude","CAP_FACE",FACE,{"disambiguationData":[OSD([sQuery(id+"F6.wireOp",EDGE,"E80"),sQuery(id+"F6.wireOp",EDGE,"E82")])],"isStart":false});
            var sketch = newSketch(context, id + "F8", { "sketchPlane" : qUnion([Q0])});
            skLineSegment(sketch, "E102.rect.bottom", {"start": v(88.24, 114) * mm, "end": v(-89.76, 114) * mm});
            skLineSegment(sketch, "E102.rect.top", {"start": v(90.24, 126) * mm, "end": v(-87.76, 126) * mm});
            skLineSegment(sketch, "E102.rect.left", {"start": v(90.24, 120) * mm, "end": v(90.24, 126) * mm});
            skLineSegment(sketch, "E102.rect.right", {"start": v(-89.76, 114) * mm, "end": v(-89.76, 120) * mm});
            skPoint(sketch, "E102.rect.middle", {"position": v(0.24, 120) * mm});
            skCircle(sketch, "E103", {"center": v(0.24, 120) * mm, "radius": 1.5 * mm});
            skLineSegment(sketch, "E104", {"start": v(-89.76, 120) * mm, "end": v(-87.76, 120) * mm});
            skLineSegment(sketch, "E105", {"start": v(-87.76, 120) * mm, "end": v(-87.76, 126) * mm});
            skLineSegment(sketch, "E106", {"start": v(90.24, 120) * mm, "end": v(88.24, 120) * mm});
            skPoint(sketch, "E106.endSnap0", {"position": v(90.24, 120) * mm});
            skLineSegment(sketch, "E107", {"start": v(88.24, 120) * mm, "end": v(88.24, 114) * mm});
            skPoint(sketch, "E108.orphan", {"position": v(-89.76, 126) * mm});
            skPoint(sketch, "E109.orphan", {"position": v(90.24, 114) * mm});
            skLineSegment(sketch, "E110", {"start": v(-89.76, 126) * mm, "end": v(90.24, 114) * mm, "construction": true});
            skLineSegment(sketch, "E111", {"start": v(0.24, 120) * mm, "end": v(-89.76, 120) * mm, "construction": true});
            skCircle(sketch, "E112", {"center": v(-71.76, 120) * mm, "radius": 1.5 * mm});
            skCircle(sketch, "E113", {"center": v(-35.76, 120) * mm, "radius": 1.5 * mm});
            skSolve(sketch);
        }
        {
            var Q0;
            Q0=qSketchRegion(id+"F8",true);
            extrude(context, id + "F9", {"entities" : qUnion([Q0]), "depth" : 2 * mm});
        }
        {
            var Q0;
            Q0=makeQuery(id+"F9.opExtrude","SWEPT_FACE",FACE,{"disambiguationData":[OSD([sQuery(id+"F8.wireOp",EDGE,"E102.rect.right")])]});
            var sketch = newSketch(context, id + "F10", { "sketchPlane" : qUnion([Q0])});
            skLineSegment(sketch, "E114.bottom", {"start": v(-91, 114) * mm, "end": v(87, 114) * mm});
            skLineSegment(sketch, "E114.top", {"start": v(-93, 126) * mm, "end": v(85, 126) * mm});
            skLineSegment(sketch, "E114.left", {"start": v(-93, 120) * mm, "end": v(-93, 126) * mm});
            skLineSegment(sketch, "E114.right", {"start": v(87, 114) * mm, "end": v(87, 120) * mm});
            skLineSegment(sketch, "E115.top", {"start": v(-93, 120) * mm, "end": v(-91, 120) * mm});
            skLineSegment(sketch, "E115.right", {"start": v(-91, 114) * mm, "end": v(-91, 120) * mm});
            skLineSegment(sketch, "E116.top", {"start": v(87, 120) * mm, "end": v(85, 120) * mm});
            skLineSegment(sketch, "E116.right", {"start": v(85, 126) * mm, "end": v(85, 120) * mm});
            skLineSegment(sketch, "E117", {"start": v(-93, 126) * mm, "end": v(87, 114) * mm, "construction": true});
            skCircle(sketch, "E118", {"center": v(-3, 120) * mm, "radius": 1.5 * mm});
            skLineSegment(sketch, "E119", {"start": v(-93, 120) * mm, "end": v(-3, 120) * mm, "construction": true});
            skCircle(sketch, "E120", {"center": v(-75, 120) * mm, "radius": 1.5 * mm});
            skCircle(sketch, "E121", {"center": v(-39, 120) * mm, "radius": 1.5 * mm});
            skSolve(sketch);
        }
        {
            var Q0;
            Q0=makeQuery(id+"F10.imprint","IMPRINT",FACE,{"disambiguationData":[TD([[makeQuery(id+"F10.imprint","IMPRINT",EDGE,{"derivedFrom":sQuery(id+"F10.wireOp",EDGE,"E114.bottom")}),1.0]])]});
            extrude(context, id + "F11", {"entities" : qUnion([Q0]), "oppositeDirection" : true, "depth" : 2 * mm});
        }
        {
            var Q0;
            Q0=makeQuery(id+"F11.opExtrude","SWEPT_FACE",FACE,{"disambiguationData":[OSD([sQuery(id+"F10.wireOp",EDGE,"E114.right")])]});
            var sketch = newSketch(context, id + "F12", { "sketchPlane" : qUnion([Q0])});
            skLineSegment(sketch, "E122.bottom", {"start": v(-87.76, 114) * mm, "end": v(76.24, 114) * mm});
            skLineSegment(sketch, "E122.top", {"start": v(-82, 126) * mm, "end": v(88.24, 126) * mm});
            skLineSegment(sketch, "E123.bottom", {"start": v(-89.76, 120) * mm, "end": v(-83.76, 120) * mm});
            skLineSegment(sketch, "E124.top", {"start": v(90.24, 120) * mm, "end": v(88.24, 120) * mm});
            skLineSegment(sketch, "E125", {"start": v(-82, 126) * mm, "end": v(-89.76, 126) * mm});
            skLineSegment(sketch, "E126", {"start": v(-89.76, 126) * mm, "end": v(-89.76, 120) * mm});
            skLineSegment(sketch, "E127", {"start": v(-83.76, 120) * mm, "end": v(-87.76, 114) * mm, "construction": true});
            skLineSegment(sketch, "E128", {"start": v(76.24, 114) * mm, "end": v(90.24, 114) * mm});
            skLineSegment(sketch, "E129", {"start": v(90.24, 114) * mm, "end": v(90.24, 120) * mm});
            skLineSegment(sketch, "E130", {"start": v(88.24, 120) * mm, "end": v(88.24, 126) * mm});
            skLineSegment(sketch, "E131", {"start": v(-89.76, 126) * mm, "end": v(90.24, 114) * mm, "construction": true});
            skCircle(sketch, "E132", {"center": v(0.24, 120) * mm, "radius": 1.5 * mm});
            skSolve(sketch);
        }
        {
            var Q0;
            Q0=makeQuery(id+"F12.imprint","IMPRINT",FACE,{"disambiguationData":[TD([[makeQuery(id+"F12.imprint","IMPRINT",EDGE,{"derivedFrom":sQuery(id+"F12.wireOp",EDGE,"E122.bottom")}),1.0]])]});
            extrude(context, id + "F13", {"entities" : qUnion([Q0]), "oppositeDirection" : true, "depth" : 2 * mm});
        }
        {
            var Q0;
            Q0=makeQuery(id+"F13.opExtrude","SWEPT_FACE",FACE,{"disambiguationData":[OSD([sQuery(id+"F12.wireOp",EDGE,"E129")])]});
            var sketch = newSketch(context, id + "F14", { "sketchPlane" : qUnion([Q0])});
            skLineSegment(sketch, "E133.bottom", {"start": v(-85, 114) * mm, "end": v(93, 114) * mm});
            skLineSegment(sketch, "E133.top", {"start": v(-87, 126) * mm, "end": v(91, 126) * mm});
            skLineSegment(sketch, "E133.left", {"start": v(-87, 120) * mm, "end": v(-87, 126) * mm});
            skLineSegment(sketch, "E133.right", {"start": v(93, 114) * mm, "end": v(93, 120) * mm});
            skLineSegment(sketch, "E134.bottom", {"start": v(-87, 120) * mm, "end": v(-85, 120) * mm});
            skLineSegment(sketch, "E134.right", {"start": v(-85, 120) * mm, "end": v(-85, 114) * mm});
            skLineSegment(sketch, "E135.top", {"start": v(93, 120) * mm, "end": v(91, 120) * mm});
            skLineSegment(sketch, "E135.right", {"start": v(91, 126) * mm, "end": v(91, 120) * mm});
            skLineSegment(sketch, "E136", {"start": v(-87, 126) * mm, "end": v(93, 114) * mm, "construction": true});
            skCircle(sketch, "E137", {"center": v(3, 120) * mm, "radius": 1.5 * mm});
            skSolve(sketch);
        }
        {
            var Q0;
            Q0=makeQuery(id+"F14.imprint","IMPRINT",FACE,{"disambiguationData":[TD([[makeQuery(id+"F14.imprint","IMPRINT",EDGE,{"derivedFrom":sQuery(id+"F14.wireOp",EDGE,"E133.bottom")}),1.0]])]});
            extrude(context, id + "F15", {"entities" : qUnion([Q0]), "oppositeDirection" : true, "depth" : 2 * mm});
        }
        {
            var Q0;
            Q0=makeQuery(id+"F11.opExtrude","CAP_FACE",FACE,{"disambiguationData":[OSD([sQuery(id+"F10.wireOp",EDGE,"E114.bottom"),sQuery(id+"F10.wireOp",EDGE,"E114.top"),sQuery(id+"F10.wireOp",EDGE,"E114.left"),sQuery(id+"F10.wireOp",EDGE,"E114.right"),sQuery(id+"F10.wireOp",EDGE,"E115.top"),sQuery(id+"F10.wireOp",EDGE,"E115.right"),sQuery(id+"F10.wireOp",EDGE,"E116.top"),sQuery(id+"F10.wireOp",EDGE,"E116.right"),sQuery(id+"F10.wireOp",EDGE,"E118")])],"isStart":false});
            var sketch = newSketch(context, id + "F16", { "sketchPlane" : qUnion([Q0])});
            skLineSegment(sketch, "E138.rect.bottom", {"start": v(-3, 204.76) * mm, "end": v(3, 204.76) * mm});
            skLineSegment(sketch, "E138.rect.top", {"start": v(3, 35.24) * mm, "end": v(9, 35.24) * mm});
            skLineSegment(sketch, "E138.rect.left", {"start": v(-3, 204.76) * mm, "end": v(-3, 37.24) * mm});
            skLineSegment(sketch, "E138.rect.right", {"start": v(9, 202.76) * mm, "end": v(9, 35.24) * mm});
            skPoint(sketch, "E138.rect.middle", {"position": v(3, 120) * mm});
            skPoint(sketch, "E139.oppositeSnap0", {"position": v(3, 204.76) * mm});
            skLineSegment(sketch, "E139.top", {"start": v(9, 202.76) * mm, "end": v(3, 202.76) * mm});
            skLineSegment(sketch, "E139.right", {"start": v(3, 204.76) * mm, "end": v(3, 202.76) * mm});
            skPoint(sketch, "E140.oppositeSnap0", {"position": v(3, 35.24) * mm});
            skLineSegment(sketch, "E140.top", {"start": v(-3, 37.24) * mm, "end": v(3, 37.24) * mm});
            skLineSegment(sketch, "E140.right", {"start": v(3, 35.24) * mm, "end": v(3, 37.24) * mm});
            skPoint(sketch, "E141.orphan", {"position": v(9, 204.76) * mm});
            skPoint(sketch, "E142.orphan", {"position": v(-3, 35.24) * mm});
            skCircle(sketch, "E143", {"center": v(3, 120) * mm, "radius": 1.5 * mm});
            skSolve(sketch);
        }
        {
            var Q0;
            Q0=qSketchRegion(id+"F16",true);
            extrude(context, id + "F17", {"entities" : qUnion([Q0]), "depth" : 2 * mm});
        }
        {
            var Q0;
            Q0=makeQuery(id+"F17.opExtrude","SWEPT_FACE",FACE,{"disambiguationData":[OSD([sQuery(id+"F16.wireOp",EDGE,"E138.rect.bottom")])]});
            var sketch = newSketch(context, id + "F18", { "sketchPlane" : qUnion([Q0])});
            skLineSegment(sketch, "E144.bottom", {"start": v(-3, -87.76) * mm, "end": v(-9, -87.76) * mm});
            skLineSegment(sketch, "E144.top", {"start": v(3, 81.76) * mm, "end": v(-3, 81.76) * mm});
            skLineSegment(sketch, "E144.left", {"start": v(3, -85.76) * mm, "end": v(3, 81.76) * mm});
            skLineSegment(sketch, "E144.right", {"start": v(-9, -87.76) * mm, "end": v(-9, 79.76) * mm});
            skLineSegment(sketch, "E145.top", {"start": v(3, -85.76) * mm, "end": v(-3, -85.76) * mm});
            skLineSegment(sketch, "E145.right", {"start": v(-3, -87.76) * mm, "end": v(-3, -85.76) * mm});
            skPoint(sketch, "E146.oppositeSnap0", {"position": v(-3, 81.76) * mm});
            skLineSegment(sketch, "E146.top", {"start": v(-9, 79.76) * mm, "end": v(-3, 79.76) * mm});
            skLineSegment(sketch, "E146.right", {"start": v(-3, 81.76) * mm, "end": v(-3, 79.76) * mm});
            skPoint(sketch, "E147.orphan", {"position": v(-9, 81.76) * mm});
            skLineSegment(sketch, "E148", {"start": v(-9, -87.76) * mm, "end": v(3, 81.76) * mm, "construction": true});
            skCircle(sketch, "E149", {"center": v(-3, -3) * mm, "radius": 2.5 * mm, "construction": true});
            skLineSegment(sketch, "E150.rect.bottom", {"start": v(-4.5, 0) * mm, "end": v(-1.5, 0) * mm});
            skLineSegment(sketch, "E150.rect.top", {"start": v(-4.5, -6) * mm, "end": v(-1.5, -6) * mm});
            skLineSegment(sketch, "E150.rect.left", {"start": v(-4.5, 0) * mm, "end": v(-4.5, -6) * mm});
            skLineSegment(sketch, "E150.rect.right", {"start": v(-1.5, 0) * mm, "end": v(-1.5, -6) * mm});
            skSolve(sketch);
        }
        {
            var Q0;
            Q0=makeQuery(id+"F18.imprint","IMPRINT",FACE,{"disambiguationData":[TD([[makeQuery(id+"F18.imprint","IMPRINT",EDGE,{"derivedFrom":sQuery(id+"F18.wireOp",EDGE,"E144.bottom")}),-1.0]])]});
            extrude(context, id + "F19", {"entities" : qUnion([Q0]), "oppositeDirection" : true, "depth" : 2 * mm});
        }
        {
            var Q0;
            Q0=makeQuery(id+"F19.opExtrude","SWEPT_FACE",FACE,{"disambiguationData":[OSD([sQuery(id+"F18.wireOp",EDGE,"E144.top")])]});
            var sketch = newSketch(context, id + "F20", { "sketchPlane" : qUnion([Q0])});
            skLineSegment(sketch, "E151.bottom", {"start": v(3, 204.76) * mm, "end": v(9, 204.76) * mm});
            skLineSegment(sketch, "E151.top", {"start": v(-3, 35.24) * mm, "end": v(3, 35.24) * mm});
            skLineSegment(sketch, "E151.left", {"start": v(-3, 202.76) * mm, "end": v(-3, 35.24) * mm});
            skLineSegment(sketch, "E151.right", {"start": v(9, 204.76) * mm, "end": v(9, 37.24) * mm});
            skLineSegment(sketch, "E152.top", {"start": v(-3, 202.76) * mm, "end": v(3, 202.76) * mm});
            skLineSegment(sketch, "E152.right", {"start": v(3, 204.76) * mm, "end": v(3, 202.76) * mm});
            skPoint(sketch, "E153.oppositeSnap0", {"position": v(3, 35.24) * mm});
            skLineSegment(sketch, "E153.top", {"start": v(9, 37.24) * mm, "end": v(3, 37.24) * mm});
            skLineSegment(sketch, "E153.right", {"start": v(3, 35.24) * mm, "end": v(3, 37.24) * mm});
            skPoint(sketch, "E154.orphan", {"position": v(9, 35.24) * mm});
            skLineSegment(sketch, "E155", {"start": v(9, 204.76) * mm, "end": v(-3, 35.24) * mm, "construction": true});
            skCircle(sketch, "E156", {"center": v(3, 120) * mm, "radius": 1.5 * mm});
            skSolve(sketch);
        }
        {
            var Q0;
            Q0=makeQuery(id+"F20.imprint","IMPRINT",FACE,{"disambiguationData":[TD([[makeQuery(id+"F20.imprint","IMPRINT",EDGE,{"derivedFrom":sQuery(id+"F20.wireOp",EDGE,"E151.bottom")}),-1.0]])]});
            extrude(context, id + "F21", {"entities" : qUnion([Q0]), "oppositeDirection" : true, "depth" : 2 * mm});
        }
        {
            var Q0;
            Q0=makeQuery(id+"F17.opExtrude","SWEPT_FACE",FACE,{"disambiguationData":[OSD([sQuery(id+"F16.wireOp",EDGE,"E138.rect.top")])]});
            var sketch = newSketch(context, id + "F22", { "sketchPlane" : qUnion([Q0])});
            skLineSegment(sketch, "E157.bottom", {"start": v(-3, 87.76) * mm, "end": v(3, 87.76) * mm});
            skLineSegment(sketch, "E157.top", {"start": v(-9, -81.76) * mm, "end": v(-3, -81.76) * mm});
            skLineSegment(sketch, "E157.left", {"start": v(-9, 85.76) * mm, "end": v(-9, -81.76) * mm});
            skLineSegment(sketch, "E157.right", {"start": v(3, 87.76) * mm, "end": v(3, -79.76) * mm});
            skLineSegment(sketch, "E158.top", {"start": v(-9, 85.76) * mm, "end": v(-3, 85.76) * mm});
            skLineSegment(sketch, "E158.right", {"start": v(-3, 87.76) * mm, "end": v(-3, 85.76) * mm});
            skPoint(sketch, "E159.oppositeSnap0", {"position": v(-3, -81.76) * mm});
            skLineSegment(sketch, "E159.top", {"start": v(3, -79.76) * mm, "end": v(-3, -79.76) * mm});
            skLineSegment(sketch, "E159.right", {"start": v(-3, -81.76) * mm, "end": v(-3, -79.76) * mm});
            skPoint(sketch, "E160.orphan", {"position": v(3, -81.76) * mm});
            skLineSegment(sketch, "E161", {"start": v(-9, 87.76) * mm, "end": v(3, -81.76) * mm, "construction": true});
            skLineSegment(sketch, "E162.rect.bottom", {"start": v(-4.5, 6) * mm, "end": v(-1.5, 6) * mm});
            skLineSegment(sketch, "E162.rect.top", {"start": v(-4.5, 0) * mm, "end": v(-1.5, 0) * mm});
            skLineSegment(sketch, "E162.rect.left", {"start": v(-4.5, 6) * mm, "end": v(-4.5, 0) * mm});
            skLineSegment(sketch, "E162.rect.right", {"start": v(-1.5, 6) * mm, "end": v(-1.5, 0) * mm});
            skPoint(sketch, "E162.rect.middle", {"position": v(-3, 3) * mm});
            skSolve(sketch);
        }
        {
            var Q0;
            Q0=qSketchRegion(id+"F22",true);
            extrude(context, id + "F23", {"entities" : qUnion([Q0]), "operationType" : NewBodyOperationType.ADD, "oppositeDirection" : true, "depth" : 2 * mm});
        }
        {
            var Q0;
            Q0=makeQuery(id+"F9.opExtrude","CAP_FACE",FACE,{"disambiguationData":[OSD([sQuery(id+"F8.wireOp",EDGE,"E102.rect.bottom"),sQuery(id+"F8.wireOp",EDGE,"E102.rect.top"),sQuery(id+"F8.wireOp",EDGE,"E102.rect.left"),sQuery(id+"F8.wireOp",EDGE,"E102.rect.right"),sQuery(id+"F8.wireOp",EDGE,"E103"),sQuery(id+"F8.wireOp",EDGE,"E104"),sQuery(id+"F8.wireOp",EDGE,"E105"),sQuery(id+"F8.wireOp",EDGE,"E106"),sQuery(id+"F8.wireOp",EDGE,"E107"),sQuery(id+"F8.wireOp",EDGE,"E112")])],"isStart":true});
            var sketch = newSketch(context, id + "F24", { "sketchPlane" : qUnion([Q0])});
            skCircle(sketch, "E163", {"center": v(71.76, 120) * mm, "radius": 16.4 * mm, "construction": true});
            skCircle(sketch, "E164", {"center": v(71.76, 120) * mm, "radius": 19.4 * mm, "construction": true});
            skCircle(sketch, "E165", {"center": v(71.76, 120) * mm, "radius": 2.5 * mm});
            skLineSegment(sketch, "E166", {"start": v(71.76, 120) * mm, "end": v(71.76, 139.4) * mm, "construction": true});
            skLineSegment(sketch, "E167", {"start": v(71.76, 120) * mm, "end": v(70.07, 139.33) * mm, "construction": true});
            skLineSegment(sketch, "E168", {"start": v(71.76, 120) * mm, "end": v(70.49, 139.36) * mm, "construction": true});
            skLineSegment(sketch, "E169", {"start": v(71.76, 120) * mm, "end": v(70.9, 139.38) * mm, "construction": true});
            skLineSegment(sketch, "E170", {"start": v(71.76, 120) * mm, "end": v(71.33, 139.4) * mm, "construction": true});
            skLineSegment(sketch, "E171.MirrorCS", {"start": v(71.76, 120) * mm, "end": v(72.6, 139.38) * mm, "construction": true});
            skLineSegment(sketch, "E172.MirrorCS", {"start": v(71.76, 120) * mm, "end": v(73.02, 139.36) * mm, "construction": true});
            skLineSegment(sketch, "E173.MirrorCS", {"start": v(71.76, 120) * mm, "end": v(73.45, 139.33) * mm, "construction": true});
            skLineSegment(sketch, "E174.MirrorCS", {"start": v(71.76, 120) * mm, "end": v(72.18, 139.4) * mm, "construction": true});
            skArc(sketch, "E175", {"start": v(72.18, 139.4) * mm, "mid": v(71.76, 139.4) * mm, "end": v(71.33, 139.4) * mm});
            skLineSegment(sketch, "E176", {"start": v(72.18, 139.4) * mm, "end": v(72.83, 136.36) * mm});
            skLineSegment(sketch, "E177", {"start": v(71.33, 139.4) * mm, "end": v(70.68, 136.36) * mm});
            skLineSegment(sketch, "E178", {"start": v(72.83, 136.36) * mm, "end": v(73.19, 136.34) * mm});
            skPoint(sketch, "E179", {"position": v(70.33, 136.34) * mm});
            skLineSegment(sketch, "E180", {"start": v(70.68, 136.36) * mm, "end": v(70.33, 136.34) * mm});
            skLineSegment(sketch, "E181.1.0", {"start": v(67.97, 139.03) * mm, "end": v(67.86, 135.93) * mm});
            skLineSegment(sketch, "E181.1.1", {"start": v(67.86, 135.93) * mm, "end": v(67.51, 135.84) * mm});
            skLineSegment(sketch, "E181.1.2", {"start": v(68.8, 139.17) * mm, "end": v(69.97, 136.3) * mm});
            skLineSegment(sketch, "E181.1.3", {"start": v(69.97, 136.3) * mm, "end": v(70.33, 136.34) * mm});
            skArc(sketch, "E181.1.4", {"start": v(68.8, 139.17) * mm, "mid": v(68.39, 139.1) * mm, "end": v(67.97, 139.03) * mm});
            skLineSegment(sketch, "E181.2.0", {"start": v(64.72, 138.08) * mm, "end": v(65.15, 135.01) * mm});
            skLineSegment(sketch, "E181.2.1", {"start": v(65.15, 135.01) * mm, "end": v(64.83, 134.86) * mm});
            skLineSegment(sketch, "E181.2.2", {"start": v(65.52, 138.37) * mm, "end": v(67.17, 135.74) * mm});
            skLineSegment(sketch, "E181.2.3", {"start": v(67.17, 135.74) * mm, "end": v(67.51, 135.84) * mm});
            skArc(sketch, "E181.2.4", {"start": v(65.52, 138.37) * mm, "mid": v(65.12, 138.23) * mm, "end": v(64.72, 138.08) * mm});
            skLineSegment(sketch, "E181.3.0", {"start": v(61.7, 136.59) * mm, "end": v(62.64, 133.64) * mm});
            skLineSegment(sketch, "E181.3.1", {"start": v(62.64, 133.64) * mm, "end": v(62.35, 133.43) * mm});
            skLineSegment(sketch, "E181.3.2", {"start": v(62.42, 137) * mm, "end": v(64.5, 134.7) * mm});
            skLineSegment(sketch, "E181.3.3", {"start": v(64.5, 134.7) * mm, "end": v(64.83, 134.86) * mm});
            skArc(sketch, "E181.3.4", {"start": v(62.42, 137) * mm, "mid": v(62.06, 136.8) * mm, "end": v(61.7, 136.59) * mm});
            skLineSegment(sketch, "E181.4.0", {"start": v(58.96, 134.59) * mm, "end": v(60.42, 131.85) * mm});
            skLineSegment(sketch, "E181.4.1", {"start": v(60.42, 131.85) * mm, "end": v(60.16, 131.6) * mm});
            skLineSegment(sketch, "E181.4.2", {"start": v(59.61, 135.13) * mm, "end": v(62.06, 133.23) * mm});
            skLineSegment(sketch, "E181.4.3", {"start": v(62.06, 133.23) * mm, "end": v(62.35, 133.43) * mm});
            skArc(sketch, "E181.4.4", {"start": v(59.61, 135.13) * mm, "mid": v(59.29, 134.86) * mm, "end": v(58.96, 134.59) * mm});
            skLineSegment(sketch, "E181.5.0", {"start": v(56.63, 132.14) * mm, "end": v(58.53, 129.7) * mm});
            skLineSegment(sketch, "E181.5.1", {"start": v(58.53, 129.7) * mm, "end": v(58.32, 129.4) * mm});
            skLineSegment(sketch, "E181.5.2", {"start": v(57.17, 132.8) * mm, "end": v(59.9, 131.34) * mm});
            skLineSegment(sketch, "E181.5.3", {"start": v(59.9, 131.34) * mm, "end": v(60.16, 131.6) * mm});
            skArc(sketch, "E181.5.4", {"start": v(57.17, 132.8) * mm, "mid": v(56.9, 132.47) * mm, "end": v(56.63, 132.14) * mm});
            skLineSegment(sketch, "E181.6.0", {"start": v(54.75, 129.33) * mm, "end": v(57.05, 127.25) * mm});
            skLineSegment(sketch, "E181.6.1", {"start": v(57.05, 127.25) * mm, "end": v(56.9, 126.93) * mm});
            skLineSegment(sketch, "E181.6.2", {"start": v(55.17, 130.06) * mm, "end": v(58.12, 129.11) * mm});
            skLineSegment(sketch, "E181.6.3", {"start": v(58.12, 129.11) * mm, "end": v(58.32, 129.4) * mm});
            skArc(sketch, "E181.6.4", {"start": v(55.17, 130.06) * mm, "mid": v(54.96, 129.7) * mm, "end": v(54.75, 129.33) * mm});
            skLineSegment(sketch, "E181.7.0", {"start": v(53.39, 126.24) * mm, "end": v(56.01, 124.59) * mm});
            skLineSegment(sketch, "E181.7.1", {"start": v(56.01, 124.59) * mm, "end": v(55.91, 124.24) * mm});
            skLineSegment(sketch, "E181.7.2", {"start": v(53.68, 127.03) * mm, "end": v(56.74, 126.6) * mm});
            skLineSegment(sketch, "E181.7.3", {"start": v(56.74, 126.6) * mm, "end": v(56.9, 126.93) * mm});
            skArc(sketch, "E181.7.4", {"start": v(53.68, 127.03) * mm, "mid": v(53.53, 126.64) * mm, "end": v(53.39, 126.24) * mm});
            skLineSegment(sketch, "E181.8.0", {"start": v(52.58, 122.95) * mm, "end": v(55.45, 121.79) * mm});
            skLineSegment(sketch, "E181.8.1", {"start": v(55.45, 121.79) * mm, "end": v(55.42, 121.43) * mm});
            skLineSegment(sketch, "E181.8.2", {"start": v(52.73, 123.78) * mm, "end": v(55.83, 123.9) * mm});
            skLineSegment(sketch, "E181.8.3", {"start": v(55.83, 123.9) * mm, "end": v(55.91, 124.24) * mm});
            skArc(sketch, "E181.8.4", {"start": v(52.73, 123.78) * mm, "mid": v(52.65, 123.37) * mm, "end": v(52.58, 122.95) * mm});
            skLineSegment(sketch, "E181.9.0", {"start": v(52.36, 119.58) * mm, "end": v(55.4, 118.93) * mm});
            skLineSegment(sketch, "E181.9.1", {"start": v(55.4, 118.93) * mm, "end": v(55.42, 118.57) * mm});
            skLineSegment(sketch, "E181.9.2", {"start": v(52.36, 120.42) * mm, "end": v(55.4, 121.07) * mm});
            skLineSegment(sketch, "E181.9.3", {"start": v(55.4, 121.07) * mm, "end": v(55.42, 121.43) * mm});
            skArc(sketch, "E181.9.4", {"start": v(52.36, 120.42) * mm, "mid": v(52.36, 120) * mm, "end": v(52.36, 119.58) * mm});
            skLineSegment(sketch, "E181.10.0", {"start": v(52.73, 116.22) * mm, "end": v(55.83, 116.1) * mm});
            skLineSegment(sketch, "E181.10.1", {"start": v(55.83, 116.1) * mm, "end": v(55.91, 115.76) * mm});
            skLineSegment(sketch, "E181.10.2", {"start": v(52.58, 117.05) * mm, "end": v(55.45, 118.21) * mm});
            skLineSegment(sketch, "E181.10.3", {"start": v(55.45, 118.21) * mm, "end": v(55.42, 118.57) * mm});
            skArc(sketch, "E181.10.4", {"start": v(52.58, 117.05) * mm, "mid": v(52.65, 116.63) * mm, "end": v(52.73, 116.22) * mm});
            skLineSegment(sketch, "E181.11.0", {"start": v(53.68, 112.97) * mm, "end": v(56.74, 113.4) * mm});
            skLineSegment(sketch, "E181.11.1", {"start": v(56.74, 113.4) * mm, "end": v(56.9, 113.07) * mm});
            skLineSegment(sketch, "E181.11.2", {"start": v(53.39, 113.76) * mm, "end": v(56.01, 115.41) * mm});
            skLineSegment(sketch, "E181.11.3", {"start": v(56.01, 115.41) * mm, "end": v(55.91, 115.76) * mm});
            skArc(sketch, "E181.11.4", {"start": v(53.39, 113.76) * mm, "mid": v(53.53, 113.36) * mm, "end": v(53.68, 112.97) * mm});
            skLineSegment(sketch, "E181.12.0", {"start": v(55.17, 109.94) * mm, "end": v(58.12, 110.89) * mm});
            skLineSegment(sketch, "E181.12.1", {"start": v(58.12, 110.89) * mm, "end": v(58.32, 110.6) * mm});
            skLineSegment(sketch, "E181.12.2", {"start": v(54.75, 110.67) * mm, "end": v(57.05, 112.75) * mm});
            skLineSegment(sketch, "E181.12.3", {"start": v(57.05, 112.75) * mm, "end": v(56.9, 113.07) * mm});
            skArc(sketch, "E181.12.4", {"start": v(54.75, 110.67) * mm, "mid": v(54.96, 110.3) * mm, "end": v(55.17, 109.94) * mm});
            skLineSegment(sketch, "E181.13.0", {"start": v(57.17, 107.2) * mm, "end": v(59.9, 108.66) * mm});
            skLineSegment(sketch, "E181.13.1", {"start": v(59.9, 108.66) * mm, "end": v(60.16, 108.4) * mm});
            skLineSegment(sketch, "E181.13.2", {"start": v(56.63, 107.86) * mm, "end": v(58.53, 110.3) * mm});
            skLineSegment(sketch, "E181.13.3", {"start": v(58.53, 110.3) * mm, "end": v(58.32, 110.6) * mm});
            skArc(sketch, "E181.13.4", {"start": v(56.63, 107.86) * mm, "mid": v(56.9, 107.53) * mm, "end": v(57.17, 107.2) * mm});
            skLineSegment(sketch, "E181.14.0", {"start": v(59.61, 104.87) * mm, "end": v(62.06, 106.77) * mm});
            skLineSegment(sketch, "E181.14.1", {"start": v(62.06, 106.77) * mm, "end": v(62.35, 106.57) * mm});
            skLineSegment(sketch, "E181.14.2", {"start": v(58.96, 105.41) * mm, "end": v(60.42, 108.15) * mm});
            skLineSegment(sketch, "E181.14.3", {"start": v(60.42, 108.15) * mm, "end": v(60.16, 108.4) * mm});
            skArc(sketch, "E181.14.4", {"start": v(58.96, 105.41) * mm, "mid": v(59.29, 105.14) * mm, "end": v(59.61, 104.87) * mm});
            skLineSegment(sketch, "E181.15.0", {"start": v(62.42, 103) * mm, "end": v(64.5, 105.3) * mm});
            skLineSegment(sketch, "E181.15.1", {"start": v(64.5, 105.3) * mm, "end": v(64.83, 105.14) * mm});
            skLineSegment(sketch, "E181.15.2", {"start": v(61.7, 103.41) * mm, "end": v(62.64, 106.36) * mm});
            skLineSegment(sketch, "E181.15.3", {"start": v(62.64, 106.36) * mm, "end": v(62.35, 106.57) * mm});
            skArc(sketch, "E181.15.4", {"start": v(61.7, 103.41) * mm, "mid": v(62.06, 103.2) * mm, "end": v(62.42, 103) * mm});
            skLineSegment(sketch, "E181.16.0", {"start": v(65.52, 101.63) * mm, "end": v(67.17, 104.26) * mm});
            skLineSegment(sketch, "E181.16.1", {"start": v(67.17, 104.26) * mm, "end": v(67.51, 104.16) * mm});
            skLineSegment(sketch, "E181.16.2", {"start": v(64.72, 101.92) * mm, "end": v(65.15, 104.99) * mm});
            skLineSegment(sketch, "E181.16.3", {"start": v(65.15, 104.99) * mm, "end": v(64.83, 105.14) * mm});
            skArc(sketch, "E181.16.4", {"start": v(64.72, 101.92) * mm, "mid": v(65.12, 101.77) * mm, "end": v(65.52, 101.63) * mm});
            skLineSegment(sketch, "E181.17.0", {"start": v(68.8, 100.83) * mm, "end": v(69.97, 103.7) * mm});
            skLineSegment(sketch, "E181.17.1", {"start": v(69.97, 103.7) * mm, "end": v(70.33, 103.66) * mm});
            skLineSegment(sketch, "E181.17.2", {"start": v(67.97, 100.97) * mm, "end": v(67.86, 104.07) * mm});
            skLineSegment(sketch, "E181.17.3", {"start": v(67.86, 104.07) * mm, "end": v(67.51, 104.16) * mm});
            skArc(sketch, "E181.17.4", {"start": v(67.97, 100.97) * mm, "mid": v(68.39, 100.9) * mm, "end": v(68.8, 100.83) * mm});
            skLineSegment(sketch, "E181.18.0", {"start": v(72.18, 100.6) * mm, "end": v(72.83, 103.64) * mm});
            skLineSegment(sketch, "E181.18.1", {"start": v(72.83, 103.64) * mm, "end": v(73.19, 103.66) * mm});
            skLineSegment(sketch, "E181.18.2", {"start": v(71.33, 100.6) * mm, "end": v(70.68, 103.64) * mm});
            skLineSegment(sketch, "E181.18.3", {"start": v(70.68, 103.64) * mm, "end": v(70.33, 103.66) * mm});
            skArc(sketch, "E181.18.4", {"start": v(71.33, 100.6) * mm, "mid": v(71.76, 100.6) * mm, "end": v(72.18, 100.6) * mm});
            skLineSegment(sketch, "E181.19.0", {"start": v(75.54, 100.97) * mm, "end": v(75.65, 104.07) * mm});
            skLineSegment(sketch, "E181.19.1", {"start": v(75.65, 104.07) * mm, "end": v(76, 104.16) * mm});
            skLineSegment(sketch, "E181.19.2", {"start": v(74.7, 100.83) * mm, "end": v(73.54, 103.7) * mm});
            skLineSegment(sketch, "E181.19.3", {"start": v(73.54, 103.7) * mm, "end": v(73.19, 103.66) * mm});
            skArc(sketch, "E181.19.4", {"start": v(74.7, 100.83) * mm, "mid": v(75.12, 100.9) * mm, "end": v(75.54, 100.97) * mm});
            skLineSegment(sketch, "E181.20.0", {"start": v(78.79, 101.92) * mm, "end": v(78.36, 104.99) * mm});
            skLineSegment(sketch, "E181.20.1", {"start": v(78.36, 104.99) * mm, "end": v(78.69, 105.14) * mm});
            skLineSegment(sketch, "E181.20.2", {"start": v(78, 101.63) * mm, "end": v(76.35, 104.26) * mm});
            skLineSegment(sketch, "E181.20.3", {"start": v(76.35, 104.26) * mm, "end": v(76, 104.16) * mm});
            skArc(sketch, "E181.20.4", {"start": v(78, 101.63) * mm, "mid": v(78.4, 101.77) * mm, "end": v(78.79, 101.92) * mm});
            skLineSegment(sketch, "E181.21.0", {"start": v(81.82, 103.41) * mm, "end": v(80.87, 106.36) * mm});
            skLineSegment(sketch, "E181.21.1", {"start": v(80.87, 106.36) * mm, "end": v(81.16, 106.57) * mm});
            skLineSegment(sketch, "E181.21.2", {"start": v(81.09, 103) * mm, "end": v(79, 105.3) * mm});
            skLineSegment(sketch, "E181.21.3", {"start": v(79, 105.3) * mm, "end": v(78.69, 105.14) * mm});
            skArc(sketch, "E181.21.4", {"start": v(81.09, 103) * mm, "mid": v(81.46, 103.2) * mm, "end": v(81.82, 103.41) * mm});
            skLineSegment(sketch, "E181.22.0", {"start": v(84.55, 105.41) * mm, "end": v(83.1, 108.15) * mm});
            skLineSegment(sketch, "E181.22.1", {"start": v(83.1, 108.15) * mm, "end": v(83.35, 108.4) * mm});
            skLineSegment(sketch, "E181.22.2", {"start": v(83.9, 104.87) * mm, "end": v(81.45, 106.77) * mm});
            skLineSegment(sketch, "E181.22.3", {"start": v(81.45, 106.77) * mm, "end": v(81.16, 106.57) * mm});
            skArc(sketch, "E181.22.4", {"start": v(83.9, 104.87) * mm, "mid": v(84.23, 105.14) * mm, "end": v(84.55, 105.41) * mm});
            skLineSegment(sketch, "E181.23.0", {"start": v(86.89, 107.86) * mm, "end": v(84.98, 110.3) * mm});
            skLineSegment(sketch, "E181.23.1", {"start": v(84.98, 110.3) * mm, "end": v(85.2, 110.6) * mm});
            skLineSegment(sketch, "E181.23.2", {"start": v(86.34, 107.2) * mm, "end": v(83.6, 108.66) * mm});
            skLineSegment(sketch, "E181.23.3", {"start": v(83.6, 108.66) * mm, "end": v(83.35, 108.4) * mm});
            skArc(sketch, "E181.23.4", {"start": v(86.34, 107.2) * mm, "mid": v(86.62, 107.53) * mm, "end": v(86.89, 107.86) * mm});
            skLineSegment(sketch, "E181.24.0", {"start": v(88.76, 110.67) * mm, "end": v(86.46, 112.75) * mm});
            skLineSegment(sketch, "E181.24.1", {"start": v(86.46, 112.75) * mm, "end": v(86.62, 113.07) * mm});
            skLineSegment(sketch, "E181.24.2", {"start": v(88.34, 109.94) * mm, "end": v(85.4, 110.89) * mm});
            skLineSegment(sketch, "E181.24.3", {"start": v(85.4, 110.89) * mm, "end": v(85.2, 110.6) * mm});
            skArc(sketch, "E181.24.4", {"start": v(88.34, 109.94) * mm, "mid": v(88.56, 110.3) * mm, "end": v(88.76, 110.67) * mm});
            skLineSegment(sketch, "E181.25.0", {"start": v(90.13, 113.76) * mm, "end": v(87.5, 115.41) * mm});
            skLineSegment(sketch, "E181.25.1", {"start": v(87.5, 115.41) * mm, "end": v(87.6, 115.76) * mm});
            skLineSegment(sketch, "E181.25.2", {"start": v(89.84, 112.97) * mm, "end": v(86.77, 113.4) * mm});
            skLineSegment(sketch, "E181.25.3", {"start": v(86.77, 113.4) * mm, "end": v(86.62, 113.07) * mm});
            skArc(sketch, "E181.25.4", {"start": v(89.84, 112.97) * mm, "mid": v(89.99, 113.36) * mm, "end": v(90.13, 113.76) * mm});
            skLineSegment(sketch, "E181.26.0", {"start": v(90.93, 117.05) * mm, "end": v(88.06, 118.21) * mm});
            skLineSegment(sketch, "E181.26.1", {"start": v(88.06, 118.21) * mm, "end": v(88.1, 118.57) * mm});
            skLineSegment(sketch, "E181.26.2", {"start": v(90.78, 116.22) * mm, "end": v(87.69, 116.1) * mm});
            skLineSegment(sketch, "E181.26.3", {"start": v(87.69, 116.1) * mm, "end": v(87.6, 115.76) * mm});
            skArc(sketch, "E181.26.4", {"start": v(90.78, 116.22) * mm, "mid": v(90.86, 116.63) * mm, "end": v(90.93, 117.05) * mm});
            skLineSegment(sketch, "E181.27.0", {"start": v(91.15, 120.42) * mm, "end": v(88.12, 121.07) * mm});
            skLineSegment(sketch, "E181.27.1", {"start": v(88.12, 121.07) * mm, "end": v(88.1, 121.43) * mm});
            skLineSegment(sketch, "E181.27.2", {"start": v(91.15, 119.58) * mm, "end": v(88.12, 118.93) * mm});
            skLineSegment(sketch, "E181.27.3", {"start": v(88.12, 118.93) * mm, "end": v(88.1, 118.57) * mm});
            skArc(sketch, "E181.27.4", {"start": v(91.15, 119.58) * mm, "mid": v(91.16, 120) * mm, "end": v(91.15, 120.42) * mm});
            skLineSegment(sketch, "E181.28.0", {"start": v(90.78, 123.78) * mm, "end": v(87.69, 123.9) * mm});
            skLineSegment(sketch, "E181.28.1", {"start": v(87.69, 123.9) * mm, "end": v(87.6, 124.24) * mm});
            skLineSegment(sketch, "E181.28.2", {"start": v(90.93, 122.95) * mm, "end": v(88.06, 121.79) * mm});
            skLineSegment(sketch, "E181.28.3", {"start": v(88.06, 121.79) * mm, "end": v(88.1, 121.43) * mm});
            skArc(sketch, "E181.28.4", {"start": v(90.93, 122.95) * mm, "mid": v(90.86, 123.37) * mm, "end": v(90.78, 123.78) * mm});
            skLineSegment(sketch, "E181.29.0", {"start": v(89.84, 127.03) * mm, "end": v(86.77, 126.6) * mm});
            skLineSegment(sketch, "E181.29.1", {"start": v(86.77, 126.6) * mm, "end": v(86.62, 126.93) * mm});
            skLineSegment(sketch, "E181.29.2", {"start": v(90.13, 126.24) * mm, "end": v(87.5, 124.59) * mm});
            skLineSegment(sketch, "E181.29.3", {"start": v(87.5, 124.59) * mm, "end": v(87.6, 124.24) * mm});
            skArc(sketch, "E181.29.4", {"start": v(90.13, 126.24) * mm, "mid": v(89.99, 126.64) * mm, "end": v(89.84, 127.03) * mm});
            skLineSegment(sketch, "E181.30.0", {"start": v(88.34, 130.06) * mm, "end": v(85.4, 129.11) * mm});
            skLineSegment(sketch, "E181.30.1", {"start": v(85.4, 129.11) * mm, "end": v(85.2, 129.4) * mm});
            skLineSegment(sketch, "E181.30.2", {"start": v(88.76, 129.33) * mm, "end": v(86.46, 127.25) * mm});
            skLineSegment(sketch, "E181.30.3", {"start": v(86.46, 127.25) * mm, "end": v(86.62, 126.93) * mm});
            skArc(sketch, "E181.30.4", {"start": v(88.76, 129.33) * mm, "mid": v(88.56, 129.7) * mm, "end": v(88.34, 130.06) * mm});
            skLineSegment(sketch, "E181.31.0", {"start": v(86.34, 132.8) * mm, "end": v(83.6, 131.34) * mm});
            skLineSegment(sketch, "E181.31.1", {"start": v(83.6, 131.34) * mm, "end": v(83.35, 131.6) * mm});
            skLineSegment(sketch, "E181.31.2", {"start": v(86.89, 132.14) * mm, "end": v(84.98, 129.7) * mm});
            skLineSegment(sketch, "E181.31.3", {"start": v(84.98, 129.7) * mm, "end": v(85.2, 129.4) * mm});
            skArc(sketch, "E181.31.4", {"start": v(86.89, 132.14) * mm, "mid": v(86.62, 132.47) * mm, "end": v(86.34, 132.8) * mm});
            skLineSegment(sketch, "E181.32.0", {"start": v(83.9, 135.13) * mm, "end": v(81.45, 133.23) * mm});
            skLineSegment(sketch, "E181.32.1", {"start": v(81.45, 133.23) * mm, "end": v(81.16, 133.43) * mm});
            skLineSegment(sketch, "E181.32.2", {"start": v(84.55, 134.59) * mm, "end": v(83.1, 131.85) * mm});
            skLineSegment(sketch, "E181.32.3", {"start": v(83.1, 131.85) * mm, "end": v(83.35, 131.6) * mm});
            skArc(sketch, "E181.32.4", {"start": v(84.55, 134.59) * mm, "mid": v(84.23, 134.86) * mm, "end": v(83.9, 135.13) * mm});
            skLineSegment(sketch, "E181.33.0", {"start": v(81.09, 137) * mm, "end": v(79, 134.7) * mm});
            skLineSegment(sketch, "E181.33.1", {"start": v(79, 134.7) * mm, "end": v(78.69, 134.86) * mm});
            skLineSegment(sketch, "E181.33.2", {"start": v(81.82, 136.59) * mm, "end": v(80.87, 133.64) * mm});
            skLineSegment(sketch, "E181.33.3", {"start": v(80.87, 133.64) * mm, "end": v(81.16, 133.43) * mm});
            skArc(sketch, "E181.33.4", {"start": v(81.82, 136.59) * mm, "mid": v(81.46, 136.8) * mm, "end": v(81.09, 137) * mm});
            skLineSegment(sketch, "E181.34.0", {"start": v(78, 138.37) * mm, "end": v(76.35, 135.74) * mm});
            skLineSegment(sketch, "E181.34.1", {"start": v(76.35, 135.74) * mm, "end": v(76, 135.84) * mm});
            skLineSegment(sketch, "E181.34.2", {"start": v(78.79, 138.08) * mm, "end": v(78.36, 135.01) * mm});
            skLineSegment(sketch, "E181.34.3", {"start": v(78.36, 135.01) * mm, "end": v(78.69, 134.86) * mm});
            skArc(sketch, "E181.34.4", {"start": v(78.79, 138.08) * mm, "mid": v(78.4, 138.23) * mm, "end": v(78, 138.37) * mm});
            skLineSegment(sketch, "E181.35.0", {"start": v(74.7, 139.17) * mm, "end": v(73.54, 136.3) * mm});
            skLineSegment(sketch, "E181.35.1", {"start": v(73.54, 136.3) * mm, "end": v(73.19, 136.34) * mm});
            skLineSegment(sketch, "E181.35.2", {"start": v(75.54, 139.03) * mm, "end": v(75.65, 135.93) * mm});
            skLineSegment(sketch, "E181.35.3", {"start": v(75.65, 135.93) * mm, "end": v(76, 135.84) * mm});
            skArc(sketch, "E181.35.4", {"start": v(75.54, 139.03) * mm, "mid": v(75.12, 139.1) * mm, "end": v(74.7, 139.17) * mm});
            skLineSegment(sketch, "E182", {"start": v(-327.67, -4594.38) * mm, "end": v(-280.95, -4594.38) * mm});
            skLineSegment(sketch, "E183", {"start": v(-280.95, -4594.38) * mm, "end": v(-168.42, -5905.89) * mm});
            skLineSegment(sketch, "E184", {"start": v(-168.42, -5905.89) * mm, "end": v(-403.83, -5905.89) * mm});
            skLineSegment(sketch, "E185", {"start": v(-403.83, -5905.89) * mm, "end": v(-327.67, -4594.38) * mm});
            skSolve(sketch);
        }
        {
            var Q0;
            Q0=qSketchRegion(id+"F24",true);
            extrude(context, id + "F25", {"entities" : qUnion([Q0]), "depth" : 6 * mm, "hasDraft" : true, "draftAngle" : 45 * degree});
        }
        {
            var Q0;
            Q0=makeQuery(id+"F11.opExtrude","CAP_FACE",FACE,{"disambiguationData":[OSD([sQuery(id+"F10.wireOp",EDGE,"E114.bottom"),sQuery(id+"F10.wireOp",EDGE,"E114.top"),sQuery(id+"F10.wireOp",EDGE,"E114.left"),sQuery(id+"F10.wireOp",EDGE,"E114.right"),sQuery(id+"F10.wireOp",EDGE,"E115.top"),sQuery(id+"F10.wireOp",EDGE,"E115.right"),sQuery(id+"F10.wireOp",EDGE,"E116.top"),sQuery(id+"F10.wireOp",EDGE,"E116.right"),sQuery(id+"F10.wireOp",EDGE,"E118"),sQuery(id+"F10.wireOp",EDGE,"E120"),sQuery(id+"F10.wireOp",EDGE,"E121")])],"isStart":true});
            var sketch = newSketch(context, id + "F26", { "sketchPlane" : qUnion([Q0])});
            skCircle(sketch, "E186", {"center": v(-75, 120) * mm, "radius": 18 * mm});
            skCircle(sketch, "E187", {"center": v(-75, 120) * mm, "radius": 2.5 * mm});
            skSolve(sketch);
        }
        {
            var Q0;
            Q0=qSketchRegion(id+"F26",true);
            extrude(context, id + "F27", {"entities" : qUnion([Q0]), "depth" : 6 * mm});
        }
        {
            var Q0;
            Q0=makeQuery(id+"F11.opExtrude","CAP_FACE",FACE,{"disambiguationData":[OSD([sQuery(id+"F10.wireOp",EDGE,"E114.bottom"),sQuery(id+"F10.wireOp",EDGE,"E114.top"),sQuery(id+"F10.wireOp",EDGE,"E114.left"),sQuery(id+"F10.wireOp",EDGE,"E114.right"),sQuery(id+"F10.wireOp",EDGE,"E115.top"),sQuery(id+"F10.wireOp",EDGE,"E115.right"),sQuery(id+"F10.wireOp",EDGE,"E116.top"),sQuery(id+"F10.wireOp",EDGE,"E116.right"),sQuery(id+"F10.wireOp",EDGE,"E118"),sQuery(id+"F10.wireOp",EDGE,"E120"),sQuery(id+"F10.wireOp",EDGE,"E121")])],"isStart":true});
            var sketch = newSketch(context, id + "F28", { "sketchPlane" : qUnion([Q0])});
            skCircle(sketch, "E188", {"center": v(-39, 120) * mm, "radius": 18 * mm});
            skCircle(sketch, "E189", {"center": v(-39, 120) * mm, "radius": 2.5 * mm});
            skSolve(sketch);
        }
        {
            var Q0;
            Q0=qSketchRegion(id+"F28",true);
            extrude(context, id + "F29", {"entities" : qUnion([Q0]), "depth" : 6 * mm});
        }
        {
            var Q0;
            Q0=makeQuery(id+"F11.opExtrude","CAP_FACE",FACE,{"disambiguationData":[OSD([sQuery(id+"F10.wireOp",EDGE,"E114.bottom"),sQuery(id+"F10.wireOp",EDGE,"E114.top"),sQuery(id+"F10.wireOp",EDGE,"E114.left"),sQuery(id+"F10.wireOp",EDGE,"E114.right"),sQuery(id+"F10.wireOp",EDGE,"E115.top"),sQuery(id+"F10.wireOp",EDGE,"E115.right"),sQuery(id+"F10.wireOp",EDGE,"E116.top"),sQuery(id+"F10.wireOp",EDGE,"E116.right"),sQuery(id+"F10.wireOp",EDGE,"E118"),sQuery(id+"F10.wireOp",EDGE,"E120"),sQuery(id+"F10.wireOp",EDGE,"E121")])],"isStart":true});
            var sketch = newSketch(context, id + "F30", { "sketchPlane" : qUnion([Q0])});
            skCircle(sketch, "E190", {"center": v(-3, 120) * mm, "radius": 18 * mm});
            skCircle(sketch, "E191", {"center": v(-3, 120) * mm, "radius": 2.5 * mm});
            skSolve(sketch);
        }
        {
            var Q0;
            Q0=qSketchRegion(id+"F30",true);
            extrude(context, id + "F31", {"entities" : qUnion([Q0]), "depth" : 6 * mm});
        }
        {
            var Q0;
            Q0=makeQuery(id+"F9.opExtrude","CAP_FACE",FACE,{"disambiguationData":[OSD([sQuery(id+"F8.wireOp",EDGE,"E102.rect.bottom"),sQuery(id+"F8.wireOp",EDGE,"E102.rect.top"),sQuery(id+"F8.wireOp",EDGE,"E102.rect.left"),sQuery(id+"F8.wireOp",EDGE,"E102.rect.right"),sQuery(id+"F8.wireOp",EDGE,"E103"),sQuery(id+"F8.wireOp",EDGE,"E104"),sQuery(id+"F8.wireOp",EDGE,"E105"),sQuery(id+"F8.wireOp",EDGE,"E106"),sQuery(id+"F8.wireOp",EDGE,"E107"),sQuery(id+"F8.wireOp",EDGE,"E112"),sQuery(id+"F8.wireOp",EDGE,"E113")])],"isStart":true});
            var sketch = newSketch(context, id + "F32", { "sketchPlane" : qUnion([Q0])});
            skCircle(sketch, "E192", {"center": v(35.76, 120) * mm, "radius": 18 * mm});
            skCircle(sketch, "E193", {"center": v(35.76, 120) * mm, "radius": 2.5 * mm});
            skSolve(sketch);
        }
        {
            var Q0;
            Q0=qSketchRegion(id+"F32",true);
            extrude(context, id + "F33", {"entities" : qUnion([Q0]), "depth" : 6 * mm});
        }
        {
            var Q0;
            Q0=qCreatedBy(makeId("Front.planeOp"),FACE);
            var sketch = newSketch(context, id + "F34", { "sketchPlane" : qUnion([Q0])});
            skCircle(sketch, "E194", {"center": v(0, -22.34) * mm, "radius": 16.4 * mm, "construction": true});
            skCircle(sketch, "E195", {"center": v(0, -22.34) * mm, "radius": 19.4 * mm, "construction": true});
            skLineSegment(sketch, "E196", {"start": v(0, -22.34) * mm, "end": v(0, -2.94) * mm, "construction": true});
            skLineSegment(sketch, "E197", {"start": v(0, -22.34) * mm, "end": v(-0.42, -2.94) * mm, "construction": true});
            skLineSegment(sketch, "E198", {"start": v(0, -22.34) * mm, "end": v(-0.85, -2.96) * mm, "construction": true});
            skLineSegment(sketch, "E199", {"start": v(0, -22.34) * mm, "end": v(-1.27, -2.98) * mm, "construction": true});
            skLineSegment(sketch, "E200", {"start": v(0, -22.34) * mm, "end": v(-1.7, -3.01) * mm, "construction": true});
            skLineSegment(sketch, "E201", {"start": v(0, -22.34) * mm, "end": v(-2.11, -3.05) * mm, "construction": true});
            skLineSegment(sketch, "E202", {"start": v(0, -22.34) * mm, "end": v(-2.53, -3.1) * mm, "construction": true});
            skLineSegment(sketch, "E203", {"start": v(0, -22.34) * mm, "end": v(-2.95, -3.16) * mm, "construction": true});
            skLineSegment(sketch, "E204", {"start": v(0, -22.34) * mm, "end": v(-3.37, -3.23) * mm, "construction": true});
            skArc(sketch, "E205", {"start": v(-1.27, -2.98) * mm, "mid": v(-1.7, -3.01) * mm, "end": v(-2.11, -3.05) * mm});
            skLineSegment(sketch, "E206", {"start": v(-1.27, -2.98) * mm, "end": v(-0.36, -5.94) * mm});
            skLineSegment(sketch, "E207", {"start": v(-0.36, -5.94) * mm, "end": v(0, -5.93) * mm});
            skLineSegment(sketch, "E208", {"start": v(-2.11, -3.05) * mm, "end": v(-2.5, -6.13) * mm});
            skLineSegment(sketch, "E209", {"start": v(-2.5, -6.13) * mm, "end": v(-2.85, -6.18) * mm});
            skLineSegment(sketch, "E210.1.0", {"start": v(-3.2, -6.25) * mm, "end": v(-2.85, -6.18) * mm});
            skLineSegment(sketch, "E210.1.1", {"start": v(-4.61, -3.5) * mm, "end": v(-3.2, -6.25) * mm});
            skArc(sketch, "E210.1.2", {"start": v(-4.61, -3.5) * mm, "mid": v(-5.02, -3.6) * mm, "end": v(-5.43, -3.71) * mm});
            skLineSegment(sketch, "E210.1.3", {"start": v(-5.43, -3.71) * mm, "end": v(-5.27, -6.8) * mm});
            skLineSegment(sketch, "E210.1.4", {"start": v(-5.27, -6.8) * mm, "end": v(-5.61, -6.92) * mm});
            skLineSegment(sketch, "E210.2.0", {"start": v(-5.94, -7.05) * mm, "end": v(-5.61, -6.92) * mm});
            skLineSegment(sketch, "E210.2.1", {"start": v(-7.81, -4.58) * mm, "end": v(-5.94, -7.05) * mm});
            skArc(sketch, "E210.2.2", {"start": v(-7.81, -4.58) * mm, "mid": v(-8.2, -4.75) * mm, "end": v(-8.58, -4.94) * mm});
            skLineSegment(sketch, "E210.2.3", {"start": v(-8.58, -4.94) * mm, "end": v(-7.89, -7.96) * mm});
            skLineSegment(sketch, "E210.2.4", {"start": v(-7.89, -7.96) * mm, "end": v(-8.2, -8.13) * mm});
            skLineSegment(sketch, "E210.3.0", {"start": v(-8.5, -8.32) * mm, "end": v(-8.2, -8.13) * mm});
            skLineSegment(sketch, "E210.3.1", {"start": v(-10.78, -6.2) * mm, "end": v(-8.5, -8.32) * mm});
            skArc(sketch, "E210.3.2", {"start": v(-10.78, -6.2) * mm, "mid": v(-11.13, -6.45) * mm, "end": v(-11.47, -6.7) * mm});
            skLineSegment(sketch, "E210.3.3", {"start": v(-11.47, -6.7) * mm, "end": v(-10.27, -9.55) * mm});
            skLineSegment(sketch, "E210.3.4", {"start": v(-10.27, -9.55) * mm, "end": v(-10.54, -9.77) * mm});
            skLineSegment(sketch, "E210.4.0", {"start": v(-10.81, -10) * mm, "end": v(-10.54, -9.77) * mm});
            skLineSegment(sketch, "E210.4.1", {"start": v(-13.42, -8.32) * mm, "end": v(-10.81, -10) * mm});
            skArc(sketch, "E210.4.2", {"start": v(-13.42, -8.32) * mm, "mid": v(-13.72, -8.62) * mm, "end": v(-14.01, -8.92) * mm});
            skLineSegment(sketch, "E210.4.3", {"start": v(-14.01, -8.92) * mm, "end": v(-12.33, -11.52) * mm});
            skLineSegment(sketch, "E210.4.4", {"start": v(-12.33, -11.52) * mm, "end": v(-12.57, -11.8) * mm});
            skLineSegment(sketch, "E210.5.0", {"start": v(-12.8, -12.07) * mm, "end": v(-12.57, -11.8) * mm});
            skLineSegment(sketch, "E210.5.1", {"start": v(-15.65, -10.87) * mm, "end": v(-12.8, -12.07) * mm});
            skArc(sketch, "E210.5.2", {"start": v(-15.65, -10.87) * mm, "mid": v(-15.9, -11.2) * mm, "end": v(-16.13, -11.56) * mm});
            skLineSegment(sketch, "E210.5.3", {"start": v(-16.13, -11.56) * mm, "end": v(-14.02, -13.83) * mm});
            skLineSegment(sketch, "E210.5.4", {"start": v(-14.02, -13.83) * mm, "end": v(-14.2, -14.13) * mm});
            skLineSegment(sketch, "E210.6.0", {"start": v(-14.38, -14.45) * mm, "end": v(-14.2, -14.13) * mm});
            skLineSegment(sketch, "E210.6.1", {"start": v(-17.4, -13.76) * mm, "end": v(-14.38, -14.45) * mm});
            skArc(sketch, "E210.6.2", {"start": v(-17.4, -13.76) * mm, "mid": v(-17.58, -14.14) * mm, "end": v(-17.76, -14.52) * mm});
            skLineSegment(sketch, "E210.6.3", {"start": v(-17.76, -14.52) * mm, "end": v(-15.28, -16.4) * mm});
            skLineSegment(sketch, "E210.6.4", {"start": v(-15.28, -16.4) * mm, "end": v(-15.41, -16.73) * mm});
            skLineSegment(sketch, "E210.7.0", {"start": v(-15.53, -17.07) * mm, "end": v(-15.41, -16.73) * mm});
            skLineSegment(sketch, "E210.7.1", {"start": v(-18.62, -16.9) * mm, "end": v(-15.53, -17.07) * mm});
            skArc(sketch, "E210.7.2", {"start": v(-18.62, -16.9) * mm, "mid": v(-18.74, -17.32) * mm, "end": v(-18.84, -17.73) * mm});
            skLineSegment(sketch, "E210.7.3", {"start": v(-18.84, -17.73) * mm, "end": v(-16.08, -19.14) * mm});
            skLineSegment(sketch, "E210.7.4", {"start": v(-16.08, -19.14) * mm, "end": v(-16.15, -19.49) * mm});
            skLineSegment(sketch, "E210.8.0", {"start": v(-16.2, -19.84) * mm, "end": v(-16.15, -19.49) * mm});
            skLineSegment(sketch, "E210.8.1", {"start": v(-19.28, -20.22) * mm, "end": v(-16.2, -19.84) * mm});
            skArc(sketch, "E210.8.2", {"start": v(-19.28, -20.22) * mm, "mid": v(-19.33, -20.65) * mm, "end": v(-19.36, -21.07) * mm});
            skLineSegment(sketch, "E210.8.3", {"start": v(-19.36, -21.07) * mm, "end": v(-16.4, -21.98) * mm});
            skLineSegment(sketch, "E210.8.4", {"start": v(-16.4, -21.98) * mm, "end": v(-16.4, -22.34) * mm});
            skLineSegment(sketch, "E210.9.0", {"start": v(-16.4, -22.7) * mm, "end": v(-16.4, -22.34) * mm});
            skLineSegment(sketch, "E210.9.1", {"start": v(-19.36, -23.6) * mm, "end": v(-16.4, -22.7) * mm});
            skArc(sketch, "E210.9.2", {"start": v(-19.36, -23.6) * mm, "mid": v(-19.33, -24.03) * mm, "end": v(-19.28, -24.45) * mm});
            skLineSegment(sketch, "E210.9.3", {"start": v(-19.28, -24.45) * mm, "end": v(-16.2, -24.83) * mm});
            skLineSegment(sketch, "E210.9.4", {"start": v(-16.2, -24.83) * mm, "end": v(-16.15, -25.19) * mm});
            skLineSegment(sketch, "E210.10.0", {"start": v(-16.08, -25.54) * mm, "end": v(-16.15, -25.19) * mm});
            skLineSegment(sketch, "E210.10.1", {"start": v(-18.84, -26.95) * mm, "end": v(-16.08, -25.54) * mm});
            skArc(sketch, "E210.10.2", {"start": v(-18.84, -26.95) * mm, "mid": v(-18.74, -27.36) * mm, "end": v(-18.62, -27.77) * mm});
            skLineSegment(sketch, "E210.10.3", {"start": v(-18.62, -27.77) * mm, "end": v(-15.53, -27.6) * mm});
            skLineSegment(sketch, "E210.10.4", {"start": v(-15.53, -27.6) * mm, "end": v(-15.41, -27.95) * mm});
            skLineSegment(sketch, "E210.11.0", {"start": v(-15.28, -28.28) * mm, "end": v(-15.41, -27.95) * mm});
            skLineSegment(sketch, "E210.11.1", {"start": v(-17.76, -30.15) * mm, "end": v(-15.28, -28.28) * mm});
            skArc(sketch, "E210.11.2", {"start": v(-17.76, -30.15) * mm, "mid": v(-17.58, -30.54) * mm, "end": v(-17.4, -30.92) * mm});
            skLineSegment(sketch, "E210.11.3", {"start": v(-17.4, -30.92) * mm, "end": v(-14.38, -30.23) * mm});
            skLineSegment(sketch, "E210.11.4", {"start": v(-14.38, -30.23) * mm, "end": v(-14.2, -30.54) * mm});
            skLineSegment(sketch, "E210.12.0", {"start": v(-14.02, -30.84) * mm, "end": v(-14.2, -30.54) * mm});
            skLineSegment(sketch, "E210.12.1", {"start": v(-16.13, -33.11) * mm, "end": v(-14.02, -30.84) * mm});
            skArc(sketch, "E210.12.2", {"start": v(-16.13, -33.11) * mm, "mid": v(-15.9, -33.46) * mm, "end": v(-15.65, -33.8) * mm});
            skLineSegment(sketch, "E210.12.3", {"start": v(-15.65, -33.8) * mm, "end": v(-12.8, -32.6) * mm});
            skLineSegment(sketch, "E210.12.4", {"start": v(-12.8, -32.6) * mm, "end": v(-12.57, -32.88) * mm});
            skLineSegment(sketch, "E210.13.0", {"start": v(-12.33, -33.15) * mm, "end": v(-12.57, -32.88) * mm});
            skLineSegment(sketch, "E210.13.1", {"start": v(-14.01, -35.75) * mm, "end": v(-12.33, -33.15) * mm});
            skArc(sketch, "E210.13.2", {"start": v(-14.01, -35.75) * mm, "mid": v(-13.72, -36.05) * mm, "end": v(-13.42, -36.35) * mm});
            skLineSegment(sketch, "E210.13.3", {"start": v(-13.42, -36.35) * mm, "end": v(-10.81, -34.67) * mm});
            skLineSegment(sketch, "E210.13.4", {"start": v(-10.81, -34.67) * mm, "end": v(-10.54, -34.9) * mm});
            skLineSegment(sketch, "E210.14.0", {"start": v(-10.27, -35.13) * mm, "end": v(-10.54, -34.9) * mm});
            skLineSegment(sketch, "E210.14.1", {"start": v(-11.47, -37.98) * mm, "end": v(-10.27, -35.13) * mm});
            skArc(sketch, "E210.14.2", {"start": v(-11.47, -37.98) * mm, "mid": v(-11.13, -38.23) * mm, "end": v(-10.78, -38.47) * mm});
            skLineSegment(sketch, "E210.14.3", {"start": v(-10.78, -38.47) * mm, "end": v(-8.5, -36.36) * mm});
            skLineSegment(sketch, "E210.14.4", {"start": v(-8.5, -36.36) * mm, "end": v(-8.2, -36.54) * mm});
            skLineSegment(sketch, "E210.15.0", {"start": v(-7.89, -36.72) * mm, "end": v(-8.2, -36.54) * mm});
            skLineSegment(sketch, "E210.15.1", {"start": v(-8.58, -39.74) * mm, "end": v(-7.89, -36.72) * mm});
            skArc(sketch, "E210.15.2", {"start": v(-8.58, -39.74) * mm, "mid": v(-8.2, -39.92) * mm, "end": v(-7.81, -40.1) * mm});
            skLineSegment(sketch, "E210.15.3", {"start": v(-7.81, -40.1) * mm, "end": v(-5.94, -37.62) * mm});
            skLineSegment(sketch, "E210.15.4", {"start": v(-5.94, -37.62) * mm, "end": v(-5.61, -37.75) * mm});
            skLineSegment(sketch, "E210.16.0", {"start": v(-5.27, -37.87) * mm, "end": v(-5.61, -37.75) * mm});
            skLineSegment(sketch, "E210.16.1", {"start": v(-5.43, -40.96) * mm, "end": v(-5.27, -37.87) * mm});
            skArc(sketch, "E210.16.2", {"start": v(-5.43, -40.96) * mm, "mid": v(-5.02, -41.08) * mm, "end": v(-4.61, -41.18) * mm});
            skLineSegment(sketch, "E210.16.3", {"start": v(-4.61, -41.18) * mm, "end": v(-3.2, -38.42) * mm});
            skLineSegment(sketch, "E210.16.4", {"start": v(-3.2, -38.42) * mm, "end": v(-2.85, -38.5) * mm});
            skLineSegment(sketch, "E210.17.0", {"start": v(-2.5, -38.55) * mm, "end": v(-2.85, -38.5) * mm});
            skLineSegment(sketch, "E210.17.1", {"start": v(-2.11, -41.62) * mm, "end": v(-2.5, -38.55) * mm});
            skArc(sketch, "E210.17.2", {"start": v(-2.11, -41.62) * mm, "mid": v(-1.7, -41.66) * mm, "end": v(-1.27, -41.7) * mm});
            skLineSegment(sketch, "E210.17.3", {"start": v(-1.27, -41.7) * mm, "end": v(-0.36, -38.73) * mm});
            skLineSegment(sketch, "E210.17.4", {"start": v(-0.36, -38.73) * mm, "end": v(0, -38.74) * mm});
            skLineSegment(sketch, "E210.18.0", {"start": v(0.36, -38.73) * mm, "end": v(0, -38.74) * mm});
            skLineSegment(sketch, "E210.18.1", {"start": v(1.27, -41.7) * mm, "end": v(0.36, -38.73) * mm});
            skArc(sketch, "E210.18.2", {"start": v(1.27, -41.7) * mm, "mid": v(1.7, -41.66) * mm, "end": v(2.11, -41.62) * mm});
            skLineSegment(sketch, "E210.18.3", {"start": v(2.11, -41.62) * mm, "end": v(2.5, -38.55) * mm});
            skLineSegment(sketch, "E210.18.4", {"start": v(2.5, -38.55) * mm, "end": v(2.85, -38.5) * mm});
            skLineSegment(sketch, "E210.19.0", {"start": v(3.2, -38.42) * mm, "end": v(2.85, -38.5) * mm});
            skLineSegment(sketch, "E210.19.1", {"start": v(4.61, -41.18) * mm, "end": v(3.2, -38.42) * mm});
            skArc(sketch, "E210.19.2", {"start": v(4.61, -41.18) * mm, "mid": v(5.02, -41.08) * mm, "end": v(5.43, -40.96) * mm});
            skLineSegment(sketch, "E210.19.3", {"start": v(5.43, -40.96) * mm, "end": v(5.27, -37.87) * mm});
            skLineSegment(sketch, "E210.19.4", {"start": v(5.27, -37.87) * mm, "end": v(5.61, -37.75) * mm});
            skLineSegment(sketch, "E210.20.0", {"start": v(5.94, -37.62) * mm, "end": v(5.61, -37.75) * mm});
            skLineSegment(sketch, "E210.20.1", {"start": v(7.81, -40.1) * mm, "end": v(5.94, -37.62) * mm});
            skArc(sketch, "E210.20.2", {"start": v(7.81, -40.1) * mm, "mid": v(8.2, -39.92) * mm, "end": v(8.58, -39.74) * mm});
            skLineSegment(sketch, "E210.20.3", {"start": v(8.58, -39.74) * mm, "end": v(7.89, -36.72) * mm});
            skLineSegment(sketch, "E210.20.4", {"start": v(7.89, -36.72) * mm, "end": v(8.2, -36.54) * mm});
            skLineSegment(sketch, "E210.21.0", {"start": v(8.5, -36.36) * mm, "end": v(8.2, -36.54) * mm});
            skLineSegment(sketch, "E210.21.1", {"start": v(10.78, -38.47) * mm, "end": v(8.5, -36.36) * mm});
            skArc(sketch, "E210.21.2", {"start": v(10.78, -38.47) * mm, "mid": v(11.13, -38.23) * mm, "end": v(11.47, -37.98) * mm});
            skLineSegment(sketch, "E210.21.3", {"start": v(11.47, -37.98) * mm, "end": v(10.27, -35.13) * mm});
            skLineSegment(sketch, "E210.21.4", {"start": v(10.27, -35.13) * mm, "end": v(10.54, -34.9) * mm});
            skLineSegment(sketch, "E210.22.0", {"start": v(10.81, -34.67) * mm, "end": v(10.54, -34.9) * mm});
            skLineSegment(sketch, "E210.22.1", {"start": v(13.42, -36.35) * mm, "end": v(10.81, -34.67) * mm});
            skArc(sketch, "E210.22.2", {"start": v(13.42, -36.35) * mm, "mid": v(13.72, -36.05) * mm, "end": v(14.01, -35.75) * mm});
            skLineSegment(sketch, "E210.22.3", {"start": v(14.01, -35.75) * mm, "end": v(12.33, -33.15) * mm});
            skLineSegment(sketch, "E210.22.4", {"start": v(12.33, -33.15) * mm, "end": v(12.57, -32.88) * mm});
            skLineSegment(sketch, "E210.23.0", {"start": v(12.8, -32.6) * mm, "end": v(12.57, -32.88) * mm});
            skLineSegment(sketch, "E210.23.1", {"start": v(15.65, -33.8) * mm, "end": v(12.8, -32.6) * mm});
            skArc(sketch, "E210.23.2", {"start": v(15.65, -33.8) * mm, "mid": v(15.9, -33.46) * mm, "end": v(16.13, -33.11) * mm});
            skLineSegment(sketch, "E210.23.3", {"start": v(16.13, -33.11) * mm, "end": v(14.02, -30.84) * mm});
            skLineSegment(sketch, "E210.23.4", {"start": v(14.02, -30.84) * mm, "end": v(14.2, -30.54) * mm});
            skLineSegment(sketch, "E210.24.0", {"start": v(14.38, -30.23) * mm, "end": v(14.2, -30.54) * mm});
            skLineSegment(sketch, "E210.24.1", {"start": v(17.4, -30.92) * mm, "end": v(14.38, -30.23) * mm});
            skArc(sketch, "E210.24.2", {"start": v(17.4, -30.92) * mm, "mid": v(17.58, -30.54) * mm, "end": v(17.76, -30.15) * mm});
            skLineSegment(sketch, "E210.24.3", {"start": v(17.76, -30.15) * mm, "end": v(15.28, -28.28) * mm});
            skLineSegment(sketch, "E210.24.4", {"start": v(15.28, -28.28) * mm, "end": v(15.41, -27.95) * mm});
            skLineSegment(sketch, "E210.25.0", {"start": v(15.53, -27.6) * mm, "end": v(15.41, -27.95) * mm});
            skLineSegment(sketch, "E210.25.1", {"start": v(18.62, -27.77) * mm, "end": v(15.53, -27.6) * mm});
            skArc(sketch, "E210.25.2", {"start": v(18.62, -27.77) * mm, "mid": v(18.74, -27.36) * mm, "end": v(18.84, -26.95) * mm});
            skLineSegment(sketch, "E210.25.3", {"start": v(18.84, -26.95) * mm, "end": v(16.08, -25.54) * mm});
            skLineSegment(sketch, "E210.25.4", {"start": v(16.08, -25.54) * mm, "end": v(16.15, -25.19) * mm});
            skLineSegment(sketch, "E210.26.0", {"start": v(16.2, -24.83) * mm, "end": v(16.15, -25.19) * mm});
            skLineSegment(sketch, "E210.26.1", {"start": v(19.28, -24.45) * mm, "end": v(16.2, -24.83) * mm});
            skArc(sketch, "E210.26.2", {"start": v(19.28, -24.45) * mm, "mid": v(19.33, -24.03) * mm, "end": v(19.36, -23.6) * mm});
            skLineSegment(sketch, "E210.26.3", {"start": v(19.36, -23.6) * mm, "end": v(16.4, -22.7) * mm});
            skLineSegment(sketch, "E210.26.4", {"start": v(16.4, -22.7) * mm, "end": v(16.4, -22.34) * mm});
            skLineSegment(sketch, "E210.27.0", {"start": v(16.4, -21.98) * mm, "end": v(16.4, -22.34) * mm});
            skLineSegment(sketch, "E210.27.1", {"start": v(19.36, -21.07) * mm, "end": v(16.4, -21.98) * mm});
            skArc(sketch, "E210.27.2", {"start": v(19.36, -21.07) * mm, "mid": v(19.33, -20.65) * mm, "end": v(19.28, -20.22) * mm});
            skLineSegment(sketch, "E210.27.3", {"start": v(19.28, -20.22) * mm, "end": v(16.2, -19.84) * mm});
            skLineSegment(sketch, "E210.27.4", {"start": v(16.2, -19.84) * mm, "end": v(16.15, -19.49) * mm});
            skLineSegment(sketch, "E210.28.0", {"start": v(16.08, -19.14) * mm, "end": v(16.15, -19.49) * mm});
            skLineSegment(sketch, "E210.28.1", {"start": v(18.84, -17.73) * mm, "end": v(16.08, -19.14) * mm});
            skArc(sketch, "E210.28.2", {"start": v(18.84, -17.73) * mm, "mid": v(18.74, -17.32) * mm, "end": v(18.62, -16.9) * mm});
            skLineSegment(sketch, "E210.28.3", {"start": v(18.62, -16.9) * mm, "end": v(15.53, -17.07) * mm});
            skLineSegment(sketch, "E210.28.4", {"start": v(15.53, -17.07) * mm, "end": v(15.41, -16.73) * mm});
            skLineSegment(sketch, "E210.29.0", {"start": v(15.28, -16.4) * mm, "end": v(15.41, -16.73) * mm});
            skLineSegment(sketch, "E210.29.1", {"start": v(17.76, -14.52) * mm, "end": v(15.28, -16.4) * mm});
            skArc(sketch, "E210.29.2", {"start": v(17.76, -14.52) * mm, "mid": v(17.58, -14.14) * mm, "end": v(17.4, -13.76) * mm});
            skLineSegment(sketch, "E210.29.3", {"start": v(17.4, -13.76) * mm, "end": v(14.38, -14.45) * mm});
            skLineSegment(sketch, "E210.29.4", {"start": v(14.38, -14.45) * mm, "end": v(14.2, -14.13) * mm});
            skLineSegment(sketch, "E210.30.0", {"start": v(14.02, -13.83) * mm, "end": v(14.2, -14.13) * mm});
            skLineSegment(sketch, "E210.30.1", {"start": v(16.13, -11.56) * mm, "end": v(14.02, -13.83) * mm});
            skArc(sketch, "E210.30.2", {"start": v(16.13, -11.56) * mm, "mid": v(15.9, -11.2) * mm, "end": v(15.65, -10.87) * mm});
            skLineSegment(sketch, "E210.30.3", {"start": v(15.65, -10.87) * mm, "end": v(12.8, -12.07) * mm});
            skLineSegment(sketch, "E210.30.4", {"start": v(12.8, -12.07) * mm, "end": v(12.57, -11.8) * mm});
            skLineSegment(sketch, "E210.31.0", {"start": v(12.33, -11.52) * mm, "end": v(12.57, -11.8) * mm});
            skLineSegment(sketch, "E210.31.1", {"start": v(14.01, -8.92) * mm, "end": v(12.33, -11.52) * mm});
            skArc(sketch, "E210.31.2", {"start": v(14.01, -8.92) * mm, "mid": v(13.72, -8.62) * mm, "end": v(13.42, -8.32) * mm});
            skLineSegment(sketch, "E210.31.3", {"start": v(13.42, -8.32) * mm, "end": v(10.81, -10) * mm});
            skLineSegment(sketch, "E210.31.4", {"start": v(10.81, -10) * mm, "end": v(10.54, -9.77) * mm});
            skLineSegment(sketch, "E210.32.0", {"start": v(10.27, -9.55) * mm, "end": v(10.54, -9.77) * mm});
            skLineSegment(sketch, "E210.32.1", {"start": v(11.47, -6.7) * mm, "end": v(10.27, -9.55) * mm});
            skArc(sketch, "E210.32.2", {"start": v(11.47, -6.7) * mm, "mid": v(11.13, -6.45) * mm, "end": v(10.78, -6.2) * mm});
            skLineSegment(sketch, "E210.32.3", {"start": v(10.78, -6.2) * mm, "end": v(8.5, -8.32) * mm});
            skLineSegment(sketch, "E210.32.4", {"start": v(8.5, -8.32) * mm, "end": v(8.2, -8.13) * mm});
            skLineSegment(sketch, "E210.33.0", {"start": v(7.89, -7.96) * mm, "end": v(8.2, -8.13) * mm});
            skLineSegment(sketch, "E210.33.1", {"start": v(8.58, -4.94) * mm, "end": v(7.89, -7.96) * mm});
            skArc(sketch, "E210.33.2", {"start": v(8.58, -4.94) * mm, "mid": v(8.2, -4.75) * mm, "end": v(7.81, -4.58) * mm});
            skLineSegment(sketch, "E210.33.3", {"start": v(7.81, -4.58) * mm, "end": v(5.94, -7.05) * mm});
            skLineSegment(sketch, "E210.33.4", {"start": v(5.94, -7.05) * mm, "end": v(5.61, -6.92) * mm});
            skLineSegment(sketch, "E210.34.0", {"start": v(5.27, -6.8) * mm, "end": v(5.61, -6.92) * mm});
            skLineSegment(sketch, "E210.34.1", {"start": v(5.43, -3.71) * mm, "end": v(5.27, -6.8) * mm});
            skArc(sketch, "E210.34.2", {"start": v(5.43, -3.71) * mm, "mid": v(5.02, -3.6) * mm, "end": v(4.61, -3.5) * mm});
            skLineSegment(sketch, "E210.34.3", {"start": v(4.61, -3.5) * mm, "end": v(3.2, -6.25) * mm});
            skLineSegment(sketch, "E210.34.4", {"start": v(3.2, -6.25) * mm, "end": v(2.85, -6.18) * mm});
            skLineSegment(sketch, "E210.35.0", {"start": v(2.5, -6.13) * mm, "end": v(2.85, -6.18) * mm});
            skLineSegment(sketch, "E210.35.1", {"start": v(2.11, -3.05) * mm, "end": v(2.5, -6.13) * mm});
            skArc(sketch, "E210.35.2", {"start": v(2.11, -3.05) * mm, "mid": v(1.7, -3.01) * mm, "end": v(1.27, -2.98) * mm});
            skLineSegment(sketch, "E210.35.3", {"start": v(1.27, -2.98) * mm, "end": v(0.36, -5.94) * mm});
            skLineSegment(sketch, "E210.35.4", {"start": v(0.36, -5.94) * mm, "end": v(0, -5.93) * mm});
            skLineSegment(sketch, "E211", {"start": v(25.71, -45.04) * mm, "end": v(70.51, -45.04) * mm, "construction": true});
            skLineSegment(sketch, "E212", {"start": v(70.51, -45.04) * mm, "end": v(64.51, -39.04) * mm, "construction": true});
            skLineSegment(sketch, "E213", {"start": v(64.51, -39.04) * mm, "end": v(31.71, -39.04) * mm, "construction": true});
            skLineSegment(sketch, "E214", {"start": v(31.71, -39.04) * mm, "end": v(25.71, -45.04) * mm, "construction": true});
            skLineSegment(sketch, "E215", {"start": v(70.51, -45.04) * mm, "end": v(70.51, -0.24) * mm, "construction": true});
            skLineSegment(sketch, "E216", {"start": v(70.51, -0.24) * mm, "end": v(64.51, -6.24) * mm, "construction": true});
            skLineSegment(sketch, "E217", {"start": v(64.51, -6.24) * mm, "end": v(64.51, -39.04) * mm, "construction": true});
            skSolve(sketch);
        }
        {
            var Q0;
            Q0=qCreatedBy(makeId("Front.planeOp"),FACE);
            cPlane(context, id + "F35", {"entities" : qUnion([Q0]), "cplaneType" : CPlaneType.OFFSET, "offset" : 6 * mm, "oppositeDirection" : true, "width" : 150 * mm, "height" : 150 * mm});
        }
        {
            var Q0;
            Q0=qCreatedBy(id+"F35.planeOp",FACE);
            var sketch = newSketch(context, id + "F36", { "sketchPlane" : qUnion([Q0])});
            skCircle(sketch, "E218", {"center": v(0, -22.34) * mm, "radius": 22.4 * mm, "construction": true});
            skCircle(sketch, "E219", {"center": v(0, -22.34) * mm, "radius": 25.4 * mm, "construction": true});
            skLineSegment(sketch, "E220", {"start": v(0, -22.34) * mm, "end": v(0, 3.06) * mm, "construction": true});
            skLineSegment(sketch, "E221", {"start": v(0, -22.34) * mm, "end": v(-0.55, 3.06) * mm, "construction": true});
            skLineSegment(sketch, "E222", {"start": v(0, -22.34) * mm, "end": v(-1.1, 3.04) * mm, "construction": true});
            skLineSegment(sketch, "E223", {"start": v(0, -22.34) * mm, "end": v(-1.66, 3) * mm, "construction": true});
            skLineSegment(sketch, "E224", {"start": v(0, -22.34) * mm, "end": v(-2.21, 2.97) * mm, "construction": true});
            skLineSegment(sketch, "E225", {"start": v(0, -22.34) * mm, "end": v(-2.77, 2.91) * mm, "construction": true});
            skLineSegment(sketch, "E226", {"start": v(0, -22.34) * mm, "end": v(-3.32, 2.85) * mm, "construction": true});
            skLineSegment(sketch, "E227", {"start": v(0, -22.34) * mm, "end": v(-3.86, 2.77) * mm, "construction": true});
            skLineSegment(sketch, "E228", {"start": v(0, -22.34) * mm, "end": v(-4.41, 2.68) * mm, "construction": true});
            skArc(sketch, "E229", {"start": v(-1.66, 3) * mm, "mid": v(-2.21, 2.97) * mm, "end": v(-2.77, 2.91) * mm});
            skLineSegment(sketch, "E230", {"start": v(-1.66, 3) * mm, "end": v(-0.49, 0.06) * mm});
            skLineSegment(sketch, "E231", {"start": v(-0.49, 0.06) * mm, "end": v(0, 0.07) * mm});
            skLineSegment(sketch, "E232", {"start": v(-2.77, 2.91) * mm, "end": v(-3.4, -0.2) * mm});
            skLineSegment(sketch, "E233", {"start": v(-3.4, -0.2) * mm, "end": v(-3.9, -0.27) * mm});
            skArc(sketch, "E234.1.0", {"start": v(-6.04, 2.34) * mm, "mid": v(-6.57, 2.2) * mm, "end": v(-7.1, 2.05) * mm});
            skLineSegment(sketch, "E234.1.1", {"start": v(-7.1, 2.05) * mm, "end": v(-7.2, -1.13) * mm});
            skLineSegment(sketch, "E234.1.2", {"start": v(-6.04, 2.34) * mm, "end": v(-4.37, -0.37) * mm});
            skLineSegment(sketch, "E234.1.3", {"start": v(-7.2, -1.13) * mm, "end": v(-7.66, -1.28) * mm});
            skLineSegment(sketch, "E234.1.4", {"start": v(-4.37, -0.37) * mm, "end": v(-3.9, -0.27) * mm});
            skArc(sketch, "E234.2.0", {"start": v(-10.23, 0.91) * mm, "mid": v(-10.73, 0.68) * mm, "end": v(-11.23, 0.44) * mm});
            skLineSegment(sketch, "E234.2.1", {"start": v(-11.23, 0.44) * mm, "end": v(-10.77, -2.7) * mm});
            skLineSegment(sketch, "E234.2.2", {"start": v(-10.23, 0.91) * mm, "end": v(-8.12, -1.46) * mm});
            skLineSegment(sketch, "E234.2.3", {"start": v(-10.77, -2.7) * mm, "end": v(-11.2, -2.93) * mm});
            skLineSegment(sketch, "E234.2.4", {"start": v(-8.12, -1.46) * mm, "end": v(-7.66, -1.28) * mm});
            skLineSegment(sketch, "E235.4.3.0", {"start": v(-15.02, -1.85) * mm, "end": v(-14.02, -4.87) * mm});
            skLineSegment(sketch, "E235.7.3.0", {"start": v(-14.11, -1.22) * mm, "end": v(-11.62, -3.19) * mm});
            skLineSegment(sketch, "E235.10.3.0", {"start": v(-14.02, -4.87) * mm, "end": v(-14.4, -5.17) * mm});
            skLineSegment(sketch, "E235.13.3.0", {"start": v(-11.62, -3.19) * mm, "end": v(-11.2, -2.93) * mm});
            skArc(sketch, "E235.15.3.0", {"start": v(-14.11, -1.22) * mm, "mid": v(-14.57, -1.53) * mm, "end": v(-15.02, -1.85) * mm});
            skLineSegment(sketch, "E235.4.4.0", {"start": v(-18.35, -4.77) * mm, "end": v(-16.84, -7.57) * mm});
            skLineSegment(sketch, "E235.7.4.0", {"start": v(-17.56, -3.99) * mm, "end": v(-14.77, -5.5) * mm});
            skLineSegment(sketch, "E235.10.4.0", {"start": v(-16.84, -7.57) * mm, "end": v(-17.16, -7.94) * mm});
            skLineSegment(sketch, "E235.13.4.0", {"start": v(-14.77, -5.5) * mm, "end": v(-14.4, -5.17) * mm});
            skArc(sketch, "E235.15.4.0", {"start": v(-17.56, -3.99) * mm, "mid": v(-17.96, -4.38) * mm, "end": v(-18.35, -4.77) * mm});
            skLineSegment(sketch, "E235.4.5.0", {"start": v(-21.12, -8.23) * mm, "end": v(-19.15, -10.72) * mm});
            skLineSegment(sketch, "E235.7.5.0", {"start": v(-20.48, -7.32) * mm, "end": v(-17.47, -8.32) * mm});
            skLineSegment(sketch, "E235.10.5.0", {"start": v(-19.15, -10.72) * mm, "end": v(-19.4, -11.13) * mm});
            skLineSegment(sketch, "E235.13.5.0", {"start": v(-17.47, -8.32) * mm, "end": v(-17.16, -7.94) * mm});
            skArc(sketch, "E235.15.5.0", {"start": v(-20.48, -7.32) * mm, "mid": v(-20.8, -7.77) * mm, "end": v(-21.12, -8.23) * mm});
            skLineSegment(sketch, "E235.4.6.0", {"start": v(-23.25, -12.1) * mm, "end": v(-20.88, -14.22) * mm});
            skLineSegment(sketch, "E235.7.6.0", {"start": v(-22.78, -11.1) * mm, "end": v(-19.64, -11.56) * mm});
            skLineSegment(sketch, "E235.10.6.0", {"start": v(-20.88, -14.22) * mm, "end": v(-21.05, -14.67) * mm});
            skLineSegment(sketch, "E235.13.6.0", {"start": v(-19.64, -11.56) * mm, "end": v(-19.4, -11.13) * mm});
            skArc(sketch, "E235.15.6.0", {"start": v(-22.78, -11.1) * mm, "mid": v(-23.02, -11.6) * mm, "end": v(-23.25, -12.1) * mm});
            skLineSegment(sketch, "E235.4.7.0", {"start": v(-24.67, -16.3) * mm, "end": v(-21.97, -17.97) * mm});
            skLineSegment(sketch, "E235.7.7.0", {"start": v(-24.39, -15.23) * mm, "end": v(-21.21, -15.14) * mm});
            skLineSegment(sketch, "E235.10.7.0", {"start": v(-21.97, -17.97) * mm, "end": v(-22.06, -18.45) * mm});
            skLineSegment(sketch, "E235.13.7.0", {"start": v(-21.21, -15.14) * mm, "end": v(-21.05, -14.67) * mm});
            skArc(sketch, "E235.15.7.0", {"start": v(-24.39, -15.23) * mm, "mid": v(-24.53, -15.76) * mm, "end": v(-24.67, -16.3) * mm});
            skLineSegment(sketch, "E235.4.8.0", {"start": v(-25.35, -20.68) * mm, "end": v(-22.4, -21.85) * mm});
            skLineSegment(sketch, "E235.7.8.0", {"start": v(-25.25, -19.57) * mm, "end": v(-22.14, -18.93) * mm});
            skLineSegment(sketch, "E235.10.8.0", {"start": v(-22.4, -21.85) * mm, "end": v(-22.4, -22.34) * mm});
            skLineSegment(sketch, "E235.13.8.0", {"start": v(-22.14, -18.93) * mm, "end": v(-22.06, -18.45) * mm});
            skArc(sketch, "E235.15.8.0", {"start": v(-25.25, -19.57) * mm, "mid": v(-25.3, -20.12) * mm, "end": v(-25.35, -20.68) * mm});
            skLineSegment(sketch, "E235.4.9.0", {"start": v(-25.25, -25.1) * mm, "end": v(-22.14, -25.74) * mm});
            skLineSegment(sketch, "E235.7.9.0", {"start": v(-25.35, -24) * mm, "end": v(-22.4, -22.83) * mm});
            skLineSegment(sketch, "E235.10.9.0", {"start": v(-22.14, -25.74) * mm, "end": v(-22.06, -26.23) * mm});
            skLineSegment(sketch, "E235.13.9.0", {"start": v(-22.4, -22.83) * mm, "end": v(-22.4, -22.34) * mm});
            skArc(sketch, "E235.15.9.0", {"start": v(-25.35, -24) * mm, "mid": v(-25.3, -24.55) * mm, "end": v(-25.25, -25.1) * mm});
            skLineSegment(sketch, "E235.4.10.0", {"start": v(-24.39, -29.44) * mm, "end": v(-21.21, -29.54) * mm});
            skLineSegment(sketch, "E235.7.10.0", {"start": v(-24.67, -28.37) * mm, "end": v(-21.97, -26.7) * mm});
            skLineSegment(sketch, "E235.10.10.0", {"start": v(-21.21, -29.54) * mm, "end": v(-21.05, -30) * mm});
            skLineSegment(sketch, "E235.13.10.0", {"start": v(-21.97, -26.7) * mm, "end": v(-22.06, -26.23) * mm});
            skArc(sketch, "E235.15.10.0", {"start": v(-24.67, -28.37) * mm, "mid": v(-24.53, -28.91) * mm, "end": v(-24.39, -29.44) * mm});
            skLineSegment(sketch, "E235.4.11.0", {"start": v(-22.78, -33.57) * mm, "end": v(-19.64, -33.11) * mm});
            skLineSegment(sketch, "E235.7.11.0", {"start": v(-23.25, -32.57) * mm, "end": v(-20.88, -30.46) * mm});
            skLineSegment(sketch, "E235.10.11.0", {"start": v(-19.64, -33.11) * mm, "end": v(-19.4, -33.54) * mm});
            skLineSegment(sketch, "E235.13.11.0", {"start": v(-20.88, -30.46) * mm, "end": v(-21.05, -30) * mm});
            skArc(sketch, "E235.15.11.0", {"start": v(-23.25, -32.57) * mm, "mid": v(-23.02, -33.07) * mm, "end": v(-22.78, -33.57) * mm});
            skLineSegment(sketch, "E235.4.12.0", {"start": v(-20.48, -37.36) * mm, "end": v(-17.47, -36.36) * mm});
            skLineSegment(sketch, "E235.7.12.0", {"start": v(-21.12, -36.45) * mm, "end": v(-19.15, -33.96) * mm});
            skLineSegment(sketch, "E235.10.12.0", {"start": v(-17.47, -36.36) * mm, "end": v(-17.16, -36.74) * mm});
            skLineSegment(sketch, "E235.13.12.0", {"start": v(-19.15, -33.96) * mm, "end": v(-19.4, -33.54) * mm});
            skArc(sketch, "E235.15.12.0", {"start": v(-21.12, -36.45) * mm, "mid": v(-20.8, -36.9) * mm, "end": v(-20.48, -37.36) * mm});
            skLineSegment(sketch, "E235.4.13.0", {"start": v(-17.56, -40.68) * mm, "end": v(-14.77, -39.18) * mm});
            skLineSegment(sketch, "E235.7.13.0", {"start": v(-18.35, -39.9) * mm, "end": v(-16.84, -37.1) * mm});
            skLineSegment(sketch, "E235.10.13.0", {"start": v(-14.77, -39.18) * mm, "end": v(-14.4, -39.5) * mm});
            skLineSegment(sketch, "E235.13.13.0", {"start": v(-16.84, -37.1) * mm, "end": v(-17.16, -36.74) * mm});
            skArc(sketch, "E235.15.13.0", {"start": v(-18.35, -39.9) * mm, "mid": v(-17.96, -40.3) * mm, "end": v(-17.56, -40.68) * mm});
            skLineSegment(sketch, "E235.4.14.0", {"start": v(-14.11, -43.46) * mm, "end": v(-11.62, -41.49) * mm});
            skLineSegment(sketch, "E235.7.14.0", {"start": v(-15.02, -42.82) * mm, "end": v(-14.02, -39.8) * mm});
            skLineSegment(sketch, "E235.10.14.0", {"start": v(-11.62, -41.49) * mm, "end": v(-11.2, -41.74) * mm});
            skLineSegment(sketch, "E235.13.14.0", {"start": v(-14.02, -39.8) * mm, "end": v(-14.4, -39.5) * mm});
            skArc(sketch, "E235.15.14.0", {"start": v(-15.02, -42.82) * mm, "mid": v(-14.57, -43.14) * mm, "end": v(-14.11, -43.46) * mm});
            skLineSegment(sketch, "E235.4.15.0", {"start": v(-10.23, -45.59) * mm, "end": v(-8.12, -43.21) * mm});
            skLineSegment(sketch, "E235.7.15.0", {"start": v(-11.23, -45.12) * mm, "end": v(-10.77, -41.98) * mm});
            skLineSegment(sketch, "E235.10.15.0", {"start": v(-8.12, -43.21) * mm, "end": v(-7.66, -43.4) * mm});
            skLineSegment(sketch, "E235.13.15.0", {"start": v(-10.77, -41.98) * mm, "end": v(-11.2, -41.74) * mm});
            skArc(sketch, "E235.15.15.0", {"start": v(-11.23, -45.12) * mm, "mid": v(-10.73, -45.36) * mm, "end": v(-10.23, -45.59) * mm});
            skLineSegment(sketch, "E235.4.16.0", {"start": v(-6.04, -47) * mm, "end": v(-4.37, -44.3) * mm});
            skLineSegment(sketch, "E235.7.16.0", {"start": v(-7.1, -46.72) * mm, "end": v(-7.2, -43.55) * mm});
            skLineSegment(sketch, "E235.10.16.0", {"start": v(-4.37, -44.3) * mm, "end": v(-3.9, -44.4) * mm});
            skLineSegment(sketch, "E235.13.16.0", {"start": v(-7.2, -43.55) * mm, "end": v(-7.66, -43.4) * mm});
            skArc(sketch, "E235.15.16.0", {"start": v(-7.1, -46.72) * mm, "mid": v(-6.57, -46.87) * mm, "end": v(-6.04, -47) * mm});
            skLineSegment(sketch, "E235.4.17.0", {"start": v(-1.66, -47.68) * mm, "end": v(-0.49, -44.73) * mm});
            skLineSegment(sketch, "E235.7.17.0", {"start": v(-2.77, -47.59) * mm, "end": v(-3.4, -44.48) * mm});
            skLineSegment(sketch, "E235.10.17.0", {"start": v(-0.49, -44.73) * mm, "end": v(0, -44.74) * mm});
            skLineSegment(sketch, "E235.13.17.0", {"start": v(-3.4, -44.48) * mm, "end": v(-3.9, -44.4) * mm});
            skArc(sketch, "E235.15.17.0", {"start": v(-2.77, -47.59) * mm, "mid": v(-2.21, -47.64) * mm, "end": v(-1.66, -47.68) * mm});
            skLineSegment(sketch, "E235.4.18.0", {"start": v(2.77, -47.59) * mm, "end": v(3.4, -44.48) * mm});
            skLineSegment(sketch, "E235.7.18.0", {"start": v(1.66, -47.68) * mm, "end": v(0.49, -44.73) * mm});
            skLineSegment(sketch, "E235.10.18.0", {"start": v(3.4, -44.48) * mm, "end": v(3.9, -44.4) * mm});
            skLineSegment(sketch, "E235.13.18.0", {"start": v(0.49, -44.73) * mm, "end": v(0, -44.74) * mm});
            skArc(sketch, "E235.15.18.0", {"start": v(1.66, -47.68) * mm, "mid": v(2.21, -47.64) * mm, "end": v(2.77, -47.59) * mm});
            skLineSegment(sketch, "E235.4.19.0", {"start": v(7.1, -46.72) * mm, "end": v(7.2, -43.55) * mm});
            skLineSegment(sketch, "E235.7.19.0", {"start": v(6.04, -47) * mm, "end": v(4.37, -44.3) * mm});
            skLineSegment(sketch, "E235.10.19.0", {"start": v(7.2, -43.55) * mm, "end": v(7.66, -43.4) * mm});
            skLineSegment(sketch, "E235.13.19.0", {"start": v(4.37, -44.3) * mm, "end": v(3.9, -44.4) * mm});
            skArc(sketch, "E235.15.19.0", {"start": v(6.04, -47) * mm, "mid": v(6.57, -46.87) * mm, "end": v(7.1, -46.72) * mm});
            skLineSegment(sketch, "E235.4.20.0", {"start": v(11.23, -45.12) * mm, "end": v(10.77, -41.98) * mm});
            skLineSegment(sketch, "E235.7.20.0", {"start": v(10.23, -45.59) * mm, "end": v(8.12, -43.21) * mm});
            skLineSegment(sketch, "E235.10.20.0", {"start": v(10.77, -41.98) * mm, "end": v(11.2, -41.74) * mm});
            skLineSegment(sketch, "E235.13.20.0", {"start": v(8.12, -43.21) * mm, "end": v(7.66, -43.4) * mm});
            skArc(sketch, "E235.15.20.0", {"start": v(10.23, -45.59) * mm, "mid": v(10.73, -45.36) * mm, "end": v(11.23, -45.12) * mm});
            skLineSegment(sketch, "E235.4.21.0", {"start": v(15.02, -42.82) * mm, "end": v(14.02, -39.8) * mm});
            skLineSegment(sketch, "E235.7.21.0", {"start": v(14.11, -43.46) * mm, "end": v(11.62, -41.49) * mm});
            skLineSegment(sketch, "E235.10.21.0", {"start": v(14.02, -39.8) * mm, "end": v(14.4, -39.5) * mm});
            skLineSegment(sketch, "E235.13.21.0", {"start": v(11.62, -41.49) * mm, "end": v(11.2, -41.74) * mm});
            skArc(sketch, "E235.15.21.0", {"start": v(14.11, -43.46) * mm, "mid": v(14.57, -43.14) * mm, "end": v(15.02, -42.82) * mm});
            skLineSegment(sketch, "E235.4.22.0", {"start": v(18.35, -39.9) * mm, "end": v(16.84, -37.1) * mm});
            skLineSegment(sketch, "E235.7.22.0", {"start": v(17.56, -40.68) * mm, "end": v(14.77, -39.18) * mm});
            skLineSegment(sketch, "E235.10.22.0", {"start": v(16.84, -37.1) * mm, "end": v(17.16, -36.74) * mm});
            skLineSegment(sketch, "E235.13.22.0", {"start": v(14.77, -39.18) * mm, "end": v(14.4, -39.5) * mm});
            skArc(sketch, "E235.15.22.0", {"start": v(17.56, -40.68) * mm, "mid": v(17.96, -40.3) * mm, "end": v(18.35, -39.9) * mm});
            skLineSegment(sketch, "E235.4.23.0", {"start": v(21.12, -36.45) * mm, "end": v(19.15, -33.96) * mm});
            skLineSegment(sketch, "E235.7.23.0", {"start": v(20.48, -37.36) * mm, "end": v(17.47, -36.36) * mm});
            skLineSegment(sketch, "E235.10.23.0", {"start": v(19.15, -33.96) * mm, "end": v(19.4, -33.54) * mm});
            skLineSegment(sketch, "E235.13.23.0", {"start": v(17.47, -36.36) * mm, "end": v(17.16, -36.74) * mm});
            skArc(sketch, "E235.15.23.0", {"start": v(20.48, -37.36) * mm, "mid": v(20.8, -36.9) * mm, "end": v(21.12, -36.45) * mm});
            skLineSegment(sketch, "E235.4.24.0", {"start": v(23.25, -32.57) * mm, "end": v(20.88, -30.46) * mm});
            skLineSegment(sketch, "E235.7.24.0", {"start": v(22.78, -33.57) * mm, "end": v(19.64, -33.11) * mm});
            skLineSegment(sketch, "E235.10.24.0", {"start": v(20.88, -30.46) * mm, "end": v(21.05, -30) * mm});
            skLineSegment(sketch, "E235.13.24.0", {"start": v(19.64, -33.11) * mm, "end": v(19.4, -33.54) * mm});
            skArc(sketch, "E235.15.24.0", {"start": v(22.78, -33.57) * mm, "mid": v(23.02, -33.07) * mm, "end": v(23.25, -32.57) * mm});
            skLineSegment(sketch, "E235.4.25.0", {"start": v(24.67, -28.37) * mm, "end": v(21.97, -26.7) * mm});
            skLineSegment(sketch, "E235.7.25.0", {"start": v(24.39, -29.44) * mm, "end": v(21.21, -29.54) * mm});
            skLineSegment(sketch, "E235.10.25.0", {"start": v(21.97, -26.7) * mm, "end": v(22.06, -26.23) * mm});
            skLineSegment(sketch, "E235.13.25.0", {"start": v(21.21, -29.54) * mm, "end": v(21.05, -30) * mm});
            skArc(sketch, "E235.15.25.0", {"start": v(24.39, -29.44) * mm, "mid": v(24.53, -28.91) * mm, "end": v(24.67, -28.37) * mm});
            skLineSegment(sketch, "E235.4.26.0", {"start": v(25.35, -24) * mm, "end": v(22.4, -22.83) * mm});
            skLineSegment(sketch, "E235.7.26.0", {"start": v(25.25, -25.1) * mm, "end": v(22.14, -25.74) * mm});
            skLineSegment(sketch, "E235.10.26.0", {"start": v(22.4, -22.83) * mm, "end": v(22.4, -22.34) * mm});
            skLineSegment(sketch, "E235.13.26.0", {"start": v(22.14, -25.74) * mm, "end": v(22.06, -26.23) * mm});
            skArc(sketch, "E235.15.26.0", {"start": v(25.25, -25.1) * mm, "mid": v(25.3, -24.55) * mm, "end": v(25.35, -24) * mm});
            skLineSegment(sketch, "E235.4.27.0", {"start": v(25.25, -19.57) * mm, "end": v(22.14, -18.93) * mm});
            skLineSegment(sketch, "E235.7.27.0", {"start": v(25.35, -20.68) * mm, "end": v(22.4, -21.85) * mm});
            skLineSegment(sketch, "E235.10.27.0", {"start": v(22.14, -18.93) * mm, "end": v(22.06, -18.45) * mm});
            skLineSegment(sketch, "E235.13.27.0", {"start": v(22.4, -21.85) * mm, "end": v(22.4, -22.34) * mm});
            skArc(sketch, "E235.15.27.0", {"start": v(25.35, -20.68) * mm, "mid": v(25.3, -20.12) * mm, "end": v(25.25, -19.57) * mm});
            skLineSegment(sketch, "E235.4.28.0", {"start": v(24.39, -15.23) * mm, "end": v(21.21, -15.14) * mm});
            skLineSegment(sketch, "E235.7.28.0", {"start": v(24.67, -16.3) * mm, "end": v(21.97, -17.97) * mm});
            skLineSegment(sketch, "E235.10.28.0", {"start": v(21.21, -15.14) * mm, "end": v(21.05, -14.67) * mm});
            skLineSegment(sketch, "E235.13.28.0", {"start": v(21.97, -17.97) * mm, "end": v(22.06, -18.45) * mm});
            skArc(sketch, "E235.15.28.0", {"start": v(24.67, -16.3) * mm, "mid": v(24.53, -15.76) * mm, "end": v(24.39, -15.23) * mm});
            skLineSegment(sketch, "E235.4.29.0", {"start": v(22.78, -11.1) * mm, "end": v(19.64, -11.56) * mm});
            skLineSegment(sketch, "E235.7.29.0", {"start": v(23.25, -12.1) * mm, "end": v(20.88, -14.22) * mm});
            skLineSegment(sketch, "E235.10.29.0", {"start": v(19.64, -11.56) * mm, "end": v(19.4, -11.13) * mm});
            skLineSegment(sketch, "E235.13.29.0", {"start": v(20.88, -14.22) * mm, "end": v(21.05, -14.67) * mm});
            skArc(sketch, "E235.15.29.0", {"start": v(23.25, -12.1) * mm, "mid": v(23.02, -11.6) * mm, "end": v(22.78, -11.1) * mm});
            skLineSegment(sketch, "E235.4.30.0", {"start": v(20.48, -7.32) * mm, "end": v(17.47, -8.32) * mm});
            skLineSegment(sketch, "E235.7.30.0", {"start": v(21.12, -8.23) * mm, "end": v(19.15, -10.72) * mm});
            skLineSegment(sketch, "E235.10.30.0", {"start": v(17.47, -8.32) * mm, "end": v(17.16, -7.94) * mm});
            skLineSegment(sketch, "E235.13.30.0", {"start": v(19.15, -10.72) * mm, "end": v(19.4, -11.13) * mm});
            skArc(sketch, "E235.15.30.0", {"start": v(21.12, -8.23) * mm, "mid": v(20.8, -7.77) * mm, "end": v(20.48, -7.32) * mm});
            skLineSegment(sketch, "E235.4.31.0", {"start": v(17.56, -3.99) * mm, "end": v(14.77, -5.5) * mm});
            skLineSegment(sketch, "E235.7.31.0", {"start": v(18.35, -4.77) * mm, "end": v(16.84, -7.57) * mm});
            skLineSegment(sketch, "E235.10.31.0", {"start": v(14.77, -5.5) * mm, "end": v(14.4, -5.17) * mm});
            skLineSegment(sketch, "E235.13.31.0", {"start": v(16.84, -7.57) * mm, "end": v(17.16, -7.94) * mm});
            skArc(sketch, "E235.15.31.0", {"start": v(18.35, -4.77) * mm, "mid": v(17.96, -4.38) * mm, "end": v(17.56, -3.99) * mm});
            skLineSegment(sketch, "E235.4.32.0", {"start": v(14.11, -1.22) * mm, "end": v(11.62, -3.19) * mm});
            skLineSegment(sketch, "E235.7.32.0", {"start": v(15.02, -1.85) * mm, "end": v(14.02, -4.87) * mm});
            skLineSegment(sketch, "E235.10.32.0", {"start": v(11.62, -3.19) * mm, "end": v(11.2, -2.93) * mm});
            skLineSegment(sketch, "E235.13.32.0", {"start": v(14.02, -4.87) * mm, "end": v(14.4, -5.17) * mm});
            skArc(sketch, "E235.15.32.0", {"start": v(15.02, -1.85) * mm, "mid": v(14.57, -1.53) * mm, "end": v(14.11, -1.22) * mm});
            skLineSegment(sketch, "E235.4.33.0", {"start": v(10.23, 0.91) * mm, "end": v(8.12, -1.46) * mm});
            skLineSegment(sketch, "E235.7.33.0", {"start": v(11.23, 0.44) * mm, "end": v(10.77, -2.7) * mm});
            skLineSegment(sketch, "E235.10.33.0", {"start": v(8.12, -1.46) * mm, "end": v(7.66, -1.28) * mm});
            skLineSegment(sketch, "E235.13.33.0", {"start": v(10.77, -2.7) * mm, "end": v(11.2, -2.93) * mm});
            skArc(sketch, "E235.15.33.0", {"start": v(11.23, 0.44) * mm, "mid": v(10.73, 0.68) * mm, "end": v(10.23, 0.91) * mm});
            skLineSegment(sketch, "E235.4.34.0", {"start": v(6.04, 2.34) * mm, "end": v(4.37, -0.37) * mm});
            skLineSegment(sketch, "E235.7.34.0", {"start": v(7.1, 2.05) * mm, "end": v(7.2, -1.13) * mm});
            skLineSegment(sketch, "E235.10.34.0", {"start": v(4.37, -0.37) * mm, "end": v(3.9, -0.27) * mm});
            skLineSegment(sketch, "E235.13.34.0", {"start": v(7.2, -1.13) * mm, "end": v(7.66, -1.28) * mm});
            skArc(sketch, "E235.15.34.0", {"start": v(7.1, 2.05) * mm, "mid": v(6.57, 2.2) * mm, "end": v(6.04, 2.34) * mm});
            skLineSegment(sketch, "E235.4.35.0", {"start": v(1.66, 3) * mm, "end": v(0.49, 0.06) * mm});
            skLineSegment(sketch, "E235.7.35.0", {"start": v(2.77, 2.91) * mm, "end": v(3.4, -0.2) * mm});
            skLineSegment(sketch, "E235.10.35.0", {"start": v(0.49, 0.06) * mm, "end": v(0, 0.07) * mm});
            skLineSegment(sketch, "E235.13.35.0", {"start": v(3.4, -0.2) * mm, "end": v(3.9, -0.27) * mm});
            skArc(sketch, "E235.15.35.0", {"start": v(2.77, 2.91) * mm, "mid": v(2.21, 2.97) * mm, "end": v(1.66, 3) * mm});
            skSolve(sketch);
        }
        {
            var Q0;
            Q0=sQuery(id+"F34.wireOp",VERTEX,"E210.9.2.start");
            var Q1;
            Q1=sQuery(id+"F36.wireOp",VERTEX,"E235.15.9.0.start");
            var Q2;
            Q2=sQuery(id+"F34.wireOp",VERTEX,"E210.9.3.start");
            cPlane(context, id + "F37", {"entities" : qUnion([Q0, Q1, Q2]), "cplaneType" : CPlaneType.THREE_POINT, "offset" : 150 * mm, "width" : 150 * mm, "height" : 150 * mm});
        }
        {
            var Q0;
            Q0=qCreatedBy(id+"F37.planeOp",FACE);
            var sketch = newSketch(context, id + "F38", { "sketchPlane" : qUnion([Q0])});
            skLineSegment(sketch, "E236", {"start": v(20.73, -24.43) * mm, "end": v(12.3, -23.52) * mm});
            skSolve(sketch);
        }
        {
            var Q1;
            Q1=makeQuery(id+"F36.imprint","IMPRINT",FACE,{"disambiguationData":[TD([[makeQuery(id+"F36.imprint","IMPRINT",EDGE,{"derivedFrom":sQuery(id+"F36.wireOp",EDGE,"E229")}),1.0]])]});
            var Q2;
            Q2=makeQuery(id+"F34.imprint","IMPRINT",FACE,{"disambiguationData":[TD([[makeQuery(id+"F34.imprint","IMPRINT",EDGE,{"derivedFrom":sQuery(id+"F34.wireOp",EDGE,"E205")}),1.0]])]});
            var Q3;
            Q3=sQuery(id+"F38.wireOp",EDGE,"E236");
            loft(context, id + "F39", {"sheetProfilesArray" : [{ "sheetProfileEntities" : qUnion([Q1]) }, { "sheetProfileEntities" : qUnion([Q2]) }], "guidesArray" : [{ "guideEntities" : qUnion([Q3]), "guideDerivativeType" : LoftGuideDerivativeType.DEFAULT, "guideDerivativeMagnitude" : 1 }]});
        }
        {
            var Q0;
            Q0=makeQuery(id+"F39.opLoft","CAP_FACE",FACE,{"disambiguationData":[OSD([makeQuery(id+"F34.imprint","IMPRINT",FACE,{"disambiguationData":[TD([[makeQuery(id+"F34.imprint","IMPRINT",EDGE,{"derivedFrom":sQuery(id+"F34.wireOp",EDGE,"E205")}),1.0]])]})])],"isStart":true});
            var sketch = newSketch(context, id + "F40", { "sketchPlane" : qUnion([Q0])});
            skCircle(sketch, "E237", {"center": v(0, -22.34) * mm, "radius": 2.5 * mm});
            skSolve(sketch);
        }
        {
            var Q0;
            Q0=makeQuery(id+"F40.imprint","IMPRINT",FACE,{"disambiguationData":[TD([[makeQuery(id+"F40.imprint","IMPRINT",EDGE,{"derivedFrom":sQuery(id+"F40.wireOp",EDGE,"E237")}),1.0]])]});
            extrude(context, id + "F41", {"entities" : qUnion([Q0]), "operationType" : NewBodyOperationType.REMOVE, "oppositeDirection" : true, "depth" : 25 * mm});
        }
        {
            var Q0;
            Q0=qCreatedBy(makeId("Top.planeOp"),FACE);
            cPlane(context, id + "F42", {"entities" : qUnion([Q0]), "cplaneType" : CPlaneType.OFFSET, "offset" : 500 * mm, "oppositeDirection" : true, "width" : 150 * mm, "height" : 150 * mm});
        }
    });
